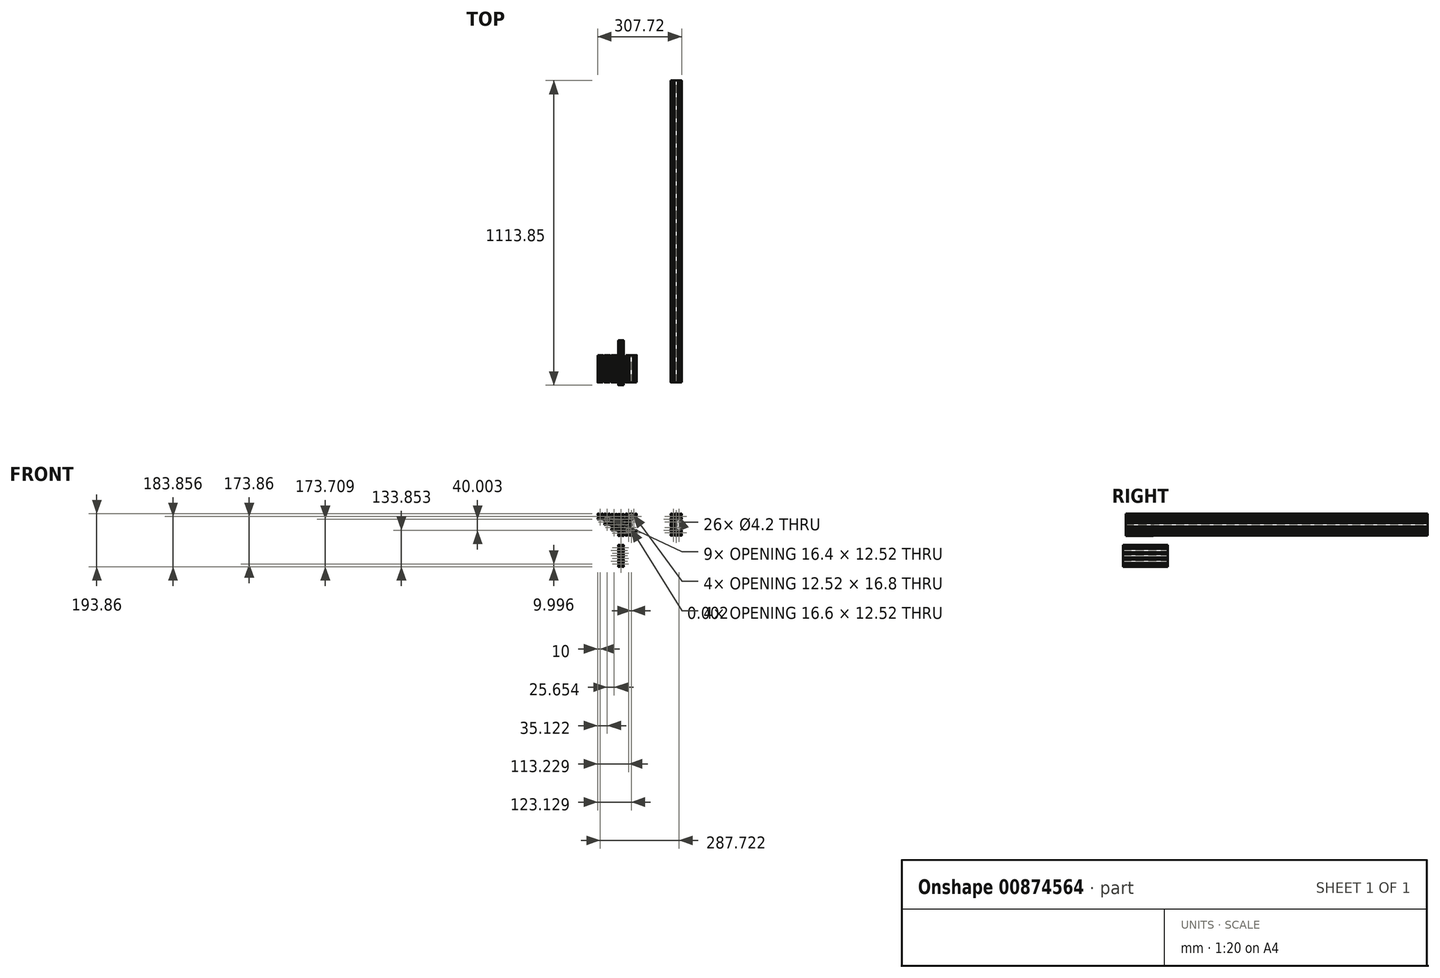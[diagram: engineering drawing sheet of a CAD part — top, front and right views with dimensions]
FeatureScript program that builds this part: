
annotation { "Feature Type Name" : "Feature", "Feature Type Description" : "" }
export const myFeature = defineFeature(function(context is Context, id is Id, definition is map)
    precondition{}
    {
        {
            var Q0;
            Q0=qCreatedBy(makeId("Front.planeOp"),FACE);
            var sketch = newSketch(context, id + "F0", { "sketchPlane" : qUnion([Q0])});
            skLineSegment(sketch, "E0", {"start": v(-0.16, 3.9) * mm, "end": v(-2.84, 3.9) * mm});
            skLineSegment(sketch, "E1", {"start": v(-2.84, 3.9) * mm, "end": v(-5.7, 6.76) * mm});
            skLineSegment(sketch, "E2", {"start": v(-5.7, 6.76) * mm, "end": v(-5.7, 8.4) * mm});
            skLineSegment(sketch, "E3", {"start": v(-5, 10) * mm, "end": v(-9.5, 10) * mm});
            skLineSegment(sketch, "E4", {"start": v(-10, 9.5) * mm, "end": v(-10, 5) * mm});
            skLineSegment(sketch, "E5", {"start": v(-8.4, 3.8) * mm, "end": v(-8.4, 5.7) * mm});
            skLineSegment(sketch, "E6", {"start": v(-8.4, 5.7) * mm, "end": v(-6.76, 5.7) * mm});
            skLineSegment(sketch, "E7", {"start": v(-6.76, 5.7) * mm, "end": v(-3.9, 2.84) * mm});
            skLineSegment(sketch, "E8", {"start": v(-3.9, 2.84) * mm, "end": v(-3.9, 0.16) * mm});
            skLineSegment(sketch, "E9", {"start": v(0, 0) * mm, "end": v(0, 17.32) * mm, "construction": true});
            skLineSegment(sketch, "E10", {"start": v(0, 0) * mm, "end": v(-27.38, 0) * mm, "construction": true});
            skPoint(sketch, "E11.visualSharp", {"position": v(-10, 10) * mm});
            skArc(sketch, "E11.filletArc", {"start": v(-9.5, 10) * mm, "mid": v(-9.85, 9.85) * mm, "end": v(-10, 9.5) * mm});
            skLineSegment(sketch, "E12.filletArc", {"start": v(-10, 4.72) * mm, "end": v(-10, 4.72) * mm});
            skLineSegment(sketch, "E13", {"start": v(-5.7, 8.4) * mm, "end": v(-3.8, 8.4) * mm});
            skLineSegment(sketch, "E14", {"start": v(-3.67, 8.74) * mm, "end": v(-4.87, 9.94) * mm});
            skLineSegment(sketch, "E15", {"start": v(-8.74, 3.67) * mm, "end": v(-9.94, 4.87) * mm});
            skPoint(sketch, "E16.visualSharp", {"position": v(-8.4, 3.33) * mm});
            skArc(sketch, "E16.filletArc", {"start": v(-8.74, 3.67) * mm, "mid": v(-8.52, 3.62) * mm, "end": v(-8.4, 3.8) * mm});
            skArc(sketch, "E17.filletArc", {"start": v(-3.8, 8.4) * mm, "mid": v(-3.62, 8.52) * mm, "end": v(-3.67, 8.74) * mm});
            skPoint(sketch, "E18.visualSharp", {"position": v(-4.92, 10) * mm});
            skArc(sketch, "E18.filletArc", {"start": v(-4.87, 9.94) * mm, "mid": v(-4.93, 9.99) * mm, "end": v(-5, 10) * mm});
            skPoint(sketch, "E19.visualSharp", {"position": v(-10, 4.93) * mm});
            skArc(sketch, "E19.filletArc", {"start": v(-10, 5) * mm, "mid": v(-9.99, 4.93) * mm, "end": v(-9.94, 4.87) * mm});
            skArc(sketch, "E20.MirrorCS", {"start": v(8.74, 3.67) * mm, "mid": v(8.52, 3.62) * mm, "end": v(8.4, 3.8) * mm});
            skArc(sketch, "E21.MirrorCS", {"start": v(10, 5) * mm, "mid": v(9.99, 4.93) * mm, "end": v(9.94, 4.87) * mm});
            skArc(sketch, "E22.MirrorCS", {"start": v(4.87, 9.94) * mm, "mid": v(4.93, 9.99) * mm, "end": v(5, 10) * mm});
            skArc(sketch, "E23.MirrorCS", {"start": v(3.8, 8.4) * mm, "mid": v(3.62, 8.52) * mm, "end": v(3.67, 8.74) * mm});
            skArc(sketch, "E24.MirrorCS", {"start": v(9.5, 10) * mm, "mid": v(9.85, 9.85) * mm, "end": v(10, 9.5) * mm});
            skPoint(sketch, "E25.MirrorP", {"position": v(8.4, 3.33) * mm});
            skLineSegment(sketch, "E26.MirrorCS", {"start": v(3.67, 8.74) * mm, "end": v(4.87, 9.94) * mm});
            skLineSegment(sketch, "E27.MirrorCS", {"start": v(6.76, 5.7) * mm, "end": v(3.9, 2.84) * mm});
            skLineSegment(sketch, "E28.MirrorCS", {"start": v(3.9, 2.84) * mm, "end": v(3.9, 0.16) * mm});
            skLineSegment(sketch, "E29.MirrorCS", {"start": v(10, 9.5) * mm, "end": v(10, 5) * mm});
            skLineSegment(sketch, "E30.MirrorCS", {"start": v(0.16, 3.9) * mm, "end": v(2.84, 3.9) * mm});
            skPoint(sketch, "E31.MirrorP", {"position": v(10, 4.93) * mm});
            skLineSegment(sketch, "E32.MirrorCS", {"start": v(8.4, 3.8) * mm, "end": v(8.4, 5.7) * mm});
            skLineSegment(sketch, "E33.MirrorCS", {"start": v(5.7, 8.4) * mm, "end": v(3.8, 8.4) * mm});
            skLineSegment(sketch, "E34.MirrorCS", {"start": v(2.84, 3.9) * mm, "end": v(5.7, 6.76) * mm});
            skPoint(sketch, "E35.MirrorP", {"position": v(3.33, 8.4) * mm});
            skLineSegment(sketch, "E36.MirrorCS", {"start": v(8.4, 5.7) * mm, "end": v(6.76, 5.7) * mm});
            skPoint(sketch, "E37.MirrorP", {"position": v(4.92, 10) * mm});
            skLineSegment(sketch, "E38.MirrorCS", {"start": v(8.74, 3.67) * mm, "end": v(9.94, 4.87) * mm});
            skLineSegment(sketch, "E39.MirrorCS", {"start": v(5.7, 6.76) * mm, "end": v(5.7, 8.4) * mm});
            skLineSegment(sketch, "E40.MirrorCS", {"start": v(5, 10) * mm, "end": v(9.5, 10) * mm});
            skPoint(sketch, "E41.MirrorP", {"position": v(10, 10) * mm});
            skArc(sketch, "E42.MirrorCS", {"start": v(-8.74, -3.67) * mm, "mid": v(-8.52, -3.62) * mm, "end": v(-8.4, -3.8) * mm});
            skArc(sketch, "E43.MirrorCS", {"start": v(-4.87, -9.94) * mm, "mid": v(-4.93, -9.99) * mm, "end": v(-5, -10) * mm});
            skArc(sketch, "E44.MirrorCS", {"start": v(-10, -5) * mm, "mid": v(-9.99, -4.93) * mm, "end": v(-9.94, -4.87) * mm});
            skArc(sketch, "E45.MirrorCS", {"start": v(10, -5) * mm, "mid": v(9.99, -4.93) * mm, "end": v(9.94, -4.87) * mm});
            skArc(sketch, "E46.MirrorCS", {"start": v(4.87, -9.94) * mm, "mid": v(4.93, -9.99) * mm, "end": v(5, -10) * mm});
            skArc(sketch, "E47.MirrorCS", {"start": v(-3.8, -8.4) * mm, "mid": v(-3.62, -8.52) * mm, "end": v(-3.67, -8.74) * mm});
            skArc(sketch, "E48.MirrorCS", {"start": v(8.74, -3.67) * mm, "mid": v(8.52, -3.62) * mm, "end": v(8.4, -3.8) * mm});
            skArc(sketch, "E49.MirrorCS", {"start": v(3.8, -8.4) * mm, "mid": v(3.62, -8.52) * mm, "end": v(3.67, -8.74) * mm});
            skLineSegment(sketch, "E50.MirrorCS", {"start": v(-8.74, -3.67) * mm, "end": v(-9.94, -4.87) * mm});
            skArc(sketch, "E51.MirrorCS", {"start": v(-9.5, -10) * mm, "mid": v(-9.85, -9.85) * mm, "end": v(-10, -9.5) * mm});
            skArc(sketch, "E52.MirrorCS", {"start": v(9.5, -10) * mm, "mid": v(9.85, -9.85) * mm, "end": v(10, -9.5) * mm});
            skLineSegment(sketch, "E53.MirrorCS", {"start": v(-3.67, -8.74) * mm, "end": v(-4.87, -9.94) * mm});
            skLineSegment(sketch, "E54.MirrorCS", {"start": v(-5.7, -8.4) * mm, "end": v(-3.8, -8.4) * mm});
            skLineSegment(sketch, "E55.MirrorCS", {"start": v(8.4, -5.7) * mm, "end": v(6.76, -5.7) * mm});
            skLineSegment(sketch, "E56.MirrorCS", {"start": v(8.74, -3.67) * mm, "end": v(9.94, -4.87) * mm});
            skLineSegment(sketch, "E57.MirrorCS", {"start": v(0, 0) * mm, "end": v(0, -17.32) * mm, "construction": true});
            skLineSegment(sketch, "E58.MirrorCS", {"start": v(5.7, -6.76) * mm, "end": v(5.7, -8.4) * mm});
            skLineSegment(sketch, "E59.MirrorCS", {"start": v(-3.9, -2.84) * mm, "end": v(-3.9, -0.16) * mm});
            skLineSegment(sketch, "E60.MirrorCS", {"start": v(5, -10) * mm, "end": v(9.5, -10) * mm});
            skLineSegment(sketch, "E61.MirrorCS", {"start": v(2.84, -3.9) * mm, "end": v(5.7, -6.76) * mm});
            skPoint(sketch, "E62.MirrorP", {"position": v(-4.92, -10) * mm});
            skPoint(sketch, "E63.MirrorP", {"position": v(-8.4, -3.33) * mm});
            skLineSegment(sketch, "E64.MirrorCS", {"start": v(0.16, -3.9) * mm, "end": v(2.84, -3.9) * mm});
            skLineSegment(sketch, "E65.MirrorCS", {"start": v(-5, -10) * mm, "end": v(-9.5, -10) * mm});
            skPoint(sketch, "E66.MirrorP", {"position": v(10, -10) * mm});
            skLineSegment(sketch, "E67.MirrorCS", {"start": v(-2.84, -3.9) * mm, "end": v(-5.7, -6.76) * mm});
            skLineSegment(sketch, "E68.MirrorCS", {"start": v(6.76, -5.7) * mm, "end": v(3.9, -2.84) * mm});
            skLineSegment(sketch, "E69.MirrorCS", {"start": v(-8.4, -5.7) * mm, "end": v(-6.76, -5.7) * mm});
            skLineSegment(sketch, "E70.MirrorCS", {"start": v(10, -9.5) * mm, "end": v(10, -5) * mm});
            skPoint(sketch, "E71.MirrorP", {"position": v(-3.33, -8.4) * mm});
            skLineSegment(sketch, "E72.MirrorCS", {"start": v(-10, -9.5) * mm, "end": v(-10, -5) * mm});
            skLineSegment(sketch, "E73.MirrorCS", {"start": v(-8.4, -3.8) * mm, "end": v(-8.4, -5.7) * mm});
            skPoint(sketch, "E74.MirrorP", {"position": v(3.33, -8.4) * mm});
            skLineSegment(sketch, "E75.MirrorCS", {"start": v(8.4, -3.8) * mm, "end": v(8.4, -5.7) * mm});
            skPoint(sketch, "E76.MirrorP", {"position": v(8.4, -3.33) * mm});
            skPoint(sketch, "E77.MirrorP", {"position": v(10, -4.93) * mm});
            skLineSegment(sketch, "E78.MirrorCS", {"start": v(-5.7, -6.76) * mm, "end": v(-5.7, -8.4) * mm});
            skLineSegment(sketch, "E79.MirrorCS", {"start": v(-6.76, -5.7) * mm, "end": v(-3.9, -2.84) * mm});
            skLineSegment(sketch, "E80.MirrorCS", {"start": v(-0.16, -3.9) * mm, "end": v(-2.84, -3.9) * mm});
            skLineSegment(sketch, "E81.MirrorCS", {"start": v(3.9, -2.84) * mm, "end": v(3.9, -0.16) * mm});
            skPoint(sketch, "E82.MirrorP", {"position": v(-10, -4.93) * mm});
            skPoint(sketch, "E83.MirrorP", {"position": v(4.92, -10) * mm});
            skLineSegment(sketch, "E84.MirrorCS", {"start": v(3.67, -8.74) * mm, "end": v(4.87, -9.94) * mm});
            skLineSegment(sketch, "E85.MirrorCS", {"start": v(5.7, -8.4) * mm, "end": v(3.8, -8.4) * mm});
            skPoint(sketch, "E86.MirrorP", {"position": v(-10, -10) * mm});
            skCircle(sketch, "E87", {"center": v(0, 0) * mm, "radius": 2.1 * mm});
            skLineSegment(sketch, "E88", {"start": v(-0.16, 3.9) * mm, "end": v(0, 3.74) * mm});
            skLineSegment(sketch, "E89", {"start": v(0, 3.74) * mm, "end": v(0.16, 3.9) * mm});
            skPoint(sketch, "E90.orphan", {"position": v(0, 3.9) * mm});
            skLineSegment(sketch, "E91.MirrorCS", {"start": v(-0.16, -3.9) * mm, "end": v(0, -3.74) * mm});
            skLineSegment(sketch, "E92.MirrorCS", {"start": v(0, -3.74) * mm, "end": v(0.16, -3.9) * mm});
            skLineSegment(sketch, "E93", {"start": v(-3.9, 0.16) * mm, "end": v(-3.74, 0) * mm});
            skLineSegment(sketch, "E94", {"start": v(-3.74, 0) * mm, "end": v(-3.9, -0.16) * mm});
            skPoint(sketch, "E95.orphan", {"position": v(-3.9, 0) * mm});
            skLineSegment(sketch, "E96.MirrorCS", {"start": v(3.74, 0) * mm, "end": v(3.9, -0.16) * mm});
            skLineSegment(sketch, "E97.MirrorCS", {"start": v(3.9, 0.16) * mm, "end": v(3.74, 0) * mm});
            skPoint(sketch, "E98.orphan", {"position": v(0, -3.9) * mm});
            skLineSegment(sketch, "E99", {"start": v(0.12, 0) * mm, "end": v(-27.26, 0) * mm, "construction": true});
            skLineSegment(sketch, "E100.filletArc", {"start": v(-9.88, 4.72) * mm, "end": v(-9.88, 4.72) * mm});
            skPoint(sketch, "E101.visualSharp", {"position": v(-3.2, 8.4) * mm});
            skPoint(sketch, "E102.orphan", {"position": v(0.12, 3.9) * mm});
            skPoint(sketch, "E103.orphan", {"position": v(-3.78, 0) * mm});
            skSolve(sketch);
        }
        {
            var Q0;
            Q0=qCreatedBy(makeId("Front.planeOp"),FACE);
            var sketch = newSketch(context, id + "F1", { "sketchPlane" : qUnion([Q0])});
            skLineSegment(sketch, "E104", {"start": v(24.96, 3.9) * mm, "end": v(22.28, 3.9) * mm});
            skLineSegment(sketch, "E105", {"start": v(22.28, 3.9) * mm, "end": v(19.42, 6.76) * mm});
            skLineSegment(sketch, "E106", {"start": v(19.42, 6.76) * mm, "end": v(19.42, 8.4) * mm});
            skLineSegment(sketch, "E107", {"start": v(20.11, 10) * mm, "end": v(15.62, 10) * mm});
            skLineSegment(sketch, "E108", {"start": v(15.12, 9.5) * mm, "end": v(15.12, 5) * mm});
            skLineSegment(sketch, "E109", {"start": v(16.72, 3.8) * mm, "end": v(16.72, 5.7) * mm});
            skLineSegment(sketch, "E110", {"start": v(16.72, 5.7) * mm, "end": v(18.36, 5.7) * mm});
            skLineSegment(sketch, "E111", {"start": v(18.36, 5.7) * mm, "end": v(21.22, 2.84) * mm});
            skLineSegment(sketch, "E112", {"start": v(21.22, 2.84) * mm, "end": v(21.22, 0.16) * mm});
            skLineSegment(sketch, "E113", {"start": v(25.12, 0) * mm, "end": v(25.12, 17.32) * mm, "construction": true});
            skLineSegment(sketch, "E114", {"start": v(25.12, 0) * mm, "end": v(-2.26, 0) * mm, "construction": true});
            skPoint(sketch, "E115.visualSharp", {"position": v(15.12, 10) * mm});
            skArc(sketch, "E115.filletArc", {"start": v(15.62, 10) * mm, "mid": v(15.27, 9.85) * mm, "end": v(15.12, 9.5) * mm});
            skLineSegment(sketch, "E116.filletArc", {"start": v(-9.88, 4.72) * mm, "end": v(-9.88, 4.72) * mm});
            skLineSegment(sketch, "E117", {"start": v(19.42, 8.4) * mm, "end": v(21.31, 8.4) * mm});
            skLineSegment(sketch, "E118", {"start": v(21.46, 8.74) * mm, "end": v(20.26, 9.94) * mm});
            skLineSegment(sketch, "E119", {"start": v(16.38, 3.67) * mm, "end": v(15.18, 4.87) * mm});
            skPoint(sketch, "E120.visualSharp", {"position": v(16.72, 3.33) * mm});
            skArc(sketch, "E120.filletArc", {"start": v(16.38, 3.67) * mm, "mid": v(16.6, 3.62) * mm, "end": v(16.72, 3.8) * mm});
            skPoint(sketch, "E121.visualSharp", {"position": v(21.8, 8.4) * mm});
            skArc(sketch, "E121.filletArc", {"start": v(21.31, 8.4) * mm, "mid": v(21.5, 8.52) * mm, "end": v(21.46, 8.74) * mm});
            skPoint(sketch, "E122.visualSharp", {"position": v(20.2, 10) * mm});
            skArc(sketch, "E122.filletArc", {"start": v(20.26, 9.94) * mm, "mid": v(20.2, 9.99) * mm, "end": v(20.11, 10) * mm});
            skPoint(sketch, "E123.visualSharp", {"position": v(15.12, 4.93) * mm});
            skArc(sketch, "E123.filletArc", {"start": v(15.12, 5) * mm, "mid": v(15.14, 4.93) * mm, "end": v(15.18, 4.87) * mm});
            skArc(sketch, "E124.MirrorCS", {"start": v(33.86, 3.67) * mm, "mid": v(33.65, 3.62) * mm, "end": v(33.52, 3.8) * mm});
            skArc(sketch, "E125.MirrorCS", {"start": v(35.12, 5) * mm, "mid": v(35.1, 4.93) * mm, "end": v(35.06, 4.87) * mm});
            skArc(sketch, "E126.MirrorCS", {"start": v(29.99, 9.94) * mm, "mid": v(30.05, 9.99) * mm, "end": v(30.13, 10) * mm});
            skArc(sketch, "E127.MirrorCS", {"start": v(28.93, 8.4) * mm, "mid": v(28.75, 8.52) * mm, "end": v(28.79, 8.74) * mm});
            skArc(sketch, "E128.MirrorCS", {"start": v(34.62, 10) * mm, "mid": v(34.98, 9.85) * mm, "end": v(35.12, 9.5) * mm});
            skPoint(sketch, "E129.MirrorP", {"position": v(33.52, 3.33) * mm});
            skLineSegment(sketch, "E130.MirrorCS", {"start": v(10.12, 4.72) * mm, "end": v(10.12, 4.72) * mm});
            skLineSegment(sketch, "E131.MirrorCS", {"start": v(28.79, 8.74) * mm, "end": v(29.99, 9.94) * mm});
            skLineSegment(sketch, "E132.MirrorCS", {"start": v(31.88, 5.7) * mm, "end": v(29.02, 2.84) * mm});
            skLineSegment(sketch, "E133.MirrorCS", {"start": v(29.02, 2.84) * mm, "end": v(29.02, 0.16) * mm});
            skLineSegment(sketch, "E134.MirrorCS", {"start": v(35.12, 9.5) * mm, "end": v(35.12, 5) * mm});
            skLineSegment(sketch, "E135.MirrorCS", {"start": v(25.28, 3.9) * mm, "end": v(27.96, 3.9) * mm});
            skPoint(sketch, "E136.MirrorP", {"position": v(35.12, 4.93) * mm});
            skLineSegment(sketch, "E137.MirrorCS", {"start": v(33.52, 3.8) * mm, "end": v(33.52, 5.7) * mm});
            skLineSegment(sketch, "E138.MirrorCS", {"start": v(30.82, 8.4) * mm, "end": v(28.93, 8.4) * mm});
            skLineSegment(sketch, "E139.MirrorCS", {"start": v(27.96, 3.9) * mm, "end": v(30.82, 6.76) * mm});
            skPoint(sketch, "E140.MirrorP", {"position": v(28.45, 8.4) * mm});
            skLineSegment(sketch, "E141.MirrorCS", {"start": v(33.52, 5.7) * mm, "end": v(31.88, 5.7) * mm});
            skPoint(sketch, "E142.MirrorP", {"position": v(30.05, 10) * mm});
            skLineSegment(sketch, "E143.MirrorCS", {"start": v(33.86, 3.67) * mm, "end": v(35.06, 4.87) * mm});
            skLineSegment(sketch, "E144.MirrorCS", {"start": v(30.82, 6.76) * mm, "end": v(30.82, 8.4) * mm});
            skLineSegment(sketch, "E145.MirrorCS", {"start": v(30.13, 10) * mm, "end": v(34.62, 10) * mm});
            skPoint(sketch, "E146.MirrorP", {"position": v(35.12, 10) * mm});
            skArc(sketch, "E147.MirrorCS", {"start": v(16.38, -3.67) * mm, "mid": v(16.6, -3.62) * mm, "end": v(16.72, -3.8) * mm});
            skArc(sketch, "E148.MirrorCS", {"start": v(15.12, -5) * mm, "mid": v(15.14, -4.93) * mm, "end": v(15.18, -4.87) * mm});
            skArc(sketch, "E149.MirrorCS", {"start": v(35.12, -5) * mm, "mid": v(35.1, -4.93) * mm, "end": v(35.06, -4.87) * mm});
            skArc(sketch, "E150.MirrorCS", {"start": v(33.86, -3.67) * mm, "mid": v(33.65, -3.62) * mm, "end": v(33.52, -3.8) * mm});
            skLineSegment(sketch, "E151.MirrorCS", {"start": v(16.38, -3.67) * mm, "end": v(15.18, -4.87) * mm});
            skLineSegment(sketch, "E152.MirrorCS", {"start": v(33.52, -5.7) * mm, "end": v(31.88, -5.7) * mm});
            skLineSegment(sketch, "E153.MirrorCS", {"start": v(33.86, -3.67) * mm, "end": v(35.06, -4.87) * mm});
            skLineSegment(sketch, "E154.MirrorCS", {"start": v(25.12, 0) * mm, "end": v(25.12, -17.32) * mm, "construction": true});
            skLineSegment(sketch, "E155.MirrorCS", {"start": v(30.82, -6.76) * mm, "end": v(30.82, -8.4) * mm});
            skLineSegment(sketch, "E156.MirrorCS", {"start": v(21.22, -2.84) * mm, "end": v(21.22, -0.16) * mm});
            skLineSegment(sketch, "E157.MirrorCS", {"start": v(27.96, -3.9) * mm, "end": v(30.82, -6.76) * mm});
            skPoint(sketch, "E158.MirrorP", {"position": v(16.72, -3.33) * mm});
            skLineSegment(sketch, "E159.MirrorCS", {"start": v(25.28, -3.9) * mm, "end": v(27.96, -3.9) * mm});
            skLineSegment(sketch, "E160.MirrorCS", {"start": v(22.28, -3.9) * mm, "end": v(19.42, -6.76) * mm});
            skLineSegment(sketch, "E161.MirrorCS", {"start": v(31.88, -5.7) * mm, "end": v(29.02, -2.84) * mm});
            skLineSegment(sketch, "E162.MirrorCS", {"start": v(16.72, -5.7) * mm, "end": v(18.36, -5.7) * mm});
            skLineSegment(sketch, "E163.MirrorCS", {"start": v(35.12, -9.5) * mm, "end": v(35.12, -5) * mm});
            skLineSegment(sketch, "E164.MirrorCS", {"start": v(15.12, -9.5) * mm, "end": v(15.12, -5) * mm});
            skLineSegment(sketch, "E165.MirrorCS", {"start": v(16.72, -3.8) * mm, "end": v(16.72, -5.7) * mm});
            skLineSegment(sketch, "E166.MirrorCS", {"start": v(33.52, -3.8) * mm, "end": v(33.52, -5.7) * mm});
            skPoint(sketch, "E167.MirrorP", {"position": v(33.52, -3.33) * mm});
            skPoint(sketch, "E168.MirrorP", {"position": v(35.12, -4.93) * mm});
            skLineSegment(sketch, "E169.MirrorCS", {"start": v(19.42, -6.76) * mm, "end": v(19.42, -8.4) * mm});
            skLineSegment(sketch, "E170.MirrorCS", {"start": v(18.36, -5.7) * mm, "end": v(21.22, -2.84) * mm});
            skLineSegment(sketch, "E171.MirrorCS", {"start": v(24.96, -3.9) * mm, "end": v(22.28, -3.9) * mm});
            skLineSegment(sketch, "E172.MirrorCS", {"start": v(29.02, -2.84) * mm, "end": v(29.02, -0.16) * mm});
            skLineSegment(sketch, "E173.MirrorCS", {"start": v(-9.88, -4.72) * mm, "end": v(-9.88, -4.72) * mm});
            skPoint(sketch, "E174.MirrorP", {"position": v(15.12, -4.93) * mm});
            skLineSegment(sketch, "E175.MirrorCS", {"start": v(10.12, -4.72) * mm, "end": v(10.12, -4.72) * mm});
            skPoint(sketch, "E176.MirrorP", {"position": v(15.12, -10) * mm});
            skCircle(sketch, "E177", {"center": v(25.12, 0) * mm, "radius": 2.1 * mm});
            skLineSegment(sketch, "E178", {"start": v(24.96, 3.9) * mm, "end": v(25.12, 3.74) * mm});
            skLineSegment(sketch, "E179", {"start": v(25.12, 3.74) * mm, "end": v(25.28, 3.9) * mm});
            skPoint(sketch, "E180.orphan", {"position": v(25.12, 3.9) * mm});
            skLineSegment(sketch, "E181.MirrorCS", {"start": v(24.96, -3.9) * mm, "end": v(25.12, -3.74) * mm});
            skLineSegment(sketch, "E182.MirrorCS", {"start": v(25.12, -3.74) * mm, "end": v(25.28, -3.9) * mm});
            skLineSegment(sketch, "E183", {"start": v(21.22, 0.16) * mm, "end": v(21.38, 0) * mm});
            skLineSegment(sketch, "E184", {"start": v(21.38, 0) * mm, "end": v(21.22, -0.16) * mm});
            skPoint(sketch, "E185.orphan", {"position": v(21.22, 0) * mm});
            skLineSegment(sketch, "E186.MirrorCS", {"start": v(28.86, 0) * mm, "end": v(29.02, -0.16) * mm});
            skLineSegment(sketch, "E187.MirrorCS", {"start": v(29.02, 0.16) * mm, "end": v(28.86, 0) * mm});
            skPoint(sketch, "E188.orphan", {"position": v(29.02, 0) * mm});
            skPoint(sketch, "E189.orphan", {"position": v(25.12, -3.9) * mm});
            skArc(sketch, "E190.MirrorCS", {"start": v(35.12, -25) * mm, "mid": v(35.1, -24.93) * mm, "end": v(35.06, -24.87) * mm});
            skLineSegment(sketch, "E191.MirrorCS", {"start": v(24.96, -23.9) * mm, "end": v(25.12, -23.74) * mm});
            skLineSegment(sketch, "E192.MirrorCS", {"start": v(24.96, -16.1) * mm, "end": v(25.12, -16.26) * mm});
            skLineSegment(sketch, "E193.MirrorCS", {"start": v(25.12, -23.74) * mm, "end": v(25.28, -23.9) * mm});
            skArc(sketch, "E194.MirrorCS", {"start": v(15.12, -25) * mm, "mid": v(15.14, -24.93) * mm, "end": v(15.18, -24.87) * mm});
            skArc(sketch, "E195.MirrorCS", {"start": v(33.86, -16.33) * mm, "mid": v(33.65, -16.38) * mm, "end": v(33.52, -16.2) * mm});
            skLineSegment(sketch, "E196.MirrorCS", {"start": v(21.22, -20.16) * mm, "end": v(21.38, -20) * mm});
            skLineSegment(sketch, "E197.MirrorCS", {"start": v(29.02, -20.16) * mm, "end": v(28.86, -20) * mm});
            skArc(sketch, "E198.MirrorCS", {"start": v(15.12, -15) * mm, "mid": v(15.14, -15.07) * mm, "end": v(15.18, -15.13) * mm});
            skArc(sketch, "E199.MirrorCS", {"start": v(29.99, -29.94) * mm, "mid": v(30.05, -29.99) * mm, "end": v(30.13, -30) * mm});
            skLineSegment(sketch, "E200.MirrorCS", {"start": v(25.12, -16.26) * mm, "end": v(25.28, -16.1) * mm});
            skLineSegment(sketch, "E201.MirrorCS", {"start": v(21.38, -20) * mm, "end": v(21.22, -19.84) * mm});
            skArc(sketch, "E202.MirrorCS", {"start": v(35.12, -15) * mm, "mid": v(35.1, -15.07) * mm, "end": v(35.06, -15.13) * mm});
            skLineSegment(sketch, "E203.MirrorCS", {"start": v(28.86, -20) * mm, "end": v(29.02, -19.84) * mm});
            skArc(sketch, "E204.MirrorCS", {"start": v(20.26, -29.94) * mm, "mid": v(20.2, -29.99) * mm, "end": v(20.11, -30) * mm});
            skArc(sketch, "E205.MirrorCS", {"start": v(16.38, -16.33) * mm, "mid": v(16.6, -16.38) * mm, "end": v(16.72, -16.2) * mm});
            skArc(sketch, "E206.MirrorCS", {"start": v(15.62, -30) * mm, "mid": v(15.27, -29.86) * mm, "end": v(15.12, -29.5) * mm});
            skLineSegment(sketch, "E207.MirrorCS", {"start": v(16.38, -16.33) * mm, "end": v(15.18, -15.13) * mm});
            skLineSegment(sketch, "E208.MirrorCS", {"start": v(33.86, -16.33) * mm, "end": v(35.06, -15.13) * mm});
            skArc(sketch, "E209.MirrorCS", {"start": v(16.38, -23.67) * mm, "mid": v(16.6, -23.62) * mm, "end": v(16.72, -23.8) * mm});
            skLineSegment(sketch, "E210.MirrorCS", {"start": v(16.38, -23.67) * mm, "end": v(15.18, -24.87) * mm});
            skLineSegment(sketch, "E211.MirrorCS", {"start": v(33.52, -25.7) * mm, "end": v(31.88, -25.7) * mm});
            skLineSegment(sketch, "E212.MirrorCS", {"start": v(16.72, -14.3) * mm, "end": v(18.36, -14.3) * mm});
            skArc(sketch, "E213.MirrorCS", {"start": v(28.93, -28.4) * mm, "mid": v(28.75, -28.53) * mm, "end": v(28.79, -28.74) * mm});
            skArc(sketch, "E214.MirrorCS", {"start": v(34.62, -30) * mm, "mid": v(34.98, -29.86) * mm, "end": v(35.12, -29.5) * mm});
            skLineSegment(sketch, "E215.MirrorCS", {"start": v(30.82, -26.76) * mm, "end": v(30.82, -28.4) * mm});
            skArc(sketch, "E216.MirrorCS", {"start": v(33.86, -23.67) * mm, "mid": v(33.65, -23.62) * mm, "end": v(33.52, -23.8) * mm});
            skArc(sketch, "E217.MirrorCS", {"start": v(21.31, -28.4) * mm, "mid": v(21.5, -28.53) * mm, "end": v(21.46, -28.74) * mm});
            skLineSegment(sketch, "E218.MirrorCS", {"start": v(16.72, -25.7) * mm, "end": v(18.36, -25.7) * mm});
            skLineSegment(sketch, "E219.MirrorCS", {"start": v(21.46, -28.74) * mm, "end": v(20.26, -29.94) * mm});
            skLineSegment(sketch, "E220.MirrorCS", {"start": v(19.42, -26.76) * mm, "end": v(19.42, -28.4) * mm});
            skLineSegment(sketch, "E221.MirrorCS", {"start": v(28.79, -28.74) * mm, "end": v(29.99, -29.94) * mm});
            skLineSegment(sketch, "E222.MirrorCS", {"start": v(33.86, -23.67) * mm, "end": v(35.06, -24.87) * mm});
            skLineSegment(sketch, "E223.MirrorCS", {"start": v(33.52, -14.3) * mm, "end": v(31.88, -14.3) * mm});
            skLineSegment(sketch, "E224.MirrorCS", {"start": v(16.72, -23.8) * mm, "end": v(16.72, -25.7) * mm});
            skPoint(sketch, "E225.MirrorP", {"position": v(25.12, -23.9) * mm});
            skPoint(sketch, "E226.MirrorP", {"position": v(25.12, -16.1) * mm});
            skPoint(sketch, "E227.MirrorP", {"position": v(29.02, -20) * mm});
            skPoint(sketch, "E228.MirrorP", {"position": v(21.22, -20) * mm});
            skPoint(sketch, "E229.MirrorP", {"position": v(15.12, -30) * mm});
            skPoint(sketch, "E230.MirrorP", {"position": v(33.52, -23.33) * mm});
            skPoint(sketch, "E231.MirrorP", {"position": v(28.45, -28.4) * mm});
            skLineSegment(sketch, "E232.MirrorCS", {"start": v(30.13, -30) * mm, "end": v(34.62, -30) * mm});
            skPoint(sketch, "E233.MirrorP", {"position": v(15.12, -24.93) * mm});
            skPoint(sketch, "E234.MirrorP", {"position": v(16.72, -16.68) * mm});
            skLineSegment(sketch, "E235.MirrorCS", {"start": v(19.42, -28.4) * mm, "end": v(21.31, -28.4) * mm});
            skLineSegment(sketch, "E236.MirrorCS", {"start": v(31.88, -14.3) * mm, "end": v(29.02, -17.16) * mm});
            skPoint(sketch, "E237.MirrorP", {"position": v(30.05, -30) * mm});
            skLineSegment(sketch, "E238.MirrorCS", {"start": v(20.11, -30) * mm, "end": v(15.62, -30) * mm});
            skLineSegment(sketch, "E239.MirrorCS", {"start": v(15.12, -29.5) * mm, "end": v(15.12, -25) * mm});
            skLineSegment(sketch, "E240.MirrorCS", {"start": v(35.12, -29.5) * mm, "end": v(35.12, -25) * mm});
            skLineSegment(sketch, "E241.MirrorCS", {"start": v(25.12, -20) * mm, "end": v(25.12, -2.68) * mm, "construction": true});
            skLineSegment(sketch, "E242.MirrorCS", {"start": v(27.96, -23.9) * mm, "end": v(30.82, -26.76) * mm});
            skLineSegment(sketch, "E243.MirrorCS", {"start": v(22.28, -16.1) * mm, "end": v(19.42, -13.24) * mm});
            skLineSegment(sketch, "E244.MirrorCS", {"start": v(24.96, -16.1) * mm, "end": v(22.28, -16.1) * mm});
            skLineSegment(sketch, "E245.MirrorCS", {"start": v(15.12, -10.5) * mm, "end": v(15.12, -15) * mm});
            skPoint(sketch, "E246.MirrorP", {"position": v(35.12, -30) * mm});
            skLineSegment(sketch, "E247.MirrorCS", {"start": v(25.12, -20) * mm, "end": v(25.12, -37.32) * mm, "construction": true});
            skLineSegment(sketch, "E248.MirrorCS", {"start": v(31.88, -25.7) * mm, "end": v(29.02, -22.84) * mm});
            skPoint(sketch, "E249.MirrorP", {"position": v(33.52, -16.68) * mm});
            skLineSegment(sketch, "E250.MirrorCS", {"start": v(25.28, -23.9) * mm, "end": v(27.96, -23.9) * mm});
            skLineSegment(sketch, "E251.MirrorCS", {"start": v(33.52, -16.2) * mm, "end": v(33.52, -14.3) * mm});
            skCircle(sketch, "E252.MirrorC", {"center": v(25.12, -20) * mm, "radius": 2.1 * mm});
            skPoint(sketch, "E253.MirrorP", {"position": v(21.8, -28.4) * mm});
            skPoint(sketch, "E254.MirrorP", {"position": v(16.72, -23.33) * mm});
            skLineSegment(sketch, "E255.MirrorCS", {"start": v(21.22, -17.16) * mm, "end": v(21.22, -19.84) * mm});
            skLineSegment(sketch, "E256.MirrorCS", {"start": v(25.12, -20) * mm, "end": v(-2.26, -20) * mm, "construction": true});
            skLineSegment(sketch, "E257.MirrorCS", {"start": v(19.42, -13.24) * mm, "end": v(19.42, -11.6) * mm});
            skPoint(sketch, "E258.MirrorP", {"position": v(20.2, -30) * mm});
            skLineSegment(sketch, "E259.MirrorCS", {"start": v(29.02, -17.16) * mm, "end": v(29.02, -19.84) * mm});
            skLineSegment(sketch, "E260.MirrorCS", {"start": v(16.72, -16.2) * mm, "end": v(16.72, -14.3) * mm});
            skPoint(sketch, "E261.MirrorP", {"position": v(35.12, -15.08) * mm});
            skLineSegment(sketch, "E262.MirrorCS", {"start": v(30.82, -13.24) * mm, "end": v(30.82, -11.6) * mm});
            skLineSegment(sketch, "E263.MirrorCS", {"start": v(25.28, -16.1) * mm, "end": v(27.96, -16.1) * mm});
            skLineSegment(sketch, "E264.MirrorCS", {"start": v(29.02, -22.84) * mm, "end": v(29.02, -20.16) * mm});
            skLineSegment(sketch, "E265.MirrorCS", {"start": v(18.36, -14.3) * mm, "end": v(21.22, -17.16) * mm});
            skPoint(sketch, "E266.MirrorP", {"position": v(35.12, -24.93) * mm});
            skPoint(sketch, "E267.MirrorP", {"position": v(15.12, -15.08) * mm});
            skLineSegment(sketch, "E268.MirrorCS", {"start": v(33.52, -23.8) * mm, "end": v(33.52, -25.7) * mm});
            skLineSegment(sketch, "E269.MirrorCS", {"start": v(18.36, -25.7) * mm, "end": v(21.22, -22.84) * mm});
            skLineSegment(sketch, "E270.MirrorCS", {"start": v(30.82, -28.4) * mm, "end": v(28.93, -28.4) * mm});
            skLineSegment(sketch, "E271.MirrorCS", {"start": v(27.96, -16.1) * mm, "end": v(30.82, -13.24) * mm});
            skLineSegment(sketch, "E272.MirrorCS", {"start": v(22.28, -23.9) * mm, "end": v(19.42, -26.76) * mm});
            skLineSegment(sketch, "E273.MirrorCS", {"start": v(24.96, -23.9) * mm, "end": v(22.28, -23.9) * mm});
            skLineSegment(sketch, "E274.MirrorCS", {"start": v(35.12, -10.5) * mm, "end": v(35.12, -15) * mm});
            skLineSegment(sketch, "E275.MirrorCS", {"start": v(21.22, -22.84) * mm, "end": v(21.22, -20.16) * mm});
            skLineSegment(sketch, "E276", {"start": v(19.42, -8.4) * mm, "end": v(19.42, -11.6) * mm});
            skLineSegment(sketch, "E277", {"start": v(30.82, -8.4) * mm, "end": v(30.82, -11.6) * mm});
            skLineSegment(sketch, "E278", {"start": v(15.12, -9.5) * mm, "end": v(15.12, -10.5) * mm});
            skLineSegment(sketch, "E279", {"start": v(35.12, -9.5) * mm, "end": v(35.12, -10.5) * mm});
            skSolve(sketch);
        }
        {
            var Q0;
            Q0=qCreatedBy(makeId("Front.planeOp"),FACE);
            var sketch = newSketch(context, id + "F2", { "sketchPlane" : qUnion([Q0])});
            skLineSegment(sketch, "E280.filletArc", {"start": v(-9.88, 4.72) * mm, "end": v(-9.88, 4.72) * mm});
            skLineSegment(sketch, "E281.MirrorCS", {"start": v(10.12, 4.72) * mm, "end": v(10.12, 4.72) * mm});
            skLineSegment(sketch, "E282.MirrorCS", {"start": v(-9.88, -4.72) * mm, "end": v(-9.88, -4.72) * mm});
            skLineSegment(sketch, "E283.MirrorCS", {"start": v(10.12, -4.72) * mm, "end": v(10.12, -4.72) * mm});
            skLineSegment(sketch, "E284", {"start": v(50.62, 3.7) * mm, "end": v(47.94, 3.7) * mm});
            skLineSegment(sketch, "E285", {"start": v(47.94, 3.7) * mm, "end": v(45.08, 6.55) * mm});
            skLineSegment(sketch, "E286", {"start": v(45.08, 6.55) * mm, "end": v(45.08, 8.2) * mm});
            skLineSegment(sketch, "E287", {"start": v(45.77, 9.8) * mm, "end": v(41.28, 9.8) * mm});
            skLineSegment(sketch, "E288", {"start": v(40.78, 9.3) * mm, "end": v(40.78, 4.8) * mm});
            skLineSegment(sketch, "E289", {"start": v(42.38, 3.6) * mm, "end": v(42.38, 5.5) * mm});
            skLineSegment(sketch, "E290", {"start": v(42.38, 5.5) * mm, "end": v(44.02, 5.5) * mm});
            skLineSegment(sketch, "E291", {"start": v(44.02, 5.5) * mm, "end": v(46.88, 2.63) * mm});
            skLineSegment(sketch, "E292", {"start": v(46.88, 2.63) * mm, "end": v(46.88, -0.05) * mm});
            skLineSegment(sketch, "E293", {"start": v(50.78, -0.2) * mm, "end": v(50.78, 17.11) * mm, "construction": true});
            skLineSegment(sketch, "E294", {"start": v(50.78, -0.2) * mm, "end": v(23.4, -0.2) * mm, "construction": true});
            skPoint(sketch, "E295.visualSharp", {"position": v(40.78, 9.8) * mm});
            skArc(sketch, "E295.filletArc", {"start": v(41.28, 9.8) * mm, "mid": v(40.92, 9.64) * mm, "end": v(40.78, 9.3) * mm});
            skLineSegment(sketch, "E296.filletArc", {"start": v(-34.22, 14.52) * mm, "end": v(-34.22, 14.52) * mm});
            skLineSegment(sketch, "E297", {"start": v(45.08, 8.2) * mm, "end": v(46.97, 8.2) * mm});
            skLineSegment(sketch, "E298", {"start": v(47.1, 8.53) * mm, "end": v(45.9, 9.73) * mm});
            skLineSegment(sketch, "E299", {"start": v(42.03, 3.46) * mm, "end": v(40.83, 4.66) * mm});
            skPoint(sketch, "E300.visualSharp", {"position": v(42.38, 3.12) * mm});
            skArc(sketch, "E300.filletArc", {"start": v(42.03, 3.46) * mm, "mid": v(42.25, 3.41) * mm, "end": v(42.38, 3.6) * mm});
            skPoint(sketch, "E301.visualSharp", {"position": v(47.45, 8.2) * mm});
            skArc(sketch, "E301.filletArc", {"start": v(46.97, 8.2) * mm, "mid": v(47.15, 8.31) * mm, "end": v(47.1, 8.53) * mm});
            skPoint(sketch, "E302.visualSharp", {"position": v(45.85, 9.8) * mm});
            skArc(sketch, "E302.filletArc", {"start": v(45.9, 9.73) * mm, "mid": v(45.84, 9.78) * mm, "end": v(45.77, 9.8) * mm});
            skPoint(sketch, "E303.visualSharp", {"position": v(40.78, 4.72) * mm});
            skArc(sketch, "E303.filletArc", {"start": v(40.78, 4.8) * mm, "mid": v(40.8, 4.72) * mm, "end": v(40.83, 4.66) * mm});
            skArc(sketch, "E304.MirrorCS", {"start": v(59.52, 3.46) * mm, "mid": v(59.3, 3.41) * mm, "end": v(59.18, 3.6) * mm});
            skArc(sketch, "E305.MirrorCS", {"start": v(60.78, 4.8) * mm, "mid": v(60.76, 4.72) * mm, "end": v(60.72, 4.66) * mm});
            skArc(sketch, "E306.MirrorCS", {"start": v(55.64, 9.73) * mm, "mid": v(55.7, 9.78) * mm, "end": v(55.78, 9.8) * mm});
            skArc(sketch, "E307.MirrorCS", {"start": v(54.58, 8.2) * mm, "mid": v(54.4, 8.31) * mm, "end": v(54.44, 8.53) * mm});
            skArc(sketch, "E308.MirrorCS", {"start": v(60.28, 9.8) * mm, "mid": v(60.63, 9.64) * mm, "end": v(60.78, 9.3) * mm});
            skPoint(sketch, "E309.MirrorP", {"position": v(59.18, 3.12) * mm});
            skLineSegment(sketch, "E310.MirrorCS", {"start": v(-14.22, 14.52) * mm, "end": v(-14.22, 14.52) * mm});
            skLineSegment(sketch, "E311.MirrorCS", {"start": v(54.44, 8.53) * mm, "end": v(55.64, 9.73) * mm});
            skLineSegment(sketch, "E312.MirrorCS", {"start": v(57.54, 5.5) * mm, "end": v(54.68, 2.63) * mm});
            skLineSegment(sketch, "E313.MirrorCS", {"start": v(54.68, 2.63) * mm, "end": v(54.68, -0.05) * mm});
            skLineSegment(sketch, "E314.MirrorCS", {"start": v(60.78, 9.3) * mm, "end": v(60.78, 4.8) * mm});
            skLineSegment(sketch, "E315.MirrorCS", {"start": v(50.94, 3.7) * mm, "end": v(53.62, 3.7) * mm});
            skPoint(sketch, "E316.MirrorP", {"position": v(60.78, 4.72) * mm});
            skLineSegment(sketch, "E317.MirrorCS", {"start": v(59.18, 3.6) * mm, "end": v(59.18, 5.5) * mm});
            skLineSegment(sketch, "E318.MirrorCS", {"start": v(56.48, 8.2) * mm, "end": v(54.58, 8.2) * mm});
            skLineSegment(sketch, "E319.MirrorCS", {"start": v(53.62, 3.7) * mm, "end": v(56.48, 6.55) * mm});
            skPoint(sketch, "E320.MirrorP", {"position": v(54.1, 8.2) * mm});
            skLineSegment(sketch, "E321.MirrorCS", {"start": v(59.18, 5.5) * mm, "end": v(57.54, 5.5) * mm});
            skPoint(sketch, "E322.MirrorP", {"position": v(55.7, 9.8) * mm});
            skLineSegment(sketch, "E323.MirrorCS", {"start": v(59.52, 3.46) * mm, "end": v(60.72, 4.66) * mm});
            skLineSegment(sketch, "E324.MirrorCS", {"start": v(56.48, 6.55) * mm, "end": v(56.48, 8.2) * mm});
            skLineSegment(sketch, "E325.MirrorCS", {"start": v(55.78, 9.8) * mm, "end": v(60.28, 9.8) * mm});
            skPoint(sketch, "E326.MirrorP", {"position": v(60.78, 9.8) * mm});
            skArc(sketch, "E327.MirrorCS", {"start": v(42.03, -3.88) * mm, "mid": v(42.25, -3.83) * mm, "end": v(42.38, -4.02) * mm});
            skArc(sketch, "E328.MirrorCS", {"start": v(40.78, -5.22) * mm, "mid": v(40.8, -5.14) * mm, "end": v(40.83, -5.08) * mm});
            skArc(sketch, "E329.MirrorCS", {"start": v(60.78, -5.22) * mm, "mid": v(60.76, -5.14) * mm, "end": v(60.72, -5.08) * mm});
            skArc(sketch, "E330.MirrorCS", {"start": v(59.52, -3.88) * mm, "mid": v(59.3, -3.83) * mm, "end": v(59.18, -4.02) * mm});
            skLineSegment(sketch, "E331.MirrorCS", {"start": v(42.03, -3.88) * mm, "end": v(40.83, -5.08) * mm});
            skLineSegment(sketch, "E332.MirrorCS", {"start": v(59.18, -5.9) * mm, "end": v(57.54, -5.9) * mm});
            skLineSegment(sketch, "E333.MirrorCS", {"start": v(59.52, -3.88) * mm, "end": v(60.72, -5.08) * mm});
            skLineSegment(sketch, "E334.MirrorCS", {"start": v(50.78, -0.2) * mm, "end": v(50.78, -17.53) * mm, "construction": true});
            skLineSegment(sketch, "E335.MirrorCS", {"start": v(56.48, -6.97) * mm, "end": v(56.48, -8.61) * mm});
            skLineSegment(sketch, "E336.MirrorCS", {"start": v(46.88, -3.05) * mm, "end": v(46.88, -0.37) * mm});
            skLineSegment(sketch, "E337.MirrorCS", {"start": v(53.62, -4.11) * mm, "end": v(56.48, -6.97) * mm});
            skPoint(sketch, "E338.MirrorP", {"position": v(42.38, -3.53) * mm});
            skLineSegment(sketch, "E339.MirrorCS", {"start": v(50.94, -4.11) * mm, "end": v(53.62, -4.11) * mm});
            skLineSegment(sketch, "E340.MirrorCS", {"start": v(47.94, -4.11) * mm, "end": v(45.08, -6.97) * mm});
            skLineSegment(sketch, "E341.MirrorCS", {"start": v(57.54, -5.9) * mm, "end": v(54.68, -3.05) * mm});
            skLineSegment(sketch, "E342.MirrorCS", {"start": v(42.38, -5.9) * mm, "end": v(44.02, -5.9) * mm});
            skLineSegment(sketch, "E343.MirrorCS", {"start": v(60.78, -9.71) * mm, "end": v(60.78, -5.22) * mm});
            skLineSegment(sketch, "E344.MirrorCS", {"start": v(40.78, -9.71) * mm, "end": v(40.78, -5.22) * mm});
            skLineSegment(sketch, "E345.MirrorCS", {"start": v(42.38, -4.02) * mm, "end": v(42.38, -5.9) * mm});
            skLineSegment(sketch, "E346.MirrorCS", {"start": v(59.18, -4.02) * mm, "end": v(59.18, -5.9) * mm});
            skPoint(sketch, "E347.MirrorP", {"position": v(59.18, -3.53) * mm});
            skPoint(sketch, "E348.MirrorP", {"position": v(60.78, -5.13) * mm});
            skLineSegment(sketch, "E349.MirrorCS", {"start": v(45.08, -6.97) * mm, "end": v(45.08, -8.61) * mm});
            skLineSegment(sketch, "E350.MirrorCS", {"start": v(44.02, -5.9) * mm, "end": v(46.88, -3.05) * mm});
            skLineSegment(sketch, "E351.MirrorCS", {"start": v(50.62, -4.11) * mm, "end": v(47.94, -4.11) * mm});
            skLineSegment(sketch, "E352.MirrorCS", {"start": v(54.68, -3.05) * mm, "end": v(54.68, -0.37) * mm});
            skLineSegment(sketch, "E353.MirrorCS", {"start": v(-34.22, 5.07) * mm, "end": v(-34.22, 5.07) * mm});
            skPoint(sketch, "E354.MirrorP", {"position": v(40.78, -5.13) * mm});
            skLineSegment(sketch, "E355.MirrorCS", {"start": v(-14.22, 5.07) * mm, "end": v(-14.22, 5.07) * mm});
            skPoint(sketch, "E356.MirrorP", {"position": v(40.78, -10.21) * mm});
            skCircle(sketch, "E357", {"center": v(50.78, -0.2) * mm, "radius": 2.1 * mm});
            skLineSegment(sketch, "E358", {"start": v(50.62, 3.7) * mm, "end": v(50.78, 3.53) * mm});
            skLineSegment(sketch, "E359", {"start": v(50.78, 3.53) * mm, "end": v(50.94, 3.7) * mm});
            skPoint(sketch, "E360.orphan", {"position": v(50.78, 3.7) * mm});
            skLineSegment(sketch, "E361.MirrorCS", {"start": v(50.62, -4.11) * mm, "end": v(50.78, -3.95) * mm});
            skLineSegment(sketch, "E362.MirrorCS", {"start": v(50.78, -3.95) * mm, "end": v(50.94, -4.11) * mm});
            skLineSegment(sketch, "E363", {"start": v(46.88, -0.05) * mm, "end": v(47.03, -0.2) * mm});
            skLineSegment(sketch, "E364", {"start": v(47.03, -0.2) * mm, "end": v(46.88, -0.37) * mm});
            skPoint(sketch, "E365.orphan", {"position": v(46.88, -0.2) * mm});
            skLineSegment(sketch, "E366.MirrorCS", {"start": v(54.52, -0.2) * mm, "end": v(54.68, -0.37) * mm});
            skLineSegment(sketch, "E367.MirrorCS", {"start": v(54.68, -0.05) * mm, "end": v(54.52, -0.2) * mm});
            skPoint(sketch, "E368.orphan", {"position": v(54.68, -0.2) * mm});
            skPoint(sketch, "E369.orphan", {"position": v(50.78, -4.11) * mm});
            skLineSegment(sketch, "E370.MirrorCS", {"start": v(50.62, -16.31) * mm, "end": v(50.78, -16.47) * mm});
            skArc(sketch, "E371.MirrorCS", {"start": v(59.52, -16.54) * mm, "mid": v(59.3, -16.59) * mm, "end": v(59.18, -16.4) * mm});
            skArc(sketch, "E372.MirrorCS", {"start": v(40.78, -15.2) * mm, "mid": v(40.8, -15.28) * mm, "end": v(40.83, -15.34) * mm});
            skLineSegment(sketch, "E373.MirrorCS", {"start": v(50.78, -16.47) * mm, "end": v(50.94, -16.31) * mm});
            skArc(sketch, "E374.MirrorCS", {"start": v(60.78, -15.2) * mm, "mid": v(60.76, -15.28) * mm, "end": v(60.72, -15.34) * mm});
            skArc(sketch, "E375.MirrorCS", {"start": v(42.03, -16.54) * mm, "mid": v(42.25, -16.59) * mm, "end": v(42.38, -16.4) * mm});
            skLineSegment(sketch, "E376.MirrorCS", {"start": v(42.03, -16.54) * mm, "end": v(40.83, -15.34) * mm});
            skLineSegment(sketch, "E377.MirrorCS", {"start": v(59.52, -16.54) * mm, "end": v(60.72, -15.34) * mm});
            skLineSegment(sketch, "E378.MirrorCS", {"start": v(42.38, -14.51) * mm, "end": v(44.02, -14.51) * mm});
            skLineSegment(sketch, "E379.MirrorCS", {"start": v(59.18, -14.51) * mm, "end": v(57.54, -14.51) * mm});
            skPoint(sketch, "E380.MirrorP", {"position": v(50.78, -16.31) * mm});
            skPoint(sketch, "E381.MirrorP", {"position": v(54.68, -20.21) * mm});
            skPoint(sketch, "E382.MirrorP", {"position": v(46.88, -20.21) * mm});
            skPoint(sketch, "E383.MirrorP", {"position": v(42.38, -16.89) * mm});
            skLineSegment(sketch, "E384.MirrorCS", {"start": v(57.54, -14.51) * mm, "end": v(54.68, -17.37) * mm});
            skLineSegment(sketch, "E385.MirrorCS", {"start": v(50.78, -20.21) * mm, "end": v(50.78, -2.89) * mm, "construction": true});
            skLineSegment(sketch, "E386.MirrorCS", {"start": v(47.94, -16.31) * mm, "end": v(45.08, -13.45) * mm});
            skLineSegment(sketch, "E387.MirrorCS", {"start": v(50.62, -16.31) * mm, "end": v(47.94, -16.31) * mm});
            skLineSegment(sketch, "E388.MirrorCS", {"start": v(40.78, -10.71) * mm, "end": v(40.78, -15.2) * mm});
            skPoint(sketch, "E389.MirrorP", {"position": v(59.18, -16.89) * mm});
            skLineSegment(sketch, "E390.MirrorCS", {"start": v(59.18, -16.4) * mm, "end": v(59.18, -14.51) * mm});
            skArc(sketch, "E391.MirrorC", {"start": v(48.68, -20.21) * mm, "mid": v(50.78, -18.11) * mm, "end": v(52.88, -20.21) * mm});
            skLineSegment(sketch, "E392.MirrorCS", {"start": v(46.88, -17.37) * mm, "end": v(46.88, -20.05) * mm});
            skLineSegment(sketch, "E393.MirrorCS", {"start": v(45.08, -13.45) * mm, "end": v(45.08, -11.81) * mm});
            skLineSegment(sketch, "E394.MirrorCS", {"start": v(54.68, -17.37) * mm, "end": v(54.68, -20.05) * mm});
            skLineSegment(sketch, "E395.MirrorCS", {"start": v(42.38, -16.4) * mm, "end": v(42.38, -14.51) * mm});
            skPoint(sketch, "E396.MirrorP", {"position": v(60.78, -15.29) * mm});
            skLineSegment(sketch, "E397.MirrorCS", {"start": v(56.48, -13.45) * mm, "end": v(56.48, -11.81) * mm});
            skLineSegment(sketch, "E398.MirrorCS", {"start": v(50.94, -16.31) * mm, "end": v(53.62, -16.31) * mm});
            skLineSegment(sketch, "E399.MirrorCS", {"start": v(44.02, -14.51) * mm, "end": v(46.88, -17.37) * mm});
            skPoint(sketch, "E400.MirrorP", {"position": v(40.78, -15.29) * mm});
            skLineSegment(sketch, "E401.MirrorCS", {"start": v(53.62, -16.31) * mm, "end": v(56.48, -13.45) * mm});
            skLineSegment(sketch, "E402.MirrorCS", {"start": v(60.78, -10.71) * mm, "end": v(60.78, -15.2) * mm});
            skLineSegment(sketch, "E403", {"start": v(45.08, -8.61) * mm, "end": v(45.08, -11.81) * mm});
            skLineSegment(sketch, "E404", {"start": v(56.48, -8.61) * mm, "end": v(56.48, -11.81) * mm});
            skLineSegment(sketch, "E405", {"start": v(40.78, -9.71) * mm, "end": v(40.78, -10.71) * mm});
            skLineSegment(sketch, "E406", {"start": v(60.78, -9.71) * mm, "end": v(60.78, -10.71) * mm});
            skLineSegment(sketch, "E407", {"start": v(46.88, -20.05) * mm, "end": v(46.88, -20.21) * mm});
            skLineSegment(sketch, "E408", {"start": v(54.68, -20.21) * mm, "end": v(54.68, -20.05) * mm});
            skLineSegment(sketch, "E409.MirrorCS", {"start": v(46.88, -40.37) * mm, "end": v(47.03, -40.21) * mm});
            skLineSegment(sketch, "E410.MirrorCS", {"start": v(47.03, -40.21) * mm, "end": v(46.88, -40.05) * mm});
            skLineSegment(sketch, "E411.MirrorCS", {"start": v(54.68, -20.21) * mm, "end": v(54.68, -20.37) * mm});
            skArc(sketch, "E412.MirrorCS", {"start": v(40.78, -45.22) * mm, "mid": v(40.8, -45.14) * mm, "end": v(40.83, -45.08) * mm});
            skArc(sketch, "E413.MirrorCS", {"start": v(45.9, -50.15) * mm, "mid": v(45.84, -50.2) * mm, "end": v(45.77, -50.21) * mm});
            skArc(sketch, "E414.MirrorCS", {"start": v(55.64, -50.15) * mm, "mid": v(55.7, -50.2) * mm, "end": v(55.78, -50.21) * mm});
            skArc(sketch, "E415.MirrorCS", {"start": v(42.03, -43.88) * mm, "mid": v(42.25, -43.84) * mm, "end": v(42.38, -44.02) * mm});
            skLineSegment(sketch, "E416.MirrorCS", {"start": v(50.62, -24.11) * mm, "end": v(50.78, -23.95) * mm});
            skLineSegment(sketch, "E417.MirrorCS", {"start": v(54.44, -48.95) * mm, "end": v(55.64, -50.15) * mm});
            skLineSegment(sketch, "E418.MirrorCS", {"start": v(42.03, -43.88) * mm, "end": v(40.83, -45.08) * mm});
            skArc(sketch, "E419.MirrorCS", {"start": v(60.78, -45.22) * mm, "mid": v(60.76, -45.14) * mm, "end": v(60.72, -45.08) * mm});
            skLineSegment(sketch, "E420.MirrorCS", {"start": v(50.78, -43.95) * mm, "end": v(50.94, -44.11) * mm});
            skArc(sketch, "E421.MirrorCS", {"start": v(40.78, -35.2) * mm, "mid": v(40.8, -35.28) * mm, "end": v(40.83, -35.35) * mm});
            skLineSegment(sketch, "E422.MirrorCS", {"start": v(46.88, -20.37) * mm, "end": v(46.88, -20.21) * mm});
            skArc(sketch, "E423.MirrorCS", {"start": v(40.78, -25.22) * mm, "mid": v(40.8, -25.14) * mm, "end": v(40.83, -25.08) * mm});
            skLineSegment(sketch, "E424.MirrorCS", {"start": v(59.52, -36.55) * mm, "end": v(60.72, -35.35) * mm});
            skArc(sketch, "E425.MirrorCS", {"start": v(60.78, -35.2) * mm, "mid": v(60.76, -35.28) * mm, "end": v(60.72, -35.35) * mm});
            skLineSegment(sketch, "E426.MirrorCS", {"start": v(54.52, -40.21) * mm, "end": v(54.68, -40.05) * mm});
            skArc(sketch, "E427.MirrorCS", {"start": v(60.78, -25.22) * mm, "mid": v(60.76, -25.14) * mm, "end": v(60.72, -25.08) * mm});
            skLineSegment(sketch, "E428.MirrorCS", {"start": v(59.52, -23.88) * mm, "end": v(60.72, -25.08) * mm});
            skArc(sketch, "E429.MirrorCS", {"start": v(46.97, -48.61) * mm, "mid": v(47.15, -48.74) * mm, "end": v(47.1, -48.95) * mm});
            skArc(sketch, "E430.MirrorCS", {"start": v(54.58, -48.61) * mm, "mid": v(54.4, -48.74) * mm, "end": v(54.44, -48.95) * mm});
            skLineSegment(sketch, "E431.MirrorCS", {"start": v(59.52, -43.88) * mm, "end": v(60.72, -45.08) * mm});
            skLineSegment(sketch, "E432.MirrorCS", {"start": v(45.08, -46.97) * mm, "end": v(45.08, -48.61) * mm});
            skArc(sketch, "E433.MirrorCS", {"start": v(42.03, -36.55) * mm, "mid": v(42.25, -36.59) * mm, "end": v(42.38, -36.4) * mm});
            skLineSegment(sketch, "E434.MirrorCS", {"start": v(50.62, -44.11) * mm, "end": v(50.78, -43.95) * mm});
            skLineSegment(sketch, "E435.MirrorCS", {"start": v(42.03, -23.88) * mm, "end": v(40.83, -25.08) * mm});
            skLineSegment(sketch, "E436.MirrorCS", {"start": v(42.38, -44.02) * mm, "end": v(42.38, -45.91) * mm});
            skLineSegment(sketch, "E437.MirrorCS", {"start": v(45.08, -48.61) * mm, "end": v(46.97, -48.61) * mm});
            skArc(sketch, "E438.MirrorCS", {"start": v(59.52, -43.88) * mm, "mid": v(59.3, -43.84) * mm, "end": v(59.18, -44.02) * mm});
            skLineSegment(sketch, "E439.MirrorCS", {"start": v(42.03, -36.55) * mm, "end": v(40.83, -35.35) * mm});
            skLineSegment(sketch, "E440.MirrorCS", {"start": v(42.38, -45.91) * mm, "end": v(44.02, -45.91) * mm});
            skLineSegment(sketch, "E441.MirrorCS", {"start": v(50.62, -44.11) * mm, "end": v(47.94, -44.11) * mm});
            skArc(sketch, "E442.MirrorCS", {"start": v(59.52, -36.55) * mm, "mid": v(59.3, -36.59) * mm, "end": v(59.18, -36.4) * mm});
            skLineSegment(sketch, "E443.MirrorCS", {"start": v(50.78, -36.47) * mm, "end": v(50.94, -36.31) * mm});
            skLineSegment(sketch, "E444.MirrorCS", {"start": v(59.18, -24.02) * mm, "end": v(59.18, -25.91) * mm});
            skLineSegment(sketch, "E445.MirrorCS", {"start": v(47.1, -48.95) * mm, "end": v(45.9, -50.15) * mm});
            skArc(sketch, "E446.MirrorCS", {"start": v(41.28, -50.21) * mm, "mid": v(40.92, -50.07) * mm, "end": v(40.78, -49.71) * mm});
            skLineSegment(sketch, "E447.MirrorCS", {"start": v(50.78, -23.95) * mm, "end": v(50.94, -24.11) * mm});
            skArc(sketch, "E448.MirrorCS", {"start": v(42.03, -23.88) * mm, "mid": v(42.25, -23.83) * mm, "end": v(42.38, -24.02) * mm});
            skArc(sketch, "E449.MirrorCS", {"start": v(59.52, -23.88) * mm, "mid": v(59.3, -23.83) * mm, "end": v(59.18, -24.02) * mm});
            skLineSegment(sketch, "E450.MirrorCS", {"start": v(54.68, -40.37) * mm, "end": v(54.52, -40.21) * mm});
            skLineSegment(sketch, "E451.MirrorCS", {"start": v(60.78, -30.71) * mm, "end": v(60.78, -29.71) * mm});
            skLineSegment(sketch, "E452.MirrorCS", {"start": v(56.48, -48.61) * mm, "end": v(54.58, -48.61) * mm});
            skLineSegment(sketch, "E453.MirrorCS", {"start": v(54.68, -43.05) * mm, "end": v(54.68, -40.37) * mm});
            skLineSegment(sketch, "E454.MirrorCS", {"start": v(50.62, -36.31) * mm, "end": v(47.94, -36.31) * mm});
            skLineSegment(sketch, "E455.MirrorCS", {"start": v(45.08, -26.97) * mm, "end": v(45.08, -28.61) * mm});
            skLineSegment(sketch, "E456.MirrorCS", {"start": v(59.18, -34.51) * mm, "end": v(57.54, -34.51) * mm});
            skLineSegment(sketch, "E457.MirrorCS", {"start": v(50.94, -44.11) * mm, "end": v(53.62, -44.11) * mm});
            skLineSegment(sketch, "E458.MirrorCS", {"start": v(59.18, -25.91) * mm, "end": v(57.54, -25.91) * mm});
            skLineSegment(sketch, "E459.MirrorCS", {"start": v(50.94, -24.11) * mm, "end": v(53.62, -24.11) * mm});
            skLineSegment(sketch, "E460.MirrorCS", {"start": v(54.68, -37.37) * mm, "end": v(54.68, -40.05) * mm});
            skLineSegment(sketch, "E461.MirrorCS", {"start": v(56.48, -26.97) * mm, "end": v(56.48, -28.61) * mm});
            skLineSegment(sketch, "E462.MirrorCS", {"start": v(42.38, -34.51) * mm, "end": v(44.02, -34.51) * mm});
            skLineSegment(sketch, "E463.MirrorCS", {"start": v(40.78, -30.71) * mm, "end": v(40.78, -29.71) * mm});
            skLineSegment(sketch, "E464.MirrorCS", {"start": v(56.48, -33.45) * mm, "end": v(56.48, -31.81) * mm});
            skLineSegment(sketch, "E465.MirrorCS", {"start": v(50.62, -24.11) * mm, "end": v(47.94, -24.11) * mm});
            skLineSegment(sketch, "E466.MirrorCS", {"start": v(45.08, -33.45) * mm, "end": v(45.08, -31.81) * mm});
            skLineSegment(sketch, "E467.MirrorCS", {"start": v(50.62, -36.31) * mm, "end": v(50.78, -36.47) * mm});
            skLineSegment(sketch, "E468.MirrorCS", {"start": v(59.18, -36.4) * mm, "end": v(59.18, -34.51) * mm});
            skLineSegment(sketch, "E469.MirrorCS", {"start": v(46.88, -37.37) * mm, "end": v(46.88, -40.05) * mm});
            skLineSegment(sketch, "E470.MirrorCS", {"start": v(46.88, -43.05) * mm, "end": v(46.88, -40.37) * mm});
            skArc(sketch, "E471.MirrorCS", {"start": v(60.28, -50.21) * mm, "mid": v(60.63, -50.07) * mm, "end": v(60.78, -49.71) * mm});
            skLineSegment(sketch, "E472.MirrorCS", {"start": v(54.68, -23.05) * mm, "end": v(54.68, -20.37) * mm});
            skLineSegment(sketch, "E473.MirrorCS", {"start": v(46.88, -23.05) * mm, "end": v(46.88, -20.37) * mm});
            skLineSegment(sketch, "E474.MirrorCS", {"start": v(56.48, -46.97) * mm, "end": v(56.48, -48.61) * mm});
            skLineSegment(sketch, "E475.MirrorCS", {"start": v(50.94, -36.31) * mm, "end": v(53.62, -36.31) * mm});
            skLineSegment(sketch, "E476.MirrorCS", {"start": v(42.38, -24.02) * mm, "end": v(42.38, -25.91) * mm});
            skLineSegment(sketch, "E477.MirrorCS", {"start": v(42.38, -36.4) * mm, "end": v(42.38, -34.51) * mm});
            skLineSegment(sketch, "E478.MirrorCS", {"start": v(42.38, -25.91) * mm, "end": v(44.02, -25.91) * mm});
            skLineSegment(sketch, "E479.MirrorCS", {"start": v(59.18, -45.91) * mm, "end": v(57.54, -45.91) * mm});
            skLineSegment(sketch, "E480.MirrorCS", {"start": v(59.18, -44.02) * mm, "end": v(59.18, -45.91) * mm});
            skPoint(sketch, "E481.MirrorP", {"position": v(46.88, -40.21) * mm});
            skLineSegment(sketch, "E482.MirrorCS", {"start": v(50.78, -20.21) * mm, "end": v(50.78, -37.53) * mm, "construction": true});
            skPoint(sketch, "E483.MirrorP", {"position": v(40.78, -30.21) * mm});
            skPoint(sketch, "E484.MirrorP", {"position": v(45.85, -50.21) * mm});
            skPoint(sketch, "E485.MirrorP", {"position": v(54.68, -40.21) * mm});
            skLineSegment(sketch, "E486.MirrorCS", {"start": v(44.02, -45.91) * mm, "end": v(46.88, -43.05) * mm});
            skLineSegment(sketch, "E487.MirrorCS", {"start": v(45.77, -50.21) * mm, "end": v(41.28, -50.21) * mm});
            skLineSegment(sketch, "E488.MirrorCS", {"start": v(40.78, -49.71) * mm, "end": v(40.78, -45.22) * mm});
            skPoint(sketch, "E489.MirrorP", {"position": v(50.78, -24.11) * mm});
            skLineSegment(sketch, "E490.MirrorCS", {"start": v(47.94, -44.11) * mm, "end": v(45.08, -46.97) * mm});
            skPoint(sketch, "E491.MirrorP", {"position": v(50.78, -44.11) * mm});
            skPoint(sketch, "E492.MirrorP", {"position": v(50.78, -36.31) * mm});
            skPoint(sketch, "E493.MirrorP", {"position": v(60.78, -50.21) * mm});
            skPoint(sketch, "E494.MirrorP", {"position": v(59.18, -43.54) * mm});
            skLineSegment(sketch, "E495.MirrorCS", {"start": v(60.78, -49.71) * mm, "end": v(60.78, -45.22) * mm});
            skLineSegment(sketch, "E496.MirrorCS", {"start": v(53.62, -36.31) * mm, "end": v(56.48, -33.45) * mm});
            skPoint(sketch, "E497.MirrorP", {"position": v(59.18, -23.54) * mm});
            skLineSegment(sketch, "E498.MirrorCS", {"start": v(60.78, -29.71) * mm, "end": v(60.78, -25.22) * mm});
            skLineSegment(sketch, "E499.MirrorCS", {"start": v(47.94, -36.31) * mm, "end": v(45.08, -33.45) * mm});
            skPoint(sketch, "E500.MirrorP", {"position": v(60.78, -35.29) * mm});
            skLineSegment(sketch, "E501.MirrorCS", {"start": v(50.78, -40.21) * mm, "end": v(23.4, -40.21) * mm, "construction": true});
            skLineSegment(sketch, "E502.MirrorCS", {"start": v(57.54, -34.51) * mm, "end": v(54.68, -37.37) * mm});
            skPoint(sketch, "E503.MirrorP", {"position": v(60.78, -45.14) * mm});
            skPoint(sketch, "E504.MirrorP", {"position": v(42.38, -36.89) * mm});
            skPoint(sketch, "E505.MirrorP", {"position": v(40.78, -45.14) * mm});
            skPoint(sketch, "E506.MirrorP", {"position": v(55.7, -50.21) * mm});
            skLineSegment(sketch, "E507.MirrorCS", {"start": v(40.78, -29.71) * mm, "end": v(40.78, -25.22) * mm});
            skCircle(sketch, "E508.MirrorC", {"center": v(50.78, -40.21) * mm, "radius": 2.1 * mm});
            skPoint(sketch, "E509.MirrorP", {"position": v(47.45, -48.61) * mm});
            skPoint(sketch, "E510.MirrorP", {"position": v(60.78, -25.14) * mm});
            skPoint(sketch, "E511.MirrorP", {"position": v(40.78, -35.29) * mm});
            skLineSegment(sketch, "E512.MirrorCS", {"start": v(60.78, -30.71) * mm, "end": v(60.78, -35.2) * mm});
            skPoint(sketch, "E513.MirrorP", {"position": v(54.1, -48.61) * mm});
            skLineSegment(sketch, "E514.MirrorCS", {"start": v(55.78, -50.21) * mm, "end": v(60.28, -50.21) * mm});
            skLineSegment(sketch, "E515.MirrorCS", {"start": v(50.78, -40.21) * mm, "end": v(50.78, -22.9) * mm, "construction": true});
            skPoint(sketch, "E516.MirrorP", {"position": v(59.18, -36.89) * mm});
            skLineSegment(sketch, "E517.MirrorCS", {"start": v(44.02, -25.91) * mm, "end": v(46.88, -23.05) * mm});
            skLineSegment(sketch, "E518.MirrorCS", {"start": v(57.54, -45.91) * mm, "end": v(54.68, -43.05) * mm});
            skLineSegment(sketch, "E519.MirrorCS", {"start": v(45.08, -31.81) * mm, "end": v(45.08, -28.61) * mm});
            skPoint(sketch, "E520.MirrorP", {"position": v(40.78, -50.21) * mm});
            skPoint(sketch, "E521.MirrorP", {"position": v(40.78, -25.14) * mm});
            skLineSegment(sketch, "E522.MirrorCS", {"start": v(40.78, -30.71) * mm, "end": v(40.78, -35.2) * mm});
            skLineSegment(sketch, "E523.MirrorCS", {"start": v(53.62, -24.11) * mm, "end": v(56.48, -26.97) * mm});
            skPoint(sketch, "E524.MirrorP", {"position": v(42.38, -23.54) * mm});
            skLineSegment(sketch, "E525.MirrorCS", {"start": v(53.62, -44.11) * mm, "end": v(56.48, -46.97) * mm});
            skLineSegment(sketch, "E526.MirrorCS", {"start": v(50.78, -40.21) * mm, "end": v(50.78, -57.53) * mm, "construction": true});
            skLineSegment(sketch, "E527.MirrorCS", {"start": v(44.02, -34.51) * mm, "end": v(46.88, -37.37) * mm});
            skPoint(sketch, "E528.MirrorP", {"position": v(42.38, -43.54) * mm});
            skArc(sketch, "E529.MirrorCS", {"start": v(48.68, -20.21) * mm, "mid": v(50.78, -22.31) * mm, "end": v(52.88, -20.21) * mm});
            skLineSegment(sketch, "E530.MirrorCS", {"start": v(56.48, -31.81) * mm, "end": v(56.48, -28.61) * mm});
            skLineSegment(sketch, "E531.MirrorCS", {"start": v(57.54, -25.91) * mm, "end": v(54.68, -23.05) * mm});
            skLineSegment(sketch, "E532.MirrorCS", {"start": v(47.94, -24.11) * mm, "end": v(45.08, -26.97) * mm});
            skLineSegment(sketch, "E533.trimOffspring", {"start": v(46.88, -20.21) * mm, "end": v(23.4, -20.21) * mm, "construction": true});
            skSolve(sketch);
        }
        {
            var Q0;
            Q0=qCreatedBy(makeId("Front.planeOp"),FACE);
            var sketch = newSketch(context, id + "F3", { "sketchPlane" : qUnion([Q0])});
            skLineSegment(sketch, "E534", {"start": v(75.62, 3.7) * mm, "end": v(72.94, 3.7) * mm});
            skLineSegment(sketch, "E535", {"start": v(72.94, 3.7) * mm, "end": v(70.08, 6.55) * mm});
            skLineSegment(sketch, "E536", {"start": v(70.08, 6.55) * mm, "end": v(70.08, 8.2) * mm});
            skLineSegment(sketch, "E537", {"start": v(70.77, 9.8) * mm, "end": v(66.28, 9.8) * mm});
            skLineSegment(sketch, "E538", {"start": v(65.78, 9.3) * mm, "end": v(65.78, 4.8) * mm});
            skLineSegment(sketch, "E539", {"start": v(67.38, 3.6) * mm, "end": v(67.38, 5.5) * mm});
            skLineSegment(sketch, "E540", {"start": v(67.38, 5.5) * mm, "end": v(69.02, 5.5) * mm});
            skLineSegment(sketch, "E541", {"start": v(69.02, 5.5) * mm, "end": v(71.88, 2.63) * mm});
            skLineSegment(sketch, "E542", {"start": v(71.88, 2.63) * mm, "end": v(71.88, -0.05) * mm});
            skLineSegment(sketch, "E543", {"start": v(75.78, -0.2) * mm, "end": v(75.78, 17.11) * mm, "construction": true});
            skLineSegment(sketch, "E544", {"start": v(75.78, -0.2) * mm, "end": v(48.4, -0.2) * mm, "construction": true});
            skPoint(sketch, "E545.visualSharp", {"position": v(65.78, 9.8) * mm});
            skArc(sketch, "E545.filletArc", {"start": v(66.28, 9.8) * mm, "mid": v(65.92, 9.64) * mm, "end": v(65.78, 9.3) * mm});
            skLineSegment(sketch, "E546.filletArc", {"start": v(-34.22, 14.52) * mm, "end": v(-34.22, 14.52) * mm});
            skLineSegment(sketch, "E547", {"start": v(70.08, 8.2) * mm, "end": v(71.97, 8.2) * mm});
            skLineSegment(sketch, "E548", {"start": v(72.1, 8.53) * mm, "end": v(70.9, 9.73) * mm});
            skLineSegment(sketch, "E549", {"start": v(67.03, 3.46) * mm, "end": v(65.83, 4.66) * mm});
            skPoint(sketch, "E550.visualSharp", {"position": v(67.38, 3.12) * mm});
            skArc(sketch, "E550.filletArc", {"start": v(67.03, 3.46) * mm, "mid": v(67.25, 3.41) * mm, "end": v(67.38, 3.6) * mm});
            skPoint(sketch, "E551.visualSharp", {"position": v(72.45, 8.2) * mm});
            skArc(sketch, "E551.filletArc", {"start": v(71.97, 8.2) * mm, "mid": v(72.15, 8.31) * mm, "end": v(72.1, 8.53) * mm});
            skPoint(sketch, "E552.visualSharp", {"position": v(70.85, 9.8) * mm});
            skArc(sketch, "E552.filletArc", {"start": v(70.9, 9.73) * mm, "mid": v(70.84, 9.78) * mm, "end": v(70.77, 9.8) * mm});
            skPoint(sketch, "E553.visualSharp", {"position": v(65.78, 4.72) * mm});
            skArc(sketch, "E553.filletArc", {"start": v(65.78, 4.8) * mm, "mid": v(65.8, 4.72) * mm, "end": v(65.83, 4.66) * mm});
            skArc(sketch, "E554.MirrorCS", {"start": v(84.52, 3.46) * mm, "mid": v(84.3, 3.41) * mm, "end": v(84.18, 3.6) * mm});
            skArc(sketch, "E555.MirrorCS", {"start": v(85.78, 4.8) * mm, "mid": v(85.76, 4.72) * mm, "end": v(85.72, 4.66) * mm});
            skArc(sketch, "E556.MirrorCS", {"start": v(80.64, 9.73) * mm, "mid": v(80.7, 9.78) * mm, "end": v(80.78, 9.8) * mm});
            skArc(sketch, "E557.MirrorCS", {"start": v(79.58, 8.2) * mm, "mid": v(79.4, 8.31) * mm, "end": v(79.44, 8.53) * mm});
            skArc(sketch, "E558.MirrorCS", {"start": v(85.28, 9.8) * mm, "mid": v(85.63, 9.64) * mm, "end": v(85.78, 9.3) * mm});
            skPoint(sketch, "E559.MirrorP", {"position": v(84.18, 3.12) * mm});
            skLineSegment(sketch, "E560.MirrorCS", {"start": v(-14.22, 14.52) * mm, "end": v(-14.22, 14.52) * mm});
            skLineSegment(sketch, "E561.MirrorCS", {"start": v(79.44, 8.53) * mm, "end": v(80.64, 9.73) * mm});
            skLineSegment(sketch, "E562.MirrorCS", {"start": v(82.54, 5.5) * mm, "end": v(79.68, 2.63) * mm});
            skLineSegment(sketch, "E563.MirrorCS", {"start": v(79.68, 2.63) * mm, "end": v(79.68, -0.05) * mm});
            skLineSegment(sketch, "E564.MirrorCS", {"start": v(85.78, 9.3) * mm, "end": v(85.78, 4.8) * mm});
            skLineSegment(sketch, "E565.MirrorCS", {"start": v(75.94, 3.7) * mm, "end": v(78.62, 3.7) * mm});
            skPoint(sketch, "E566.MirrorP", {"position": v(85.78, 4.72) * mm});
            skLineSegment(sketch, "E567.MirrorCS", {"start": v(84.18, 3.6) * mm, "end": v(84.18, 5.5) * mm});
            skLineSegment(sketch, "E568.MirrorCS", {"start": v(81.48, 8.2) * mm, "end": v(79.58, 8.2) * mm});
            skLineSegment(sketch, "E569.MirrorCS", {"start": v(78.62, 3.7) * mm, "end": v(81.48, 6.55) * mm});
            skPoint(sketch, "E570.MirrorP", {"position": v(79.1, 8.2) * mm});
            skLineSegment(sketch, "E571.MirrorCS", {"start": v(84.18, 5.5) * mm, "end": v(82.54, 5.5) * mm});
            skPoint(sketch, "E572.MirrorP", {"position": v(80.7, 9.8) * mm});
            skLineSegment(sketch, "E573.MirrorCS", {"start": v(84.52, 3.46) * mm, "end": v(85.72, 4.66) * mm});
            skLineSegment(sketch, "E574.MirrorCS", {"start": v(81.48, 6.55) * mm, "end": v(81.48, 8.2) * mm});
            skLineSegment(sketch, "E575.MirrorCS", {"start": v(80.78, 9.8) * mm, "end": v(85.28, 9.8) * mm});
            skPoint(sketch, "E576.MirrorP", {"position": v(85.78, 9.8) * mm});
            skArc(sketch, "E577.MirrorCS", {"start": v(67.03, -3.88) * mm, "mid": v(67.25, -3.83) * mm, "end": v(67.38, -4.02) * mm});
            skArc(sketch, "E578.MirrorCS", {"start": v(65.78, -5.22) * mm, "mid": v(65.8, -5.14) * mm, "end": v(65.83, -5.08) * mm});
            skArc(sketch, "E579.MirrorCS", {"start": v(85.78, -5.22) * mm, "mid": v(85.76, -5.14) * mm, "end": v(85.72, -5.08) * mm});
            skArc(sketch, "E580.MirrorCS", {"start": v(84.52, -3.88) * mm, "mid": v(84.3, -3.83) * mm, "end": v(84.18, -4.02) * mm});
            skLineSegment(sketch, "E581.MirrorCS", {"start": v(67.03, -3.88) * mm, "end": v(65.83, -5.08) * mm});
            skLineSegment(sketch, "E582.MirrorCS", {"start": v(84.18, -5.9) * mm, "end": v(82.54, -5.9) * mm});
            skLineSegment(sketch, "E583.MirrorCS", {"start": v(84.52, -3.88) * mm, "end": v(85.72, -5.08) * mm});
            skLineSegment(sketch, "E584.MirrorCS", {"start": v(75.78, -0.2) * mm, "end": v(75.78, -17.53) * mm, "construction": true});
            skLineSegment(sketch, "E585.MirrorCS", {"start": v(81.48, -6.97) * mm, "end": v(81.48, -8.61) * mm});
            skLineSegment(sketch, "E586.MirrorCS", {"start": v(71.88, -3.05) * mm, "end": v(71.88, -0.37) * mm});
            skLineSegment(sketch, "E587.MirrorCS", {"start": v(78.62, -4.11) * mm, "end": v(81.48, -6.97) * mm});
            skPoint(sketch, "E588.MirrorP", {"position": v(67.38, -3.53) * mm});
            skLineSegment(sketch, "E589.MirrorCS", {"start": v(75.94, -4.11) * mm, "end": v(78.62, -4.11) * mm});
            skLineSegment(sketch, "E590.MirrorCS", {"start": v(72.94, -4.11) * mm, "end": v(70.08, -6.97) * mm});
            skLineSegment(sketch, "E591.MirrorCS", {"start": v(82.54, -5.9) * mm, "end": v(79.68, -3.05) * mm});
            skLineSegment(sketch, "E592.MirrorCS", {"start": v(67.38, -5.9) * mm, "end": v(69.02, -5.9) * mm});
            skLineSegment(sketch, "E593.MirrorCS", {"start": v(85.78, -9.71) * mm, "end": v(85.78, -5.22) * mm});
            skLineSegment(sketch, "E594.MirrorCS", {"start": v(65.78, -9.71) * mm, "end": v(65.78, -5.22) * mm});
            skLineSegment(sketch, "E595.MirrorCS", {"start": v(67.38, -4.02) * mm, "end": v(67.38, -5.9) * mm});
            skLineSegment(sketch, "E596.MirrorCS", {"start": v(84.18, -4.02) * mm, "end": v(84.18, -5.9) * mm});
            skPoint(sketch, "E597.MirrorP", {"position": v(84.18, -3.53) * mm});
            skPoint(sketch, "E598.MirrorP", {"position": v(85.78, -5.13) * mm});
            skLineSegment(sketch, "E599.MirrorCS", {"start": v(70.08, -6.97) * mm, "end": v(70.08, -8.61) * mm});
            skLineSegment(sketch, "E600.MirrorCS", {"start": v(69.02, -5.9) * mm, "end": v(71.88, -3.05) * mm});
            skLineSegment(sketch, "E601.MirrorCS", {"start": v(75.62, -4.11) * mm, "end": v(72.94, -4.11) * mm});
            skLineSegment(sketch, "E602.MirrorCS", {"start": v(79.68, -3.05) * mm, "end": v(79.68, -0.37) * mm});
            skLineSegment(sketch, "E603.MirrorCS", {"start": v(-34.22, 5.07) * mm, "end": v(-34.22, 5.07) * mm});
            skPoint(sketch, "E604.MirrorP", {"position": v(65.78, -5.13) * mm});
            skLineSegment(sketch, "E605.MirrorCS", {"start": v(-14.22, 5.07) * mm, "end": v(-14.22, 5.07) * mm});
            skPoint(sketch, "E606.MirrorP", {"position": v(65.78, -10.21) * mm});
            skCircle(sketch, "E607", {"center": v(75.78, -0.2) * mm, "radius": 2.1 * mm});
            skLineSegment(sketch, "E608", {"start": v(75.62, 3.7) * mm, "end": v(75.78, 3.53) * mm});
            skLineSegment(sketch, "E609", {"start": v(75.78, 3.53) * mm, "end": v(75.94, 3.7) * mm});
            skPoint(sketch, "E610.orphan", {"position": v(75.78, 3.7) * mm});
            skLineSegment(sketch, "E611.MirrorCS", {"start": v(75.62, -4.11) * mm, "end": v(75.78, -3.95) * mm});
            skLineSegment(sketch, "E612.MirrorCS", {"start": v(75.78, -3.95) * mm, "end": v(75.94, -4.11) * mm});
            skLineSegment(sketch, "E613", {"start": v(71.88, -0.05) * mm, "end": v(72.03, -0.2) * mm});
            skLineSegment(sketch, "E614", {"start": v(72.03, -0.2) * mm, "end": v(71.88, -0.37) * mm});
            skPoint(sketch, "E615.orphan", {"position": v(71.88, -0.2) * mm});
            skLineSegment(sketch, "E616.MirrorCS", {"start": v(79.52, -0.2) * mm, "end": v(79.68, -0.37) * mm});
            skLineSegment(sketch, "E617.MirrorCS", {"start": v(79.68, -0.05) * mm, "end": v(79.52, -0.2) * mm});
            skPoint(sketch, "E618.orphan", {"position": v(79.68, -0.2) * mm});
            skPoint(sketch, "E619.orphan", {"position": v(75.78, -4.11) * mm});
            skArc(sketch, "E620.MirrorCS", {"start": v(85.78, -25.22) * mm, "mid": v(85.76, -25.14) * mm, "end": v(85.72, -25.08) * mm});
            skLineSegment(sketch, "E621.MirrorCS", {"start": v(75.62, -24.11) * mm, "end": v(75.78, -23.95) * mm});
            skLineSegment(sketch, "E622.MirrorCS", {"start": v(75.62, -16.31) * mm, "end": v(75.78, -16.47) * mm});
            skLineSegment(sketch, "E623.MirrorCS", {"start": v(75.78, -23.95) * mm, "end": v(75.94, -24.11) * mm});
            skArc(sketch, "E624.MirrorCS", {"start": v(65.78, -25.22) * mm, "mid": v(65.8, -25.14) * mm, "end": v(65.83, -25.08) * mm});
            skArc(sketch, "E625.MirrorCS", {"start": v(84.52, -16.54) * mm, "mid": v(84.3, -16.59) * mm, "end": v(84.18, -16.4) * mm});
            skLineSegment(sketch, "E626.MirrorCS", {"start": v(71.88, -20.37) * mm, "end": v(72.03, -20.21) * mm});
            skLineSegment(sketch, "E627.MirrorCS", {"start": v(79.68, -20.37) * mm, "end": v(79.52, -20.21) * mm});
            skArc(sketch, "E628.MirrorCS", {"start": v(65.78, -15.2) * mm, "mid": v(65.8, -15.28) * mm, "end": v(65.83, -15.34) * mm});
            skLineSegment(sketch, "E629.MirrorCS", {"start": v(75.78, -16.47) * mm, "end": v(75.94, -16.31) * mm});
            skLineSegment(sketch, "E630.MirrorCS", {"start": v(72.03, -20.21) * mm, "end": v(71.88, -20.05) * mm});
            skArc(sketch, "E631.MirrorCS", {"start": v(85.78, -15.2) * mm, "mid": v(85.76, -15.28) * mm, "end": v(85.72, -15.34) * mm});
            skLineSegment(sketch, "E632.MirrorCS", {"start": v(79.52, -20.21) * mm, "end": v(79.68, -20.05) * mm});
            skArc(sketch, "E633.MirrorCS", {"start": v(67.03, -16.54) * mm, "mid": v(67.25, -16.59) * mm, "end": v(67.38, -16.4) * mm});
            skLineSegment(sketch, "E634.MirrorCS", {"start": v(67.03, -16.54) * mm, "end": v(65.83, -15.34) * mm});
            skLineSegment(sketch, "E635.MirrorCS", {"start": v(84.52, -16.54) * mm, "end": v(85.72, -15.34) * mm});
            skArc(sketch, "E636.MirrorCS", {"start": v(67.03, -23.88) * mm, "mid": v(67.25, -23.83) * mm, "end": v(67.38, -24.02) * mm});
            skLineSegment(sketch, "E637.MirrorCS", {"start": v(67.03, -23.88) * mm, "end": v(65.83, -25.08) * mm});
            skLineSegment(sketch, "E638.MirrorCS", {"start": v(84.18, -25.91) * mm, "end": v(82.54, -25.91) * mm});
            skLineSegment(sketch, "E639.MirrorCS", {"start": v(67.38, -14.51) * mm, "end": v(69.02, -14.51) * mm});
            skLineSegment(sketch, "E640.MirrorCS", {"start": v(81.48, -26.97) * mm, "end": v(81.48, -28.61) * mm});
            skArc(sketch, "E641.MirrorCS", {"start": v(84.52, -23.88) * mm, "mid": v(84.3, -23.83) * mm, "end": v(84.18, -24.02) * mm});
            skLineSegment(sketch, "E642.MirrorCS", {"start": v(67.38, -25.91) * mm, "end": v(69.02, -25.91) * mm});
            skLineSegment(sketch, "E643.MirrorCS", {"start": v(70.08, -26.97) * mm, "end": v(70.08, -28.61) * mm});
            skLineSegment(sketch, "E644.MirrorCS", {"start": v(84.52, -23.88) * mm, "end": v(85.72, -25.08) * mm});
            skLineSegment(sketch, "E645.MirrorCS", {"start": v(84.18, -14.51) * mm, "end": v(82.54, -14.51) * mm});
            skLineSegment(sketch, "E646.MirrorCS", {"start": v(67.38, -24.02) * mm, "end": v(67.38, -25.91) * mm});
            skPoint(sketch, "E647.MirrorP", {"position": v(75.78, -24.11) * mm});
            skPoint(sketch, "E648.MirrorP", {"position": v(75.78, -16.31) * mm});
            skPoint(sketch, "E649.MirrorP", {"position": v(79.68, -20.21) * mm});
            skPoint(sketch, "E650.MirrorP", {"position": v(71.88, -20.21) * mm});
            skPoint(sketch, "E651.MirrorP", {"position": v(65.78, -30.21) * mm});
            skPoint(sketch, "E652.MirrorP", {"position": v(84.18, -23.54) * mm});
            skPoint(sketch, "E653.MirrorP", {"position": v(65.78, -25.14) * mm});
            skPoint(sketch, "E654.MirrorP", {"position": v(67.38, -16.89) * mm});
            skLineSegment(sketch, "E655.MirrorCS", {"start": v(82.54, -14.51) * mm, "end": v(79.68, -17.37) * mm});
            skLineSegment(sketch, "E656.MirrorCS", {"start": v(65.78, -29.71) * mm, "end": v(65.78, -25.22) * mm});
            skLineSegment(sketch, "E657.MirrorCS", {"start": v(85.78, -29.71) * mm, "end": v(85.78, -25.22) * mm});
            skLineSegment(sketch, "E658.MirrorCS", {"start": v(75.78, -20.21) * mm, "end": v(75.78, -2.89) * mm, "construction": true});
            skLineSegment(sketch, "E659.MirrorCS", {"start": v(78.62, -24.11) * mm, "end": v(81.48, -26.97) * mm});
            skLineSegment(sketch, "E660.MirrorCS", {"start": v(72.94, -16.31) * mm, "end": v(70.08, -13.45) * mm});
            skLineSegment(sketch, "E661.MirrorCS", {"start": v(75.62, -16.31) * mm, "end": v(72.94, -16.31) * mm});
            skLineSegment(sketch, "E662.MirrorCS", {"start": v(65.78, -10.71) * mm, "end": v(65.78, -15.2) * mm});
            skPoint(sketch, "E663.MirrorP", {"position": v(85.78, -30.21) * mm});
            skLineSegment(sketch, "E664.MirrorCS", {"start": v(75.78, -20.21) * mm, "end": v(75.78, -37.53) * mm, "construction": true});
            skLineSegment(sketch, "E665.MirrorCS", {"start": v(82.54, -25.91) * mm, "end": v(79.68, -23.05) * mm});
            skPoint(sketch, "E666.MirrorP", {"position": v(84.18, -16.89) * mm});
            skLineSegment(sketch, "E667.MirrorCS", {"start": v(75.94, -24.11) * mm, "end": v(78.62, -24.11) * mm});
            skLineSegment(sketch, "E668.MirrorCS", {"start": v(84.18, -16.4) * mm, "end": v(84.18, -14.51) * mm});
            skCircle(sketch, "E669.MirrorC", {"center": v(75.78, -20.21) * mm, "radius": 2.1 * mm});
            skPoint(sketch, "E670.MirrorP", {"position": v(67.38, -23.54) * mm});
            skLineSegment(sketch, "E671.MirrorCS", {"start": v(71.88, -17.37) * mm, "end": v(71.88, -20.05) * mm});
            skLineSegment(sketch, "E672.MirrorCS", {"start": v(75.78, -20.21) * mm, "end": v(48.4, -20.21) * mm, "construction": true});
            skLineSegment(sketch, "E673.MirrorCS", {"start": v(70.08, -13.45) * mm, "end": v(70.08, -11.81) * mm});
            skLineSegment(sketch, "E674.MirrorCS", {"start": v(79.68, -17.37) * mm, "end": v(79.68, -20.05) * mm});
            skLineSegment(sketch, "E675.MirrorCS", {"start": v(67.38, -16.4) * mm, "end": v(67.38, -14.51) * mm});
            skPoint(sketch, "E676.MirrorP", {"position": v(85.78, -15.29) * mm});
            skLineSegment(sketch, "E677.MirrorCS", {"start": v(81.48, -13.45) * mm, "end": v(81.48, -11.81) * mm});
            skLineSegment(sketch, "E678.MirrorCS", {"start": v(75.94, -16.31) * mm, "end": v(78.62, -16.31) * mm});
            skLineSegment(sketch, "E679.MirrorCS", {"start": v(79.68, -23.05) * mm, "end": v(79.68, -20.37) * mm});
            skLineSegment(sketch, "E680.MirrorCS", {"start": v(69.02, -14.51) * mm, "end": v(71.88, -17.37) * mm});
            skPoint(sketch, "E681.MirrorP", {"position": v(85.78, -25.14) * mm});
            skPoint(sketch, "E682.MirrorP", {"position": v(65.78, -15.29) * mm});
            skLineSegment(sketch, "E683.MirrorCS", {"start": v(84.18, -24.02) * mm, "end": v(84.18, -25.91) * mm});
            skLineSegment(sketch, "E684.MirrorCS", {"start": v(69.02, -25.91) * mm, "end": v(71.88, -23.05) * mm});
            skLineSegment(sketch, "E685.MirrorCS", {"start": v(78.62, -16.31) * mm, "end": v(81.48, -13.45) * mm});
            skLineSegment(sketch, "E686.MirrorCS", {"start": v(72.94, -24.11) * mm, "end": v(70.08, -26.97) * mm});
            skLineSegment(sketch, "E687.MirrorCS", {"start": v(75.62, -24.11) * mm, "end": v(72.94, -24.11) * mm});
            skLineSegment(sketch, "E688.MirrorCS", {"start": v(85.78, -10.71) * mm, "end": v(85.78, -15.2) * mm});
            skLineSegment(sketch, "E689.MirrorCS", {"start": v(71.88, -23.05) * mm, "end": v(71.88, -20.37) * mm});
            skLineSegment(sketch, "E690", {"start": v(70.08, -8.61) * mm, "end": v(70.08, -11.81) * mm});
            skLineSegment(sketch, "E691", {"start": v(81.48, -8.61) * mm, "end": v(81.48, -11.81) * mm});
            skLineSegment(sketch, "E692", {"start": v(65.78, -9.71) * mm, "end": v(65.78, -10.71) * mm});
            skLineSegment(sketch, "E693", {"start": v(85.78, -9.71) * mm, "end": v(85.78, -10.71) * mm});
            skLineSegment(sketch, "E694.MirrorCS", {"start": v(79.52, -60.21) * mm, "end": v(79.68, -60.05) * mm});
            skLineSegment(sketch, "E695.MirrorCS", {"start": v(79.68, -60.37) * mm, "end": v(79.52, -60.21) * mm});
            skArc(sketch, "E696.MirrorCS", {"start": v(70.9, -70.16) * mm, "mid": v(70.84, -70.2) * mm, "end": v(70.77, -70.21) * mm});
            skLineSegment(sketch, "E697.MirrorCS", {"start": v(75.62, -64.11) * mm, "end": v(75.78, -63.95) * mm});
            skLineSegment(sketch, "E698.MirrorCS", {"start": v(71.88, -60.37) * mm, "end": v(72.03, -60.21) * mm});
            skLineSegment(sketch, "E699.MirrorCS", {"start": v(72.1, -68.96) * mm, "end": v(70.9, -70.16) * mm});
            skArc(sketch, "E700.MirrorCS", {"start": v(84.52, -63.88) * mm, "mid": v(84.3, -63.84) * mm, "end": v(84.18, -64.02) * mm});
            skArc(sketch, "E701.MirrorCS", {"start": v(67.03, -56.55) * mm, "mid": v(67.25, -56.6) * mm, "end": v(67.38, -56.4) * mm});
            skArc(sketch, "E702.MirrorCS", {"start": v(85.78, -65.22) * mm, "mid": v(85.76, -65.15) * mm, "end": v(85.72, -65.08) * mm});
            skArc(sketch, "E703.MirrorCS", {"start": v(67.03, -63.88) * mm, "mid": v(67.25, -63.84) * mm, "end": v(67.38, -64.02) * mm});
            skLineSegment(sketch, "E704.MirrorCS", {"start": v(67.03, -56.55) * mm, "end": v(65.83, -55.35) * mm});
            skLineSegment(sketch, "E705.MirrorCS", {"start": v(79.68, -40.05) * mm, "end": v(79.52, -40.21) * mm});
            skArc(sketch, "E706.MirrorCS", {"start": v(85.78, -35.2) * mm, "mid": v(85.76, -35.28) * mm, "end": v(85.72, -35.35) * mm});
            skLineSegment(sketch, "E707.MirrorCS", {"start": v(72.03, -40.21) * mm, "end": v(71.88, -40.37) * mm});
            skLineSegment(sketch, "E708.MirrorCS", {"start": v(75.62, -56.31) * mm, "end": v(75.78, -56.47) * mm});
            skLineSegment(sketch, "E709.MirrorCS", {"start": v(71.88, -40.05) * mm, "end": v(72.03, -40.21) * mm});
            skArc(sketch, "E710.MirrorCS", {"start": v(65.78, -55.2) * mm, "mid": v(65.8, -55.28) * mm, "end": v(65.83, -55.35) * mm});
            skLineSegment(sketch, "E711.MirrorCS", {"start": v(72.03, -60.21) * mm, "end": v(71.88, -60.05) * mm});
            skArc(sketch, "E712.MirrorCS", {"start": v(71.97, -68.61) * mm, "mid": v(72.15, -68.74) * mm, "end": v(72.1, -68.96) * mm});
            skLineSegment(sketch, "E713.MirrorCS", {"start": v(79.52, -40.21) * mm, "end": v(79.68, -40.37) * mm});
            skLineSegment(sketch, "E714.MirrorCS", {"start": v(75.78, -43.95) * mm, "end": v(75.94, -44.11) * mm});
            skArc(sketch, "E715.MirrorCS", {"start": v(80.64, -70.16) * mm, "mid": v(80.7, -70.2) * mm, "end": v(80.78, -70.21) * mm});
            skLineSegment(sketch, "E716.MirrorCS", {"start": v(75.78, -56.47) * mm, "end": v(75.94, -56.31) * mm});
            skArc(sketch, "E717.MirrorCS", {"start": v(65.78, -65.22) * mm, "mid": v(65.8, -65.15) * mm, "end": v(65.83, -65.08) * mm});
            skLineSegment(sketch, "E718.MirrorCS", {"start": v(67.03, -63.88) * mm, "end": v(65.83, -65.08) * mm});
            skLineSegment(sketch, "E719.MirrorCS", {"start": v(84.52, -36.55) * mm, "end": v(85.72, -35.35) * mm});
            skArc(sketch, "E720.MirrorCS", {"start": v(85.78, -55.2) * mm, "mid": v(85.76, -55.28) * mm, "end": v(85.72, -55.35) * mm});
            skLineSegment(sketch, "E721.MirrorCS", {"start": v(75.62, -44.11) * mm, "end": v(75.78, -43.95) * mm});
            skArc(sketch, "E722.MirrorCS", {"start": v(65.78, -35.2) * mm, "mid": v(65.8, -35.28) * mm, "end": v(65.83, -35.35) * mm});
            skLineSegment(sketch, "E723.MirrorCS", {"start": v(84.52, -56.55) * mm, "end": v(85.72, -55.35) * mm});
            skArc(sketch, "E724.MirrorCS", {"start": v(84.52, -36.55) * mm, "mid": v(84.3, -36.59) * mm, "end": v(84.18, -36.4) * mm});
            skLineSegment(sketch, "E725.MirrorCS", {"start": v(84.52, -63.88) * mm, "end": v(85.72, -65.08) * mm});
            skLineSegment(sketch, "E726.MirrorCS", {"start": v(75.78, -63.95) * mm, "end": v(75.94, -64.11) * mm});
            skLineSegment(sketch, "E727.MirrorCS", {"start": v(67.03, -36.55) * mm, "end": v(65.83, -35.35) * mm});
            skLineSegment(sketch, "E728.MirrorCS", {"start": v(75.78, -36.47) * mm, "end": v(75.94, -36.31) * mm});
            skArc(sketch, "E729.MirrorCS", {"start": v(65.78, -45.22) * mm, "mid": v(65.8, -45.14) * mm, "end": v(65.83, -45.08) * mm});
            skLineSegment(sketch, "E730.MirrorCS", {"start": v(67.03, -43.88) * mm, "end": v(65.83, -45.08) * mm});
            skArc(sketch, "E731.MirrorCS", {"start": v(85.78, -45.22) * mm, "mid": v(85.76, -45.14) * mm, "end": v(85.72, -45.08) * mm});
            skArc(sketch, "E732.MirrorCS", {"start": v(79.58, -68.61) * mm, "mid": v(79.4, -68.74) * mm, "end": v(79.44, -68.96) * mm});
            skArc(sketch, "E733.MirrorCS", {"start": v(84.52, -56.55) * mm, "mid": v(84.3, -56.6) * mm, "end": v(84.18, -56.4) * mm});
            skArc(sketch, "E734.MirrorCS", {"start": v(67.03, -43.88) * mm, "mid": v(67.25, -43.84) * mm, "end": v(67.38, -44.02) * mm});
            skLineSegment(sketch, "E735.MirrorCS", {"start": v(65.78, -50.71) * mm, "end": v(65.78, -49.71) * mm});
            skLineSegment(sketch, "E736.MirrorCS", {"start": v(75.62, -36.31) * mm, "end": v(75.78, -36.47) * mm});
            skLineSegment(sketch, "E737.MirrorCS", {"start": v(67.38, -64.02) * mm, "end": v(67.38, -65.91) * mm});
            skArc(sketch, "E738.MirrorCS", {"start": v(84.52, -43.88) * mm, "mid": v(84.3, -43.84) * mm, "end": v(84.18, -44.02) * mm});
            skLineSegment(sketch, "E739.MirrorCS", {"start": v(67.38, -56.4) * mm, "end": v(67.38, -54.51) * mm});
            skLineSegment(sketch, "E740.MirrorCS", {"start": v(84.52, -43.88) * mm, "end": v(85.72, -45.08) * mm});
            skLineSegment(sketch, "E741.MirrorCS", {"start": v(79.44, -68.96) * mm, "end": v(80.64, -70.16) * mm});
            skLineSegment(sketch, "E742.MirrorCS", {"start": v(70.08, -68.61) * mm, "end": v(71.97, -68.61) * mm});
            skArc(sketch, "E743.MirrorCS", {"start": v(66.28, -70.21) * mm, "mid": v(65.92, -70.07) * mm, "end": v(65.78, -69.71) * mm});
            skArc(sketch, "E744.MirrorCS", {"start": v(85.28, -70.21) * mm, "mid": v(85.63, -70.07) * mm, "end": v(85.78, -69.71) * mm});
            skLineSegment(sketch, "E745.MirrorCS", {"start": v(67.38, -65.91) * mm, "end": v(69.02, -65.91) * mm});
            skLineSegment(sketch, "E746.MirrorCS", {"start": v(71.88, -63.05) * mm, "end": v(71.88, -60.37) * mm});
            skLineSegment(sketch, "E747.MirrorCS", {"start": v(84.18, -44.02) * mm, "end": v(84.18, -45.91) * mm});
            skArc(sketch, "E748.MirrorCS", {"start": v(67.03, -36.55) * mm, "mid": v(67.25, -36.59) * mm, "end": v(67.38, -36.4) * mm});
            skLineSegment(sketch, "E749.MirrorCS", {"start": v(70.08, -66.97) * mm, "end": v(70.08, -68.61) * mm});
            skLineSegment(sketch, "E750.MirrorCS", {"start": v(75.62, -64.11) * mm, "end": v(72.94, -64.11) * mm});
            skLineSegment(sketch, "E751.MirrorCS", {"start": v(75.62, -44.11) * mm, "end": v(72.94, -44.11) * mm});
            skLineSegment(sketch, "E752.MirrorCS", {"start": v(67.38, -45.91) * mm, "end": v(69.02, -45.91) * mm});
            skLineSegment(sketch, "E753.MirrorCS", {"start": v(75.94, -56.31) * mm, "end": v(78.62, -56.31) * mm});
            skLineSegment(sketch, "E754.MirrorCS", {"start": v(79.68, -43.05) * mm, "end": v(79.68, -40.37) * mm});
            skLineSegment(sketch, "E755.MirrorCS", {"start": v(81.48, -33.45) * mm, "end": v(81.48, -31.81) * mm});
            skLineSegment(sketch, "E756.MirrorCS", {"start": v(81.48, -68.61) * mm, "end": v(79.58, -68.61) * mm});
            skLineSegment(sketch, "E757.MirrorCS", {"start": v(79.68, -37.37) * mm, "end": v(79.68, -40.05) * mm});
            skLineSegment(sketch, "E758.MirrorCS", {"start": v(75.62, -56.31) * mm, "end": v(72.94, -56.31) * mm});
            skLineSegment(sketch, "E759.MirrorCS", {"start": v(81.48, -66.97) * mm, "end": v(81.48, -68.61) * mm});
            skLineSegment(sketch, "E760.MirrorCS", {"start": v(67.38, -54.51) * mm, "end": v(69.02, -54.51) * mm});
            skLineSegment(sketch, "E761.MirrorCS", {"start": v(71.88, -37.37) * mm, "end": v(71.88, -40.05) * mm});
            skLineSegment(sketch, "E762.MirrorCS", {"start": v(79.68, -57.37) * mm, "end": v(79.68, -60.05) * mm});
            skLineSegment(sketch, "E763.MirrorCS", {"start": v(84.18, -64.02) * mm, "end": v(84.18, -65.91) * mm});
            skLineSegment(sketch, "E764.MirrorCS", {"start": v(84.18, -34.51) * mm, "end": v(82.54, -34.51) * mm});
            skLineSegment(sketch, "E765.MirrorCS", {"start": v(75.94, -64.11) * mm, "end": v(78.62, -64.11) * mm});
            skLineSegment(sketch, "E766.MirrorCS", {"start": v(81.48, -53.45) * mm, "end": v(81.48, -51.81) * mm});
            skLineSegment(sketch, "E767.MirrorCS", {"start": v(84.18, -54.51) * mm, "end": v(82.54, -54.51) * mm});
            skLineSegment(sketch, "E768.MirrorCS", {"start": v(67.38, -44.02) * mm, "end": v(67.38, -45.91) * mm});
            skLineSegment(sketch, "E769.MirrorCS", {"start": v(71.88, -57.37) * mm, "end": v(71.88, -60.05) * mm});
            skLineSegment(sketch, "E770.MirrorCS", {"start": v(84.18, -36.4) * mm, "end": v(84.18, -34.51) * mm});
            skLineSegment(sketch, "E771.MirrorCS", {"start": v(70.08, -53.45) * mm, "end": v(70.08, -51.81) * mm});
            skLineSegment(sketch, "E772.MirrorCS", {"start": v(75.62, -36.31) * mm, "end": v(72.94, -36.31) * mm});
            skLineSegment(sketch, "E773.MirrorCS", {"start": v(84.18, -45.91) * mm, "end": v(82.54, -45.91) * mm});
            skLineSegment(sketch, "E774.MirrorCS", {"start": v(70.08, -33.45) * mm, "end": v(70.08, -31.81) * mm});
            skLineSegment(sketch, "E775.MirrorCS", {"start": v(85.78, -50.71) * mm, "end": v(85.78, -49.71) * mm});
            skLineSegment(sketch, "E776.MirrorCS", {"start": v(67.38, -34.51) * mm, "end": v(69.02, -34.51) * mm});
            skLineSegment(sketch, "E777.MirrorCS", {"start": v(67.38, -36.4) * mm, "end": v(67.38, -34.51) * mm});
            skLineSegment(sketch, "E778.MirrorCS", {"start": v(79.68, -63.05) * mm, "end": v(79.68, -60.37) * mm});
            skLineSegment(sketch, "E779.MirrorCS", {"start": v(75.94, -44.11) * mm, "end": v(78.62, -44.11) * mm});
            skLineSegment(sketch, "E780.MirrorCS", {"start": v(84.18, -65.91) * mm, "end": v(82.54, -65.91) * mm});
            skLineSegment(sketch, "E781.MirrorCS", {"start": v(70.08, -46.97) * mm, "end": v(70.08, -48.61) * mm});
            skLineSegment(sketch, "E782.MirrorCS", {"start": v(81.48, -46.97) * mm, "end": v(81.48, -48.61) * mm});
            skLineSegment(sketch, "E783.MirrorCS", {"start": v(70.08, -51.81) * mm, "end": v(70.08, -48.61) * mm});
            skLineSegment(sketch, "E784.MirrorCS", {"start": v(84.18, -56.4) * mm, "end": v(84.18, -54.51) * mm});
            skLineSegment(sketch, "E785.MirrorCS", {"start": v(71.88, -43.05) * mm, "end": v(71.88, -40.37) * mm});
            skLineSegment(sketch, "E786.MirrorCS", {"start": v(75.94, -36.31) * mm, "end": v(78.62, -36.31) * mm});
            skPoint(sketch, "E787.MirrorP", {"position": v(65.78, -50.21) * mm});
            skPoint(sketch, "E788.MirrorP", {"position": v(79.68, -60.21) * mm});
            skPoint(sketch, "E789.MirrorP", {"position": v(75.78, -44.11) * mm});
            skPoint(sketch, "E790.MirrorP", {"position": v(75.78, -36.31) * mm});
            skPoint(sketch, "E791.MirrorP", {"position": v(71.88, -60.21) * mm});
            skLineSegment(sketch, "E792.MirrorCS", {"start": v(65.78, -69.71) * mm, "end": v(65.78, -65.22) * mm});
            skLineSegment(sketch, "E793.MirrorCS", {"start": v(75.78, -60.21) * mm, "end": v(75.78, -42.9) * mm, "construction": true});
            skPoint(sketch, "E794.MirrorP", {"position": v(75.78, -64.11) * mm});
            skLineSegment(sketch, "E795.MirrorCS", {"start": v(69.02, -65.91) * mm, "end": v(71.88, -63.05) * mm});
            skPoint(sketch, "E796.MirrorP", {"position": v(71.88, -40.21) * mm});
            skPoint(sketch, "E797.MirrorP", {"position": v(70.85, -70.21) * mm});
            skPoint(sketch, "E798.MirrorP", {"position": v(79.68, -40.21) * mm});
            skPoint(sketch, "E799.MirrorP", {"position": v(75.78, -56.31) * mm});
            skLineSegment(sketch, "E800.MirrorCS", {"start": v(70.77, -70.21) * mm, "end": v(66.28, -70.21) * mm});
            skLineSegment(sketch, "E801.MirrorCS", {"start": v(72.94, -64.11) * mm, "end": v(70.08, -66.97) * mm});
            skLineSegment(sketch, "E802.MirrorCS", {"start": v(82.54, -65.91) * mm, "end": v(79.68, -63.05) * mm});
            skLineSegment(sketch, "E803.MirrorCS", {"start": v(82.54, -54.51) * mm, "end": v(79.68, -57.37) * mm});
            skPoint(sketch, "E804.MirrorP", {"position": v(80.7, -70.21) * mm});
            skPoint(sketch, "E805.MirrorP", {"position": v(84.18, -56.89) * mm});
            skPoint(sketch, "E806.MirrorP", {"position": v(85.78, -35.29) * mm});
            skLineSegment(sketch, "E807.MirrorCS", {"start": v(75.78, -40.21) * mm, "end": v(75.78, -22.9) * mm, "construction": true});
            skLineSegment(sketch, "E808.MirrorCS", {"start": v(85.78, -49.71) * mm, "end": v(85.78, -45.22) * mm});
            skLineSegment(sketch, "E809.MirrorCS", {"start": v(82.54, -45.91) * mm, "end": v(79.68, -43.05) * mm});
            skPoint(sketch, "E810.MirrorP", {"position": v(85.78, -65.14) * mm});
            skLineSegment(sketch, "E811.MirrorCS", {"start": v(85.78, -30.71) * mm, "end": v(85.78, -35.2) * mm});
            skLineSegment(sketch, "E812.MirrorCS", {"start": v(82.54, -34.51) * mm, "end": v(79.68, -37.37) * mm});
            skLineSegment(sketch, "E813.MirrorCS", {"start": v(65.78, -50.71) * mm, "end": v(65.78, -55.2) * mm});
            skLineSegment(sketch, "E814.MirrorCS", {"start": v(72.94, -56.31) * mm, "end": v(70.08, -53.45) * mm});
            skCircle(sketch, "E815.MirrorC", {"center": v(75.78, -60.21) * mm, "radius": 2.1 * mm});
            skLineSegment(sketch, "E816.MirrorCS", {"start": v(78.62, -56.31) * mm, "end": v(81.48, -53.45) * mm});
            skPoint(sketch, "E817.MirrorP", {"position": v(67.38, -36.89) * mm});
            skPoint(sketch, "E818.MirrorP", {"position": v(65.78, -45.14) * mm});
            skLineSegment(sketch, "E819.MirrorCS", {"start": v(75.78, -60.21) * mm, "end": v(75.78, -77.54) * mm, "construction": true});
            skLineSegment(sketch, "E820.MirrorCS", {"start": v(65.78, -49.71) * mm, "end": v(65.78, -45.22) * mm});
            skLineSegment(sketch, "E821.MirrorCS", {"start": v(75.78, -40.21) * mm, "end": v(75.78, -57.53) * mm, "construction": true});
            skLineSegment(sketch, "E822.MirrorCS", {"start": v(75.78, -60.21) * mm, "end": v(48.4, -60.21) * mm, "construction": true});
            skPoint(sketch, "E823.MirrorP", {"position": v(65.78, -55.29) * mm});
            skLineSegment(sketch, "E824.MirrorCS", {"start": v(85.78, -69.71) * mm, "end": v(85.78, -65.22) * mm});
            skLineSegment(sketch, "E825.MirrorCS", {"start": v(81.48, -51.81) * mm, "end": v(81.48, -48.61) * mm});
            skPoint(sketch, "E826.MirrorP", {"position": v(67.38, -56.89) * mm});
            skPoint(sketch, "E827.MirrorP", {"position": v(72.45, -68.61) * mm});
            skPoint(sketch, "E828.MirrorP", {"position": v(85.78, -55.29) * mm});
            skPoint(sketch, "E829.MirrorP", {"position": v(85.78, -70.21) * mm});
            skLineSegment(sketch, "E830.MirrorCS", {"start": v(78.62, -64.11) * mm, "end": v(81.48, -66.97) * mm});
            skPoint(sketch, "E831.MirrorP", {"position": v(85.78, -45.14) * mm});
            skLineSegment(sketch, "E832.MirrorCS", {"start": v(69.02, -54.51) * mm, "end": v(71.88, -57.37) * mm});
            skLineSegment(sketch, "E833.MirrorCS", {"start": v(80.78, -70.21) * mm, "end": v(85.28, -70.21) * mm});
            skLineSegment(sketch, "E834.MirrorCS", {"start": v(85.78, -50.71) * mm, "end": v(85.78, -55.2) * mm});
            skLineSegment(sketch, "E835.MirrorCS", {"start": v(78.62, -44.11) * mm, "end": v(81.48, -46.97) * mm});
            skLineSegment(sketch, "E836.MirrorCS", {"start": v(69.02, -34.51) * mm, "end": v(71.88, -37.37) * mm});
            skPoint(sketch, "E837.MirrorP", {"position": v(84.18, -36.89) * mm});
            skPoint(sketch, "E838.MirrorP", {"position": v(65.78, -65.14) * mm});
            skLineSegment(sketch, "E839.MirrorCS", {"start": v(72.94, -44.11) * mm, "end": v(70.08, -46.97) * mm});
            skPoint(sketch, "E840.MirrorP", {"position": v(65.78, -70.21) * mm});
            skPoint(sketch, "E841.MirrorP", {"position": v(84.18, -63.54) * mm});
            skPoint(sketch, "E842.MirrorP", {"position": v(67.38, -43.54) * mm});
            skPoint(sketch, "E843.MirrorP", {"position": v(84.18, -43.54) * mm});
            skPoint(sketch, "E844.MirrorP", {"position": v(79.1, -68.61) * mm});
            skCircle(sketch, "E845.MirrorC", {"center": v(75.78, -40.21) * mm, "radius": 2.1 * mm});
            skPoint(sketch, "E846.MirrorP", {"position": v(67.38, -63.54) * mm});
            skLineSegment(sketch, "E847.MirrorCS", {"start": v(78.62, -36.31) * mm, "end": v(81.48, -33.45) * mm});
            skLineSegment(sketch, "E848.MirrorCS", {"start": v(75.78, -40.21) * mm, "end": v(48.4, -40.21) * mm, "construction": true});
            skLineSegment(sketch, "E849.MirrorCS", {"start": v(65.78, -30.71) * mm, "end": v(65.78, -35.2) * mm});
            skLineSegment(sketch, "E850.MirrorCS", {"start": v(69.02, -45.91) * mm, "end": v(71.88, -43.05) * mm});
            skLineSegment(sketch, "E851.MirrorCS", {"start": v(72.94, -36.31) * mm, "end": v(70.08, -33.45) * mm});
            skPoint(sketch, "E852.MirrorP", {"position": v(65.78, -35.29) * mm});
            skLineSegment(sketch, "E853", {"start": v(70.08, -28.61) * mm, "end": v(70.08, -31.81) * mm});
            skLineSegment(sketch, "E854", {"start": v(81.48, -28.61) * mm, "end": v(81.48, -31.81) * mm});
            skLineSegment(sketch, "E855", {"start": v(65.78, -29.71) * mm, "end": v(65.78, -30.71) * mm});
            skLineSegment(sketch, "E856", {"start": v(85.78, -29.71) * mm, "end": v(85.78, -30.71) * mm});
            skSolve(sketch);
        }
        {
            var Q0;
            Q0=qCreatedBy(makeId("Front.planeOp"),FACE);
            var sketch = newSketch(context, id + "F4", { "sketchPlane" : qUnion([Q0])});
            skLineSegment(sketch, "E857", {"start": v(102.97, 4.05) * mm, "end": v(100.29, 4.05) * mm});
            skLineSegment(sketch, "E858", {"start": v(100.29, 4.05) * mm, "end": v(97.43, 6.9) * mm});
            skLineSegment(sketch, "E859", {"start": v(97.43, 6.9) * mm, "end": v(97.43, 8.55) * mm});
            skLineSegment(sketch, "E860", {"start": v(98.12, 10.15) * mm, "end": v(93.63, 10.15) * mm});
            skLineSegment(sketch, "E861", {"start": v(93.13, 9.65) * mm, "end": v(93.13, 5.15) * mm});
            skLineSegment(sketch, "E862", {"start": v(94.73, 3.95) * mm, "end": v(94.73, 5.85) * mm});
            skLineSegment(sketch, "E863", {"start": v(94.73, 5.85) * mm, "end": v(96.37, 5.85) * mm});
            skLineSegment(sketch, "E864", {"start": v(96.37, 5.85) * mm, "end": v(99.23, 2.99) * mm});
            skLineSegment(sketch, "E865", {"start": v(99.23, 2.99) * mm, "end": v(99.23, 0.3) * mm});
            skLineSegment(sketch, "E866", {"start": v(103.13, 0.15) * mm, "end": v(103.13, 17.47) * mm, "construction": true});
            skLineSegment(sketch, "E867", {"start": v(39.14, 77.15) * mm, "end": v(11.76, 77.15) * mm, "construction": true});
            skPoint(sketch, "E868.visualSharp", {"position": v(93.13, 10.15) * mm});
            skArc(sketch, "E868.filletArc", {"start": v(93.63, 10.15) * mm, "mid": v(93.27, 10) * mm, "end": v(93.13, 9.65) * mm});
            skLineSegment(sketch, "E869.filletArc", {"start": v(-70.86, 91.87) * mm, "end": v(-70.86, 91.87) * mm});
            skLineSegment(sketch, "E870", {"start": v(97.43, 8.55) * mm, "end": v(99.32, 8.55) * mm});
            skLineSegment(sketch, "E871", {"start": v(99.46, 8.89) * mm, "end": v(98.26, 10.09) * mm});
            skLineSegment(sketch, "E872", {"start": v(94.39, 3.81) * mm, "end": v(93.19, 5.01) * mm});
            skPoint(sketch, "E873.visualSharp", {"position": v(94.73, 3.47) * mm});
            skArc(sketch, "E873.filletArc", {"start": v(94.39, 3.81) * mm, "mid": v(94.6, 3.77) * mm, "end": v(94.73, 3.95) * mm});
            skPoint(sketch, "E874.visualSharp", {"position": v(99.8, 8.55) * mm});
            skArc(sketch, "E874.filletArc", {"start": v(99.32, 8.55) * mm, "mid": v(99.5, 8.67) * mm, "end": v(99.46, 8.89) * mm});
            skPoint(sketch, "E875.visualSharp", {"position": v(98.2, 10.15) * mm});
            skArc(sketch, "E875.filletArc", {"start": v(98.26, 10.09) * mm, "mid": v(98.2, 10.13) * mm, "end": v(98.12, 10.15) * mm});
            skPoint(sketch, "E876.visualSharp", {"position": v(93.13, 5.07) * mm});
            skArc(sketch, "E876.filletArc", {"start": v(93.13, 5.15) * mm, "mid": v(93.14, 5.08) * mm, "end": v(93.19, 5.01) * mm});
            skArc(sketch, "E877.MirrorCS", {"start": v(108, 10.09) * mm, "mid": v(108.06, 10.13) * mm, "end": v(108.14, 10.15) * mm});
            skArc(sketch, "E878.MirrorCS", {"start": v(106.94, 8.55) * mm, "mid": v(106.75, 8.67) * mm, "end": v(106.8, 8.89) * mm});
            skLineSegment(sketch, "E879.MirrorCS", {"start": v(-50.85, 91.87) * mm, "end": v(-50.85, 91.87) * mm});
            skLineSegment(sketch, "E880.MirrorCS", {"start": v(106.8, 8.89) * mm, "end": v(108, 10.09) * mm});
            skLineSegment(sketch, "E881.MirrorCS", {"start": v(109.89, 5.85) * mm, "end": v(107.03, 2.99) * mm});
            skLineSegment(sketch, "E882.MirrorCS", {"start": v(107.03, 2.99) * mm, "end": v(107.03, 0.3) * mm});
            skLineSegment(sketch, "E883.MirrorCS", {"start": v(103.29, 4.05) * mm, "end": v(105.97, 4.05) * mm});
            skLineSegment(sketch, "E884.MirrorCS", {"start": v(108.83, 8.55) * mm, "end": v(106.94, 8.55) * mm});
            skLineSegment(sketch, "E885.MirrorCS", {"start": v(105.97, 4.05) * mm, "end": v(108.83, 6.9) * mm});
            skPoint(sketch, "E886.MirrorP", {"position": v(106.45, 8.55) * mm});
            skPoint(sketch, "E887.MirrorP", {"position": v(108.05, 10.15) * mm});
            skLineSegment(sketch, "E888.MirrorCS", {"start": v(108.83, 6.9) * mm, "end": v(108.83, 8.55) * mm});
            skLineSegment(sketch, "E889.MirrorCS", {"start": v(108.14, 10.15) * mm, "end": v(112.63, 10.15) * mm});
            skPoint(sketch, "E890.MirrorP", {"position": v(113.13, 10.15) * mm});
            skArc(sketch, "E891.MirrorCS", {"start": v(94.39, -3.52) * mm, "mid": v(94.6, -3.48) * mm, "end": v(94.73, -3.66) * mm});
            skArc(sketch, "E892.MirrorCS", {"start": v(93.13, -4.86) * mm, "mid": v(93.14, -4.79) * mm, "end": v(93.19, -4.72) * mm});
            skLineSegment(sketch, "E893.MirrorCS", {"start": v(94.39, -3.52) * mm, "end": v(93.19, -4.72) * mm});
            skLineSegment(sketch, "E894.MirrorCS", {"start": v(103.13, 0.15) * mm, "end": v(103.13, -17.18) * mm, "construction": true});
            skLineSegment(sketch, "E895.MirrorCS", {"start": v(99.23, -2.7) * mm, "end": v(99.23, -0.01) * mm});
            skLineSegment(sketch, "E896.MirrorCS", {"start": v(105.97, -3.75) * mm, "end": v(108.83, -6.61) * mm});
            skPoint(sketch, "E897.MirrorP", {"position": v(94.73, -3.18) * mm});
            skLineSegment(sketch, "E898.MirrorCS", {"start": v(103.29, -3.75) * mm, "end": v(105.97, -3.75) * mm});
            skLineSegment(sketch, "E899.MirrorCS", {"start": v(100.29, -3.75) * mm, "end": v(97.43, -6.61) * mm});
            skLineSegment(sketch, "E900.MirrorCS", {"start": v(109.89, -5.55) * mm, "end": v(107.03, -2.7) * mm});
            skLineSegment(sketch, "E901.MirrorCS", {"start": v(94.73, -5.55) * mm, "end": v(96.37, -5.55) * mm});
            skLineSegment(sketch, "E902.MirrorCS", {"start": v(93.13, -9.35) * mm, "end": v(93.13, -4.86) * mm});
            skLineSegment(sketch, "E903.MirrorCS", {"start": v(94.73, -3.66) * mm, "end": v(94.73, -5.55) * mm});
            skLineSegment(sketch, "E904.MirrorCS", {"start": v(97.43, -6.61) * mm, "end": v(97.43, -8.25) * mm});
            skLineSegment(sketch, "E905.MirrorCS", {"start": v(96.37, -5.55) * mm, "end": v(99.23, -2.7) * mm});
            skLineSegment(sketch, "E906.MirrorCS", {"start": v(102.97, -3.75) * mm, "end": v(100.29, -3.75) * mm});
            skLineSegment(sketch, "E907.MirrorCS", {"start": v(107.03, -2.7) * mm, "end": v(107.03, -0.01) * mm});
            skLineSegment(sketch, "E908.MirrorCS", {"start": v(-70.86, 82.42) * mm, "end": v(-70.86, 82.42) * mm});
            skPoint(sketch, "E909.MirrorP", {"position": v(93.13, -4.78) * mm});
            skLineSegment(sketch, "E910.MirrorCS", {"start": v(-50.85, 82.42) * mm, "end": v(-50.85, 82.42) * mm});
            skPoint(sketch, "E911.MirrorP", {"position": v(93.13, -9.85) * mm});
            skCircle(sketch, "E912", {"center": v(103.13, 0.15) * mm, "radius": 2.1 * mm});
            skLineSegment(sketch, "E913", {"start": v(102.97, 4.05) * mm, "end": v(103.13, 3.89) * mm});
            skLineSegment(sketch, "E914", {"start": v(103.13, 3.89) * mm, "end": v(103.29, 4.05) * mm});
            skPoint(sketch, "E915.orphan", {"position": v(103.13, 4.05) * mm});
            skLineSegment(sketch, "E916.MirrorCS", {"start": v(102.97, -3.75) * mm, "end": v(103.13, -3.6) * mm});
            skLineSegment(sketch, "E917.MirrorCS", {"start": v(103.13, -3.6) * mm, "end": v(103.29, -3.75) * mm});
            skLineSegment(sketch, "E918", {"start": v(99.23, 0.3) * mm, "end": v(99.39, 0.15) * mm});
            skLineSegment(sketch, "E919", {"start": v(99.39, 0.15) * mm, "end": v(99.23, -0.01) * mm});
            skPoint(sketch, "E920.orphan", {"position": v(99.23, 0.15) * mm});
            skLineSegment(sketch, "E921.MirrorCS", {"start": v(106.87, 0.15) * mm, "end": v(107.03, -0.01) * mm});
            skLineSegment(sketch, "E922.MirrorCS", {"start": v(107.03, 0.3) * mm, "end": v(106.87, 0.15) * mm});
            skPoint(sketch, "E923.orphan", {"position": v(107.03, 0.15) * mm});
            skPoint(sketch, "E924.orphan", {"position": v(103.13, -3.75) * mm});
            skArc(sketch, "E925.MirrorCS", {"start": v(113.13, -24.86) * mm, "mid": v(113.11, -24.79) * mm, "end": v(113.07, -24.72) * mm});
            skLineSegment(sketch, "E926.MirrorCS", {"start": v(102.97, -23.76) * mm, "end": v(103.13, -23.6) * mm});
            skLineSegment(sketch, "E927.MirrorCS", {"start": v(102.97, -15.95) * mm, "end": v(103.13, -16.11) * mm});
            skLineSegment(sketch, "E928.MirrorCS", {"start": v(103.13, -23.6) * mm, "end": v(103.29, -23.76) * mm});
            skArc(sketch, "E929.MirrorCS", {"start": v(93.13, -24.86) * mm, "mid": v(93.14, -24.79) * mm, "end": v(93.19, -24.72) * mm});
            skArc(sketch, "E930.MirrorCS", {"start": v(111.87, -16.19) * mm, "mid": v(111.65, -16.23) * mm, "end": v(111.53, -16.05) * mm});
            skLineSegment(sketch, "E931.MirrorCS", {"start": v(99.23, -20.01) * mm, "end": v(99.39, -19.86) * mm});
            skLineSegment(sketch, "E932.MirrorCS", {"start": v(107.03, -20.01) * mm, "end": v(106.87, -19.86) * mm});
            skArc(sketch, "E933.MirrorCS", {"start": v(93.13, -14.85) * mm, "mid": v(93.14, -14.92) * mm, "end": v(93.19, -14.99) * mm});
            skLineSegment(sketch, "E934.MirrorCS", {"start": v(103.13, -16.11) * mm, "end": v(103.29, -15.95) * mm});
            skLineSegment(sketch, "E935.MirrorCS", {"start": v(99.39, -19.86) * mm, "end": v(99.23, -19.7) * mm});
            skArc(sketch, "E936.MirrorCS", {"start": v(113.13, -14.85) * mm, "mid": v(113.11, -14.92) * mm, "end": v(113.07, -14.99) * mm});
            skLineSegment(sketch, "E937.MirrorCS", {"start": v(106.87, -19.86) * mm, "end": v(107.03, -19.7) * mm});
            skArc(sketch, "E938.MirrorCS", {"start": v(94.39, -16.19) * mm, "mid": v(94.6, -16.23) * mm, "end": v(94.73, -16.05) * mm});
            skLineSegment(sketch, "E939.MirrorCS", {"start": v(94.39, -16.19) * mm, "end": v(93.19, -14.99) * mm});
            skLineSegment(sketch, "E940.MirrorCS", {"start": v(111.87, -16.19) * mm, "end": v(113.07, -14.99) * mm});
            skArc(sketch, "E941.MirrorCS", {"start": v(94.39, -23.52) * mm, "mid": v(94.6, -23.48) * mm, "end": v(94.73, -23.66) * mm});
            skLineSegment(sketch, "E942.MirrorCS", {"start": v(94.39, -23.52) * mm, "end": v(93.19, -24.72) * mm});
            skLineSegment(sketch, "E943.MirrorCS", {"start": v(111.53, -25.56) * mm, "end": v(109.89, -25.56) * mm});
            skLineSegment(sketch, "E944.MirrorCS", {"start": v(94.73, -14.16) * mm, "end": v(96.37, -14.16) * mm});
            skLineSegment(sketch, "E945.MirrorCS", {"start": v(108.83, -26.62) * mm, "end": v(108.83, -28.26) * mm});
            skArc(sketch, "E946.MirrorCS", {"start": v(111.87, -23.52) * mm, "mid": v(111.65, -23.48) * mm, "end": v(111.53, -23.66) * mm});
            skLineSegment(sketch, "E947.MirrorCS", {"start": v(94.73, -25.56) * mm, "end": v(96.37, -25.56) * mm});
            skLineSegment(sketch, "E948.MirrorCS", {"start": v(97.43, -26.62) * mm, "end": v(97.43, -28.26) * mm});
            skLineSegment(sketch, "E949.MirrorCS", {"start": v(111.87, -23.52) * mm, "end": v(113.07, -24.72) * mm});
            skLineSegment(sketch, "E950.MirrorCS", {"start": v(111.53, -14.16) * mm, "end": v(109.89, -14.16) * mm});
            skLineSegment(sketch, "E951.MirrorCS", {"start": v(94.73, -23.66) * mm, "end": v(94.73, -25.56) * mm});
            skPoint(sketch, "E952.MirrorP", {"position": v(103.13, -23.76) * mm});
            skPoint(sketch, "E953.MirrorP", {"position": v(103.13, -15.95) * mm});
            skPoint(sketch, "E954.MirrorP", {"position": v(107.03, -19.86) * mm});
            skPoint(sketch, "E955.MirrorP", {"position": v(99.23, -19.86) * mm});
            skPoint(sketch, "E956.MirrorP", {"position": v(93.13, -29.86) * mm});
            skPoint(sketch, "E957.MirrorP", {"position": v(111.53, -23.18) * mm});
            skPoint(sketch, "E958.MirrorP", {"position": v(93.13, -24.78) * mm});
            skPoint(sketch, "E959.MirrorP", {"position": v(94.73, -16.53) * mm});
            skLineSegment(sketch, "E960.MirrorCS", {"start": v(109.89, -14.16) * mm, "end": v(107.03, -17.02) * mm});
            skLineSegment(sketch, "E961.MirrorCS", {"start": v(93.13, -29.36) * mm, "end": v(93.13, -24.86) * mm});
            skLineSegment(sketch, "E962.MirrorCS", {"start": v(113.13, -29.36) * mm, "end": v(113.13, -24.86) * mm});
            skLineSegment(sketch, "E963.MirrorCS", {"start": v(103.13, -19.86) * mm, "end": v(103.13, -2.53) * mm, "construction": true});
            skLineSegment(sketch, "E964.MirrorCS", {"start": v(105.97, -23.76) * mm, "end": v(108.83, -26.62) * mm});
            skLineSegment(sketch, "E965.MirrorCS", {"start": v(100.29, -15.95) * mm, "end": v(97.43, -13.1) * mm});
            skLineSegment(sketch, "E966.MirrorCS", {"start": v(102.97, -15.95) * mm, "end": v(100.29, -15.95) * mm});
            skLineSegment(sketch, "E967.MirrorCS", {"start": v(93.13, -10.35) * mm, "end": v(93.13, -14.85) * mm});
            skPoint(sketch, "E968.MirrorP", {"position": v(113.13, -29.86) * mm});
            skLineSegment(sketch, "E969.MirrorCS", {"start": v(103.13, -19.86) * mm, "end": v(103.13, -37.18) * mm, "construction": true});
            skLineSegment(sketch, "E970.MirrorCS", {"start": v(109.89, -25.56) * mm, "end": v(107.03, -22.7) * mm});
            skPoint(sketch, "E971.MirrorP", {"position": v(111.53, -16.53) * mm});
            skLineSegment(sketch, "E972.MirrorCS", {"start": v(103.29, -23.76) * mm, "end": v(105.97, -23.76) * mm});
            skLineSegment(sketch, "E973.MirrorCS", {"start": v(111.53, -16.05) * mm, "end": v(111.53, -14.16) * mm});
            skCircle(sketch, "E974.MirrorC", {"center": v(103.13, -19.86) * mm, "radius": 2.1 * mm});
            skPoint(sketch, "E975.MirrorP", {"position": v(94.73, -23.18) * mm});
            skLineSegment(sketch, "E976.MirrorCS", {"start": v(99.23, -17.02) * mm, "end": v(99.23, -19.7) * mm});
            skLineSegment(sketch, "E977.MirrorCS", {"start": v(103.13, -19.86) * mm, "end": v(75.74, -19.86) * mm, "construction": true});
            skLineSegment(sketch, "E978.MirrorCS", {"start": v(97.43, -13.1) * mm, "end": v(97.43, -11.45) * mm});
            skLineSegment(sketch, "E979.MirrorCS", {"start": v(107.03, -17.02) * mm, "end": v(107.03, -19.7) * mm});
            skLineSegment(sketch, "E980.MirrorCS", {"start": v(94.73, -16.05) * mm, "end": v(94.73, -14.16) * mm});
            skPoint(sketch, "E981.MirrorP", {"position": v(113.13, -14.93) * mm});
            skLineSegment(sketch, "E982.MirrorCS", {"start": v(103.29, -15.95) * mm, "end": v(105.97, -15.95) * mm});
            skLineSegment(sketch, "E983.MirrorCS", {"start": v(107.03, -22.7) * mm, "end": v(107.03, -20.01) * mm});
            skLineSegment(sketch, "E984.MirrorCS", {"start": v(96.37, -14.16) * mm, "end": v(99.23, -17.02) * mm});
            skPoint(sketch, "E985.MirrorP", {"position": v(113.13, -24.78) * mm});
            skPoint(sketch, "E986.MirrorP", {"position": v(93.13, -14.93) * mm});
            skLineSegment(sketch, "E987.MirrorCS", {"start": v(111.53, -23.66) * mm, "end": v(111.53, -25.56) * mm});
            skLineSegment(sketch, "E988.MirrorCS", {"start": v(96.37, -25.56) * mm, "end": v(99.23, -22.7) * mm});
            skLineSegment(sketch, "E989.MirrorCS", {"start": v(105.97, -15.95) * mm, "end": v(108.83, -13.1) * mm});
            skLineSegment(sketch, "E990.MirrorCS", {"start": v(100.29, -23.76) * mm, "end": v(97.43, -26.62) * mm});
            skLineSegment(sketch, "E991.MirrorCS", {"start": v(102.97, -23.76) * mm, "end": v(100.29, -23.76) * mm});
            skLineSegment(sketch, "E992.MirrorCS", {"start": v(113.13, -10.35) * mm, "end": v(113.13, -14.85) * mm});
            skLineSegment(sketch, "E993.MirrorCS", {"start": v(99.23, -22.7) * mm, "end": v(99.23, -20.01) * mm});
            skLineSegment(sketch, "E994", {"start": v(97.43, -8.25) * mm, "end": v(97.43, -11.45) * mm});
            skLineSegment(sketch, "E995", {"start": v(93.13, -9.35) * mm, "end": v(93.13, -10.35) * mm});
            skLineSegment(sketch, "E996", {"start": v(113.13, -9.85) * mm, "end": v(113.13, -10.35) * mm});
            skLineSegment(sketch, "E997.MirrorCS", {"start": v(106.87, -59.86) * mm, "end": v(107.03, -59.7) * mm});
            skLineSegment(sketch, "E998.MirrorCS", {"start": v(107.03, -60.02) * mm, "end": v(106.87, -59.86) * mm});
            skArc(sketch, "E999.MirrorCS", {"start": v(98.26, -69.8) * mm, "mid": v(98.2, -69.84) * mm, "end": v(98.12, -69.86) * mm});
            skLineSegment(sketch, "E1000.MirrorCS", {"start": v(102.97, -63.76) * mm, "end": v(103.13, -63.6) * mm});
            skLineSegment(sketch, "E1001.MirrorCS", {"start": v(99.23, -60.02) * mm, "end": v(99.39, -59.86) * mm});
            skLineSegment(sketch, "E1002.MirrorCS", {"start": v(99.46, -68.6) * mm, "end": v(98.26, -69.8) * mm});
            skArc(sketch, "E1003.MirrorCS", {"start": v(94.39, -56.2) * mm, "mid": v(94.6, -56.23) * mm, "end": v(94.73, -56.05) * mm});
            skArc(sketch, "E1004.MirrorCS", {"start": v(94.39, -63.52) * mm, "mid": v(94.6, -63.48) * mm, "end": v(94.73, -63.67) * mm});
            skLineSegment(sketch, "E1005.MirrorCS", {"start": v(94.39, -56.2) * mm, "end": v(93.19, -55) * mm});
            skLineSegment(sketch, "E1006.MirrorCS", {"start": v(107.03, -39.7) * mm, "end": v(106.87, -39.86) * mm});
            skArc(sketch, "E1007.MirrorCS", {"start": v(113.13, -34.85) * mm, "mid": v(113.11, -34.93) * mm, "end": v(113.07, -34.99) * mm});
            skLineSegment(sketch, "E1008.MirrorCS", {"start": v(99.39, -39.86) * mm, "end": v(99.23, -40.02) * mm});
            skLineSegment(sketch, "E1009.MirrorCS", {"start": v(102.97, -55.96) * mm, "end": v(103.13, -56.12) * mm});
            skLineSegment(sketch, "E1010.MirrorCS", {"start": v(99.23, -39.7) * mm, "end": v(99.39, -39.86) * mm});
            skArc(sketch, "E1011.MirrorCS", {"start": v(93.13, -54.85) * mm, "mid": v(93.14, -54.93) * mm, "end": v(93.19, -55) * mm});
            skLineSegment(sketch, "E1012.MirrorCS", {"start": v(99.39, -59.86) * mm, "end": v(99.23, -59.7) * mm});
            skArc(sketch, "E1013.MirrorCS", {"start": v(99.32, -68.26) * mm, "mid": v(99.5, -68.38) * mm, "end": v(99.46, -68.6) * mm});
            skLineSegment(sketch, "E1014.MirrorCS", {"start": v(106.87, -39.86) * mm, "end": v(107.03, -40.02) * mm});
            skLineSegment(sketch, "E1015.MirrorCS", {"start": v(103.13, -43.6) * mm, "end": v(103.29, -43.76) * mm});
            skArc(sketch, "E1016.MirrorCS", {"start": v(108, -69.8) * mm, "mid": v(108.06, -69.84) * mm, "end": v(108.14, -69.86) * mm});
            skLineSegment(sketch, "E1017.MirrorCS", {"start": v(103.13, -56.12) * mm, "end": v(103.29, -55.96) * mm});
            skArc(sketch, "E1018.MirrorCS", {"start": v(93.13, -64.87) * mm, "mid": v(93.14, -64.79) * mm, "end": v(93.19, -64.72) * mm});
            skLineSegment(sketch, "E1019.MirrorCS", {"start": v(94.39, -63.52) * mm, "end": v(93.19, -64.72) * mm});
            skLineSegment(sketch, "E1020.MirrorCS", {"start": v(111.87, -36.19) * mm, "end": v(113.07, -34.99) * mm});
            skLineSegment(sketch, "E1021.MirrorCS", {"start": v(102.97, -43.76) * mm, "end": v(103.13, -43.6) * mm});
            skArc(sketch, "E1022.MirrorCS", {"start": v(93.13, -34.85) * mm, "mid": v(93.14, -34.93) * mm, "end": v(93.19, -34.99) * mm});
            skArc(sketch, "E1023.MirrorCS", {"start": v(111.87, -36.19) * mm, "mid": v(111.65, -36.23) * mm, "end": v(111.53, -36.05) * mm});
            skLineSegment(sketch, "E1024.MirrorCS", {"start": v(103.13, -63.6) * mm, "end": v(103.29, -63.76) * mm});
            skLineSegment(sketch, "E1025.MirrorCS", {"start": v(94.39, -36.19) * mm, "end": v(93.19, -34.99) * mm});
            skLineSegment(sketch, "E1026.MirrorCS", {"start": v(103.13, -36.12) * mm, "end": v(103.29, -35.96) * mm});
            skArc(sketch, "E1027.MirrorCS", {"start": v(93.13, -44.86) * mm, "mid": v(93.14, -44.79) * mm, "end": v(93.19, -44.72) * mm});
            skLineSegment(sketch, "E1028.MirrorCS", {"start": v(94.39, -43.52) * mm, "end": v(93.19, -44.72) * mm});
            skArc(sketch, "E1029.MirrorCS", {"start": v(113.13, -44.86) * mm, "mid": v(113.11, -44.79) * mm, "end": v(113.07, -44.72) * mm});
            skArc(sketch, "E1030.MirrorCS", {"start": v(106.94, -68.26) * mm, "mid": v(106.75, -68.38) * mm, "end": v(106.8, -68.6) * mm});
            skArc(sketch, "E1031.MirrorCS", {"start": v(94.39, -43.52) * mm, "mid": v(94.6, -43.48) * mm, "end": v(94.73, -43.66) * mm});
            skLineSegment(sketch, "E1032.MirrorCS", {"start": v(93.13, -50.36) * mm, "end": v(93.13, -49.36) * mm});
            skLineSegment(sketch, "E1033.MirrorCS", {"start": v(102.97, -35.96) * mm, "end": v(103.13, -36.12) * mm});
            skLineSegment(sketch, "E1034.MirrorCS", {"start": v(94.73, -63.67) * mm, "end": v(94.73, -65.56) * mm});
            skArc(sketch, "E1035.MirrorCS", {"start": v(111.87, -43.52) * mm, "mid": v(111.65, -43.48) * mm, "end": v(111.53, -43.66) * mm});
            skLineSegment(sketch, "E1036.MirrorCS", {"start": v(94.73, -56.05) * mm, "end": v(94.73, -54.16) * mm});
            skLineSegment(sketch, "E1037.MirrorCS", {"start": v(111.87, -43.52) * mm, "end": v(113.07, -44.72) * mm});
            skLineSegment(sketch, "E1038.MirrorCS", {"start": v(106.8, -68.6) * mm, "end": v(108, -69.8) * mm});
            skLineSegment(sketch, "E1039.MirrorCS", {"start": v(97.43, -68.26) * mm, "end": v(99.32, -68.26) * mm});
            skArc(sketch, "E1040.MirrorCS", {"start": v(93.63, -69.86) * mm, "mid": v(93.27, -69.71) * mm, "end": v(93.13, -69.36) * mm});
            skLineSegment(sketch, "E1041.MirrorCS", {"start": v(94.73, -65.56) * mm, "end": v(96.37, -65.56) * mm});
            skLineSegment(sketch, "E1042.MirrorCS", {"start": v(99.23, -62.7) * mm, "end": v(99.23, -60.02) * mm});
            skLineSegment(sketch, "E1043.MirrorCS", {"start": v(111.53, -43.66) * mm, "end": v(111.53, -45.56) * mm});
            skArc(sketch, "E1044.MirrorCS", {"start": v(94.39, -36.19) * mm, "mid": v(94.6, -36.23) * mm, "end": v(94.73, -36.05) * mm});
            skLineSegment(sketch, "E1045.MirrorCS", {"start": v(97.43, -66.62) * mm, "end": v(97.43, -68.26) * mm});
            skLineSegment(sketch, "E1046.MirrorCS", {"start": v(102.97, -63.76) * mm, "end": v(100.29, -63.76) * mm});
            skLineSegment(sketch, "E1047.MirrorCS", {"start": v(102.97, -43.76) * mm, "end": v(100.29, -43.76) * mm});
            skLineSegment(sketch, "E1048.MirrorCS", {"start": v(94.73, -45.56) * mm, "end": v(96.37, -45.56) * mm});
            skLineSegment(sketch, "E1049.MirrorCS", {"start": v(103.29, -55.96) * mm, "end": v(105.97, -55.96) * mm});
            skLineSegment(sketch, "E1050.MirrorCS", {"start": v(107.03, -42.7) * mm, "end": v(107.03, -40.02) * mm});
            skLineSegment(sketch, "E1051.MirrorCS", {"start": v(108.83, -33.1) * mm, "end": v(108.83, -31.46) * mm});
            skLineSegment(sketch, "E1052.MirrorCS", {"start": v(108.83, -68.26) * mm, "end": v(106.94, -68.26) * mm});
            skLineSegment(sketch, "E1053.MirrorCS", {"start": v(107.03, -37.02) * mm, "end": v(107.03, -39.7) * mm});
            skLineSegment(sketch, "E1054.MirrorCS", {"start": v(102.97, -55.96) * mm, "end": v(100.29, -55.96) * mm});
            skLineSegment(sketch, "E1055.MirrorCS", {"start": v(108.83, -66.62) * mm, "end": v(108.83, -68.26) * mm});
            skLineSegment(sketch, "E1056.MirrorCS", {"start": v(94.73, -54.16) * mm, "end": v(96.37, -54.16) * mm});
            skLineSegment(sketch, "E1057.MirrorCS", {"start": v(99.23, -37.02) * mm, "end": v(99.23, -39.7) * mm});
            skLineSegment(sketch, "E1058.MirrorCS", {"start": v(107.03, -57.02) * mm, "end": v(107.03, -59.7) * mm});
            skLineSegment(sketch, "E1059.MirrorCS", {"start": v(111.53, -34.16) * mm, "end": v(109.89, -34.16) * mm});
            skLineSegment(sketch, "E1060.MirrorCS", {"start": v(103.29, -63.76) * mm, "end": v(105.97, -63.76) * mm});
            skLineSegment(sketch, "E1061.MirrorCS", {"start": v(94.73, -43.66) * mm, "end": v(94.73, -45.56) * mm});
            skLineSegment(sketch, "E1062.MirrorCS", {"start": v(99.23, -57.02) * mm, "end": v(99.23, -59.7) * mm});
            skLineSegment(sketch, "E1063.MirrorCS", {"start": v(111.53, -36.05) * mm, "end": v(111.53, -34.16) * mm});
            skLineSegment(sketch, "E1064.MirrorCS", {"start": v(97.43, -53.1) * mm, "end": v(97.43, -51.46) * mm});
            skLineSegment(sketch, "E1065.MirrorCS", {"start": v(102.97, -35.96) * mm, "end": v(100.29, -35.96) * mm});
            skLineSegment(sketch, "E1066.MirrorCS", {"start": v(111.53, -45.56) * mm, "end": v(109.89, -45.56) * mm});
            skLineSegment(sketch, "E1067.MirrorCS", {"start": v(97.43, -33.1) * mm, "end": v(97.43, -31.46) * mm});
            skLineSegment(sketch, "E1068.MirrorCS", {"start": v(94.73, -34.16) * mm, "end": v(96.37, -34.16) * mm});
            skLineSegment(sketch, "E1069.MirrorCS", {"start": v(94.73, -36.05) * mm, "end": v(94.73, -34.16) * mm});
            skLineSegment(sketch, "E1070.MirrorCS", {"start": v(107.03, -62.7) * mm, "end": v(107.03, -60.02) * mm});
            skLineSegment(sketch, "E1071.MirrorCS", {"start": v(103.29, -43.76) * mm, "end": v(105.97, -43.76) * mm});
            skLineSegment(sketch, "E1072.MirrorCS", {"start": v(97.43, -46.62) * mm, "end": v(97.43, -48.26) * mm});
            skLineSegment(sketch, "E1073.MirrorCS", {"start": v(97.43, -51.46) * mm, "end": v(97.43, -48.26) * mm});
            skLineSegment(sketch, "E1074.MirrorCS", {"start": v(99.23, -42.7) * mm, "end": v(99.23, -40.02) * mm});
            skLineSegment(sketch, "E1075.MirrorCS", {"start": v(103.29, -35.96) * mm, "end": v(105.97, -35.96) * mm});
            skPoint(sketch, "E1076.MirrorP", {"position": v(93.13, -49.86) * mm});
            skPoint(sketch, "E1077.MirrorP", {"position": v(107.03, -59.86) * mm});
            skPoint(sketch, "E1078.MirrorP", {"position": v(103.13, -43.76) * mm});
            skPoint(sketch, "E1079.MirrorP", {"position": v(103.13, -35.96) * mm});
            skPoint(sketch, "E1080.MirrorP", {"position": v(99.23, -59.86) * mm});
            skLineSegment(sketch, "E1081.MirrorCS", {"start": v(93.13, -69.36) * mm, "end": v(93.13, -64.87) * mm});
            skLineSegment(sketch, "E1082.MirrorCS", {"start": v(103.13, -59.86) * mm, "end": v(103.13, -42.54) * mm, "construction": true});
            skPoint(sketch, "E1083.MirrorP", {"position": v(103.13, -63.76) * mm});
            skLineSegment(sketch, "E1084.MirrorCS", {"start": v(96.37, -65.56) * mm, "end": v(99.23, -62.7) * mm});
            skPoint(sketch, "E1085.MirrorP", {"position": v(99.23, -39.86) * mm});
            skPoint(sketch, "E1086.MirrorP", {"position": v(98.2, -69.86) * mm});
            skPoint(sketch, "E1087.MirrorP", {"position": v(107.03, -39.86) * mm});
            skPoint(sketch, "E1088.MirrorP", {"position": v(103.13, -55.96) * mm});
            skLineSegment(sketch, "E1089.MirrorCS", {"start": v(98.12, -69.86) * mm, "end": v(93.63, -69.86) * mm});
            skLineSegment(sketch, "E1090.MirrorCS", {"start": v(100.29, -63.76) * mm, "end": v(97.43, -66.62) * mm});
            skLineSegment(sketch, "E1091.MirrorCS", {"start": v(109.9, -65.56) * mm, "end": v(107.03, -62.7) * mm});
            skLineSegment(sketch, "E1092.MirrorCS", {"start": v(109.89, -54.16) * mm, "end": v(107.03, -57.02) * mm});
            skPoint(sketch, "E1093.MirrorP", {"position": v(108.05, -69.86) * mm});
            skPoint(sketch, "E1094.MirrorP", {"position": v(113.13, -34.93) * mm});
            skLineSegment(sketch, "E1095.MirrorCS", {"start": v(103.13, -39.86) * mm, "end": v(103.13, -22.53) * mm, "construction": true});
            skLineSegment(sketch, "E1096.MirrorCS", {"start": v(113.13, -49.36) * mm, "end": v(113.13, -44.86) * mm});
            skLineSegment(sketch, "E1097.MirrorCS", {"start": v(109.89, -45.56) * mm, "end": v(107.03, -42.7) * mm});
            skLineSegment(sketch, "E1098.MirrorCS", {"start": v(113.13, -30.36) * mm, "end": v(113.13, -34.85) * mm});
            skLineSegment(sketch, "E1099.MirrorCS", {"start": v(109.89, -34.16) * mm, "end": v(107.03, -37.02) * mm});
            skLineSegment(sketch, "E1100.MirrorCS", {"start": v(93.13, -50.36) * mm, "end": v(93.13, -54.85) * mm});
            skLineSegment(sketch, "E1101.MirrorCS", {"start": v(100.29, -55.96) * mm, "end": v(97.43, -53.1) * mm});
            skCircle(sketch, "E1102.MirrorC", {"center": v(103.13, -59.86) * mm, "radius": 2.1 * mm});
            skLineSegment(sketch, "E1103.MirrorCS", {"start": v(105.97, -55.96) * mm, "end": v(108.83, -53.1) * mm});
            skPoint(sketch, "E1104.MirrorP", {"position": v(94.73, -36.53) * mm});
            skPoint(sketch, "E1105.MirrorP", {"position": v(93.13, -44.78) * mm});
            skLineSegment(sketch, "E1106.MirrorCS", {"start": v(103.13, -59.86) * mm, "end": v(103.13, -77.18) * mm, "construction": true});
            skLineSegment(sketch, "E1107.MirrorCS", {"start": v(93.13, -49.36) * mm, "end": v(93.13, -44.86) * mm});
            skLineSegment(sketch, "E1108.MirrorCS", {"start": v(103.13, -39.86) * mm, "end": v(103.13, -57.18) * mm, "construction": true});
            skLineSegment(sketch, "E1109.MirrorCS", {"start": v(103.13, -59.86) * mm, "end": v(75.74, -59.86) * mm, "construction": true});
            skPoint(sketch, "E1110.MirrorP", {"position": v(93.13, -54.93) * mm});
            skPoint(sketch, "E1111.MirrorP", {"position": v(94.73, -56.53) * mm});
            skPoint(sketch, "E1112.MirrorP", {"position": v(99.8, -68.26) * mm});
            skPoint(sketch, "E1113.MirrorP", {"position": v(113.13, -69.86) * mm});
            skLineSegment(sketch, "E1114.MirrorCS", {"start": v(105.97, -63.76) * mm, "end": v(108.83, -66.62) * mm});
            skPoint(sketch, "E1115.MirrorP", {"position": v(113.13, -44.78) * mm});
            skLineSegment(sketch, "E1116.MirrorCS", {"start": v(96.37, -54.16) * mm, "end": v(99.23, -57.02) * mm});
            skLineSegment(sketch, "E1117.MirrorCS", {"start": v(108.14, -69.86) * mm, "end": v(112.63, -69.86) * mm});
            skLineSegment(sketch, "E1118.MirrorCS", {"start": v(105.97, -43.76) * mm, "end": v(108.83, -46.62) * mm});
            skLineSegment(sketch, "E1119.MirrorCS", {"start": v(96.37, -34.16) * mm, "end": v(99.23, -37.02) * mm});
            skPoint(sketch, "E1120.MirrorP", {"position": v(111.53, -36.53) * mm});
            skPoint(sketch, "E1121.MirrorP", {"position": v(93.13, -64.78) * mm});
            skLineSegment(sketch, "E1122.MirrorCS", {"start": v(100.29, -43.76) * mm, "end": v(97.43, -46.62) * mm});
            skPoint(sketch, "E1123.MirrorP", {"position": v(93.13, -69.86) * mm});
            skPoint(sketch, "E1124.MirrorP", {"position": v(94.73, -43.18) * mm});
            skPoint(sketch, "E1125.MirrorP", {"position": v(111.53, -43.18) * mm});
            skPoint(sketch, "E1126.MirrorP", {"position": v(106.45, -68.26) * mm});
            skCircle(sketch, "E1127.MirrorC", {"center": v(103.13, -39.86) * mm, "radius": 2.1 * mm});
            skPoint(sketch, "E1128.MirrorP", {"position": v(94.73, -63.18) * mm});
            skLineSegment(sketch, "E1129.MirrorCS", {"start": v(105.97, -35.96) * mm, "end": v(108.83, -33.1) * mm});
            skLineSegment(sketch, "E1130.MirrorCS", {"start": v(103.13, -39.86) * mm, "end": v(75.74, -39.86) * mm, "construction": true});
            skLineSegment(sketch, "E1131.MirrorCS", {"start": v(93.13, -30.36) * mm, "end": v(93.13, -34.85) * mm});
            skLineSegment(sketch, "E1132.MirrorCS", {"start": v(96.37, -45.56) * mm, "end": v(99.23, -42.7) * mm});
            skLineSegment(sketch, "E1133.MirrorCS", {"start": v(100.29, -35.96) * mm, "end": v(97.43, -33.1) * mm});
            skPoint(sketch, "E1134.MirrorP", {"position": v(93.13, -34.93) * mm});
            skLineSegment(sketch, "E1135", {"start": v(97.43, -28.26) * mm, "end": v(97.43, -31.46) * mm});
            skLineSegment(sketch, "E1136", {"start": v(108.83, -28.26) * mm, "end": v(108.83, -31.46) * mm});
            skLineSegment(sketch, "E1137", {"start": v(93.13, -29.36) * mm, "end": v(93.13, -30.36) * mm});
            skLineSegment(sketch, "E1138", {"start": v(113.13, -29.36) * mm, "end": v(113.13, -30.36) * mm});
            skLineSegment(sketch, "E1139", {"start": v(122.97, 4.05) * mm, "end": v(120.3, 4.05) * mm});
            skLineSegment(sketch, "E1140", {"start": v(120.3, 4.05) * mm, "end": v(117.43, 6.9) * mm});
            skLineSegment(sketch, "E1141", {"start": v(117.43, 6.9) * mm, "end": v(117.43, 8.55) * mm});
            skLineSegment(sketch, "E1142", {"start": v(118.12, 10.15) * mm, "end": v(113.63, 10.15) * mm});
            skLineSegment(sketch, "E1143", {"start": v(116.37, 5.85) * mm, "end": v(119.23, 2.99) * mm});
            skLineSegment(sketch, "E1144", {"start": v(119.23, 2.99) * mm, "end": v(119.23, 0.3) * mm});
            skLineSegment(sketch, "E1145", {"start": v(123.13, 0.15) * mm, "end": v(123.13, 17.47) * mm, "construction": true});
            skLineSegment(sketch, "E1146", {"start": v(123.13, 0.15) * mm, "end": v(95.75, 0.15) * mm, "construction": true});
            skLineSegment(sketch, "E1147.filletArc", {"start": v(119.7, -5.3) * mm, "end": v(119.7, -5.3) * mm});
            skLineSegment(sketch, "E1148", {"start": v(117.43, 8.55) * mm, "end": v(119.32, 8.55) * mm});
            skLineSegment(sketch, "E1149", {"start": v(119.46, 8.89) * mm, "end": v(118.26, 10.09) * mm});
            skArc(sketch, "E1150.filletArc", {"start": v(119.32, 8.55) * mm, "mid": v(119.5, 8.67) * mm, "end": v(119.46, 8.89) * mm});
            skPoint(sketch, "E1151.visualSharp", {"position": v(118.2, 10.15) * mm});
            skArc(sketch, "E1151.filletArc", {"start": v(118.26, 10.09) * mm, "mid": v(118.2, 10.13) * mm, "end": v(118.12, 10.15) * mm});
            skArc(sketch, "E1152.MirrorCS", {"start": v(131.87, 3.81) * mm, "mid": v(131.65, 3.77) * mm, "end": v(131.53, 3.95) * mm});
            skArc(sketch, "E1153.MirrorCS", {"start": v(133.13, 5.15) * mm, "mid": v(133.12, 5.08) * mm, "end": v(133.07, 5.01) * mm});
            skArc(sketch, "E1154.MirrorCS", {"start": v(128, 10.09) * mm, "mid": v(128.06, 10.13) * mm, "end": v(128.14, 10.15) * mm});
            skArc(sketch, "E1155.MirrorCS", {"start": v(126.94, 8.55) * mm, "mid": v(126.75, 8.67) * mm, "end": v(126.8, 8.89) * mm});
            skArc(sketch, "E1156.MirrorCS", {"start": v(132.63, 10.15) * mm, "mid": v(132.98, 10) * mm, "end": v(133.13, 9.65) * mm});
            skPoint(sketch, "E1157.MirrorP", {"position": v(131.53, 3.47) * mm});
            skLineSegment(sketch, "E1158.MirrorCS", {"start": v(126.8, 8.89) * mm, "end": v(128, 10.09) * mm});
            skLineSegment(sketch, "E1159.MirrorCS", {"start": v(129.9, 5.85) * mm, "end": v(127.03, 2.99) * mm});
            skLineSegment(sketch, "E1160.MirrorCS", {"start": v(127.03, 2.99) * mm, "end": v(127.03, 0.3) * mm});
            skLineSegment(sketch, "E1161.MirrorCS", {"start": v(133.13, 9.65) * mm, "end": v(133.13, 5.15) * mm});
            skLineSegment(sketch, "E1162.MirrorCS", {"start": v(123.29, 4.05) * mm, "end": v(125.97, 4.05) * mm});
            skPoint(sketch, "E1163.MirrorP", {"position": v(133.13, 5.07) * mm});
            skLineSegment(sketch, "E1164.MirrorCS", {"start": v(131.53, 3.95) * mm, "end": v(131.53, 5.85) * mm});
            skLineSegment(sketch, "E1165.MirrorCS", {"start": v(128.83, 8.55) * mm, "end": v(126.94, 8.55) * mm});
            skLineSegment(sketch, "E1166.MirrorCS", {"start": v(125.97, 4.05) * mm, "end": v(128.83, 6.9) * mm});
            skPoint(sketch, "E1167.MirrorP", {"position": v(126.46, 8.55) * mm});
            skLineSegment(sketch, "E1168.MirrorCS", {"start": v(131.53, 5.85) * mm, "end": v(129.9, 5.85) * mm});
            skPoint(sketch, "E1169.MirrorP", {"position": v(128.06, 10.15) * mm});
            skLineSegment(sketch, "E1170.MirrorCS", {"start": v(131.87, 3.81) * mm, "end": v(133.07, 5.01) * mm});
            skLineSegment(sketch, "E1171.MirrorCS", {"start": v(128.83, 6.9) * mm, "end": v(128.83, 8.55) * mm});
            skLineSegment(sketch, "E1172.MirrorCS", {"start": v(128.14, 10.15) * mm, "end": v(132.63, 10.15) * mm});
            skPoint(sketch, "E1173.MirrorP", {"position": v(133.13, 10.15) * mm});
            skArc(sketch, "E1174.MirrorCS", {"start": v(118.26, -9.8) * mm, "mid": v(118.2, -9.84) * mm, "end": v(118.12, -9.85) * mm});
            skArc(sketch, "E1175.MirrorCS", {"start": v(133.13, -4.86) * mm, "mid": v(133.12, -4.79) * mm, "end": v(133.07, -4.72) * mm});
            skArc(sketch, "E1176.MirrorCS", {"start": v(128, -9.8) * mm, "mid": v(128.06, -9.84) * mm, "end": v(128.14, -9.85) * mm});
            skArc(sketch, "E1177.MirrorCS", {"start": v(119.32, -8.25) * mm, "mid": v(119.5, -8.38) * mm, "end": v(119.46, -8.6) * mm});
            skArc(sketch, "E1178.MirrorCS", {"start": v(131.87, -3.52) * mm, "mid": v(131.65, -3.48) * mm, "end": v(131.53, -3.66) * mm});
            skArc(sketch, "E1179.MirrorCS", {"start": v(126.94, -8.25) * mm, "mid": v(126.75, -8.38) * mm, "end": v(126.8, -8.6) * mm});
            skArc(sketch, "E1180.MirrorCS", {"start": v(132.63, -9.85) * mm, "mid": v(132.98, -9.7) * mm, "end": v(133.13, -9.35) * mm});
            skLineSegment(sketch, "E1181.MirrorCS", {"start": v(119.46, -8.6) * mm, "end": v(118.26, -9.8) * mm});
            skLineSegment(sketch, "E1182.MirrorCS", {"start": v(117.43, -8.25) * mm, "end": v(119.32, -8.25) * mm});
            skLineSegment(sketch, "E1183.MirrorCS", {"start": v(131.53, -5.55) * mm, "end": v(129.9, -5.55) * mm});
            skLineSegment(sketch, "E1184.MirrorCS", {"start": v(131.87, -3.52) * mm, "end": v(133.07, -4.72) * mm});
            skLineSegment(sketch, "E1185.MirrorCS", {"start": v(123.13, 0.15) * mm, "end": v(123.13, -17.18) * mm, "construction": true});
            skLineSegment(sketch, "E1186.MirrorCS", {"start": v(128.83, -6.61) * mm, "end": v(128.83, -8.25) * mm});
            skLineSegment(sketch, "E1187.MirrorCS", {"start": v(119.23, -2.7) * mm, "end": v(119.23, -0.01) * mm});
            skLineSegment(sketch, "E1188.MirrorCS", {"start": v(128.14, -9.85) * mm, "end": v(132.63, -9.85) * mm});
            skLineSegment(sketch, "E1189.MirrorCS", {"start": v(125.97, -3.75) * mm, "end": v(128.83, -6.61) * mm});
            skPoint(sketch, "E1190.MirrorP", {"position": v(118.2, -9.85) * mm});
            skLineSegment(sketch, "E1191.MirrorCS", {"start": v(123.29, -3.75) * mm, "end": v(125.97, -3.75) * mm});
            skLineSegment(sketch, "E1192.MirrorCS", {"start": v(118.12, -9.85) * mm, "end": v(113.63, -9.85) * mm});
            skPoint(sketch, "E1193.MirrorP", {"position": v(133.13, -9.85) * mm});
            skLineSegment(sketch, "E1194.MirrorCS", {"start": v(120.3, -3.75) * mm, "end": v(117.43, -6.61) * mm});
            skLineSegment(sketch, "E1195.MirrorCS", {"start": v(129.9, -5.55) * mm, "end": v(127.03, -2.7) * mm});
            skLineSegment(sketch, "E1196.MirrorCS", {"start": v(133.13, -9.35) * mm, "end": v(133.13, -4.86) * mm});
            skPoint(sketch, "E1197.MirrorP", {"position": v(119.8, -8.25) * mm});
            skPoint(sketch, "E1198.MirrorP", {"position": v(126.46, -8.25) * mm});
            skLineSegment(sketch, "E1199.MirrorCS", {"start": v(131.53, -3.66) * mm, "end": v(131.53, -5.55) * mm});
            skPoint(sketch, "E1200.MirrorP", {"position": v(131.53, -3.18) * mm});
            skPoint(sketch, "E1201.MirrorP", {"position": v(133.13, -4.78) * mm});
            skLineSegment(sketch, "E1202.MirrorCS", {"start": v(117.43, -6.61) * mm, "end": v(117.43, -8.25) * mm});
            skLineSegment(sketch, "E1203.MirrorCS", {"start": v(116.37, -5.55) * mm, "end": v(119.23, -2.7) * mm});
            skLineSegment(sketch, "E1204.MirrorCS", {"start": v(122.97, -3.75) * mm, "end": v(120.3, -3.75) * mm});
            skLineSegment(sketch, "E1205.MirrorCS", {"start": v(127.03, -2.7) * mm, "end": v(127.03, -0.01) * mm});
            skPoint(sketch, "E1206.MirrorP", {"position": v(128.06, -9.85) * mm});
            skLineSegment(sketch, "E1207.MirrorCS", {"start": v(126.8, -8.6) * mm, "end": v(128, -9.8) * mm});
            skLineSegment(sketch, "E1208.MirrorCS", {"start": v(128.83, -8.25) * mm, "end": v(126.94, -8.25) * mm});
            skPoint(sketch, "E1209.MirrorP", {"position": v(113.13, -9.85) * mm});
            skCircle(sketch, "E1210", {"center": v(123.13, 0.15) * mm, "radius": 2.1 * mm});
            skLineSegment(sketch, "E1211", {"start": v(122.97, 4.05) * mm, "end": v(123.13, 3.89) * mm});
            skLineSegment(sketch, "E1212", {"start": v(123.13, 3.89) * mm, "end": v(123.29, 4.05) * mm});
            skPoint(sketch, "E1213.orphan", {"position": v(123.13, 4.05) * mm});
            skLineSegment(sketch, "E1214.MirrorCS", {"start": v(122.97, -3.75) * mm, "end": v(123.13, -3.6) * mm});
            skLineSegment(sketch, "E1215.MirrorCS", {"start": v(123.13, -3.6) * mm, "end": v(123.29, -3.75) * mm});
            skLineSegment(sketch, "E1216", {"start": v(119.23, 0.3) * mm, "end": v(119.39, 0.15) * mm});
            skLineSegment(sketch, "E1217", {"start": v(119.39, 0.15) * mm, "end": v(119.23, -0.01) * mm});
            skPoint(sketch, "E1218.orphan", {"position": v(119.23, 0.15) * mm});
            skLineSegment(sketch, "E1219.MirrorCS", {"start": v(126.87, 0.15) * mm, "end": v(127.03, -0.01) * mm});
            skLineSegment(sketch, "E1220.MirrorCS", {"start": v(127.03, 0.3) * mm, "end": v(126.87, 0.15) * mm});
            skPoint(sketch, "E1221.orphan", {"position": v(123.13, -3.75) * mm});
            skLineSegment(sketch, "E1222", {"start": v(123.25, 0.15) * mm, "end": v(95.87, 0.15) * mm, "construction": true});
            skLineSegment(sketch, "E1223.filletArc", {"start": v(119.81, -5.3) * mm, "end": v(119.81, -5.3) * mm});
            skPoint(sketch, "E1224.visualSharp", {"position": v(119.93, 8.55) * mm});
            skPoint(sketch, "E1225.orphan", {"position": v(123.25, 4.05) * mm});
            skPoint(sketch, "E1226.orphan", {"position": v(119.35, 0.15) * mm});
            skLineSegment(sketch, "E1227", {"start": v(122.97, -55.96) * mm, "end": v(120.3, -55.96) * mm});
            skLineSegment(sketch, "E1228", {"start": v(120.3, -55.96) * mm, "end": v(117.43, -53.1) * mm});
            skLineSegment(sketch, "E1229", {"start": v(117.43, -53.1) * mm, "end": v(117.43, -51.46) * mm});
            skLineSegment(sketch, "E1230", {"start": v(118.12, -49.86) * mm, "end": v(113.63, -49.86) * mm});
            skLineSegment(sketch, "E1231", {"start": v(116.37, -54.16) * mm, "end": v(119.23, -57.02) * mm});
            skLineSegment(sketch, "E1232", {"start": v(119.23, -57.02) * mm, "end": v(119.23, -59.7) * mm});
            skLineSegment(sketch, "E1233", {"start": v(123.13, -59.86) * mm, "end": v(123.13, -42.54) * mm, "construction": true});
            skLineSegment(sketch, "E1234", {"start": v(123.13, -59.86) * mm, "end": v(95.75, -59.86) * mm, "construction": true});
            skPoint(sketch, "E1235.visualSharp", {"position": v(113.13, -49.86) * mm});
            skLineSegment(sketch, "E1236.filletArc", {"start": v(113.38, -40.57) * mm, "end": v(113.38, -40.57) * mm});
            skLineSegment(sketch, "E1237", {"start": v(117.43, -51.46) * mm, "end": v(119.32, -51.46) * mm});
            skLineSegment(sketch, "E1238", {"start": v(119.46, -51.12) * mm, "end": v(118.26, -49.92) * mm});
            skArc(sketch, "E1239.filletArc", {"start": v(119.32, -51.46) * mm, "mid": v(119.5, -51.33) * mm, "end": v(119.46, -51.12) * mm});
            skPoint(sketch, "E1240.visualSharp", {"position": v(118.2, -49.86) * mm});
            skArc(sketch, "E1240.filletArc", {"start": v(118.26, -49.92) * mm, "mid": v(118.2, -49.87) * mm, "end": v(118.12, -49.86) * mm});
            skArc(sketch, "E1241.MirrorCS", {"start": v(131.87, -56.2) * mm, "mid": v(131.65, -56.23) * mm, "end": v(131.53, -56.05) * mm});
            skArc(sketch, "E1242.MirrorCS", {"start": v(133.13, -54.85) * mm, "mid": v(133.12, -54.93) * mm, "end": v(133.07, -55) * mm});
            skArc(sketch, "E1243.MirrorCS", {"start": v(128, -49.92) * mm, "mid": v(128.06, -49.87) * mm, "end": v(128.14, -49.86) * mm});
            skArc(sketch, "E1244.MirrorCS", {"start": v(126.94, -51.46) * mm, "mid": v(126.75, -51.33) * mm, "end": v(126.8, -51.12) * mm});
            skArc(sketch, "E1245.MirrorCS", {"start": v(132.63, -49.86) * mm, "mid": v(132.98, -50) * mm, "end": v(133.13, -50.36) * mm});
            skPoint(sketch, "E1246.MirrorP", {"position": v(131.53, -56.53) * mm});
            skLineSegment(sketch, "E1247.MirrorCS", {"start": v(126.8, -51.12) * mm, "end": v(128, -49.92) * mm});
            skLineSegment(sketch, "E1248.MirrorCS", {"start": v(129.9, -54.16) * mm, "end": v(127.03, -57.02) * mm});
            skLineSegment(sketch, "E1249.MirrorCS", {"start": v(127.03, -57.02) * mm, "end": v(127.03, -59.7) * mm});
            skLineSegment(sketch, "E1250.MirrorCS", {"start": v(133.13, -50.36) * mm, "end": v(133.13, -54.85) * mm});
            skLineSegment(sketch, "E1251.MirrorCS", {"start": v(123.29, -55.96) * mm, "end": v(125.97, -55.96) * mm});
            skPoint(sketch, "E1252.MirrorP", {"position": v(133.13, -54.93) * mm});
            skLineSegment(sketch, "E1253.MirrorCS", {"start": v(131.53, -56.05) * mm, "end": v(131.53, -54.16) * mm});
            skLineSegment(sketch, "E1254.MirrorCS", {"start": v(128.83, -51.46) * mm, "end": v(126.94, -51.46) * mm});
            skLineSegment(sketch, "E1255.MirrorCS", {"start": v(125.97, -55.96) * mm, "end": v(128.83, -53.1) * mm});
            skPoint(sketch, "E1256.MirrorP", {"position": v(126.46, -51.46) * mm});
            skLineSegment(sketch, "E1257.MirrorCS", {"start": v(131.53, -54.16) * mm, "end": v(129.9, -54.16) * mm});
            skPoint(sketch, "E1258.MirrorP", {"position": v(128.06, -49.86) * mm});
            skLineSegment(sketch, "E1259.MirrorCS", {"start": v(131.87, -56.2) * mm, "end": v(133.07, -55) * mm});
            skLineSegment(sketch, "E1260.MirrorCS", {"start": v(128.83, -53.1) * mm, "end": v(128.83, -51.46) * mm});
            skLineSegment(sketch, "E1261.MirrorCS", {"start": v(128.14, -49.86) * mm, "end": v(132.63, -49.86) * mm});
            skPoint(sketch, "E1262.MirrorP", {"position": v(133.13, -49.86) * mm});
            skArc(sketch, "E1263.MirrorCS", {"start": v(118.26, -69.8) * mm, "mid": v(118.2, -69.84) * mm, "end": v(118.12, -69.86) * mm});
            skArc(sketch, "E1264.MirrorCS", {"start": v(133.13, -64.87) * mm, "mid": v(133.12, -64.79) * mm, "end": v(133.07, -64.72) * mm});
            skArc(sketch, "E1265.MirrorCS", {"start": v(128, -69.8) * mm, "mid": v(128.06, -69.84) * mm, "end": v(128.14, -69.86) * mm});
            skArc(sketch, "E1266.MirrorCS", {"start": v(119.32, -68.26) * mm, "mid": v(119.5, -68.38) * mm, "end": v(119.46, -68.6) * mm});
            skArc(sketch, "E1267.MirrorCS", {"start": v(131.87, -63.52) * mm, "mid": v(131.65, -63.48) * mm, "end": v(131.53, -63.67) * mm});
            skArc(sketch, "E1268.MirrorCS", {"start": v(126.94, -68.26) * mm, "mid": v(126.75, -68.38) * mm, "end": v(126.8, -68.6) * mm});
            skArc(sketch, "E1269.MirrorCS", {"start": v(132.63, -69.86) * mm, "mid": v(132.98, -69.71) * mm, "end": v(133.13, -69.36) * mm});
            skLineSegment(sketch, "E1270.MirrorCS", {"start": v(119.46, -68.6) * mm, "end": v(118.26, -69.8) * mm});
            skLineSegment(sketch, "E1271.MirrorCS", {"start": v(117.43, -68.26) * mm, "end": v(119.32, -68.26) * mm});
            skLineSegment(sketch, "E1272.MirrorCS", {"start": v(131.53, -65.56) * mm, "end": v(129.9, -65.56) * mm});
            skLineSegment(sketch, "E1273.MirrorCS", {"start": v(131.87, -63.52) * mm, "end": v(133.07, -64.72) * mm});
            skLineSegment(sketch, "E1274.MirrorCS", {"start": v(123.13, -59.86) * mm, "end": v(123.13, -77.18) * mm, "construction": true});
            skLineSegment(sketch, "E1275.MirrorCS", {"start": v(128.83, -66.62) * mm, "end": v(128.83, -68.26) * mm});
            skLineSegment(sketch, "E1276.MirrorCS", {"start": v(119.23, -62.7) * mm, "end": v(119.23, -60.02) * mm});
            skLineSegment(sketch, "E1277.MirrorCS", {"start": v(128.14, -69.86) * mm, "end": v(132.63, -69.86) * mm});
            skLineSegment(sketch, "E1278.MirrorCS", {"start": v(125.97, -63.76) * mm, "end": v(128.83, -66.62) * mm});
            skPoint(sketch, "E1279.MirrorP", {"position": v(118.2, -69.86) * mm});
            skLineSegment(sketch, "E1280.MirrorCS", {"start": v(123.29, -63.76) * mm, "end": v(125.97, -63.76) * mm});
            skLineSegment(sketch, "E1281.MirrorCS", {"start": v(118.12, -69.86) * mm, "end": v(113.63, -69.86) * mm});
            skPoint(sketch, "E1282.MirrorP", {"position": v(133.13, -69.86) * mm});
            skLineSegment(sketch, "E1283.MirrorCS", {"start": v(120.3, -63.76) * mm, "end": v(117.43, -66.62) * mm});
            skLineSegment(sketch, "E1284.MirrorCS", {"start": v(129.9, -65.56) * mm, "end": v(127.03, -62.7) * mm});
            skLineSegment(sketch, "E1285.MirrorCS", {"start": v(133.13, -69.36) * mm, "end": v(133.13, -64.87) * mm});
            skPoint(sketch, "E1286.MirrorP", {"position": v(119.8, -68.26) * mm});
            skPoint(sketch, "E1287.MirrorP", {"position": v(126.46, -68.26) * mm});
            skLineSegment(sketch, "E1288.MirrorCS", {"start": v(131.53, -63.67) * mm, "end": v(131.53, -65.56) * mm});
            skPoint(sketch, "E1289.MirrorP", {"position": v(131.53, -63.18) * mm});
            skPoint(sketch, "E1290.MirrorP", {"position": v(133.13, -64.78) * mm});
            skLineSegment(sketch, "E1291.MirrorCS", {"start": v(117.43, -66.62) * mm, "end": v(117.43, -68.26) * mm});
            skLineSegment(sketch, "E1292.MirrorCS", {"start": v(116.37, -65.56) * mm, "end": v(119.23, -62.7) * mm});
            skLineSegment(sketch, "E1293.MirrorCS", {"start": v(122.97, -63.76) * mm, "end": v(120.3, -63.76) * mm});
            skLineSegment(sketch, "E1294.MirrorCS", {"start": v(127.03, -62.7) * mm, "end": v(127.03, -60.02) * mm});
            skPoint(sketch, "E1295.MirrorP", {"position": v(128.06, -69.86) * mm});
            skLineSegment(sketch, "E1296.MirrorCS", {"start": v(126.8, -68.6) * mm, "end": v(128, -69.8) * mm});
            skLineSegment(sketch, "E1297.MirrorCS", {"start": v(128.83, -68.26) * mm, "end": v(126.94, -68.26) * mm});
            skCircle(sketch, "E1298", {"center": v(123.13, -59.86) * mm, "radius": 2.1 * mm});
            skLineSegment(sketch, "E1299", {"start": v(122.97, -55.96) * mm, "end": v(123.13, -56.12) * mm});
            skLineSegment(sketch, "E1300", {"start": v(123.13, -56.12) * mm, "end": v(123.29, -55.96) * mm});
            skPoint(sketch, "E1301.orphan", {"position": v(123.13, -55.96) * mm});
            skLineSegment(sketch, "E1302.MirrorCS", {"start": v(122.97, -63.76) * mm, "end": v(123.13, -63.6) * mm});
            skLineSegment(sketch, "E1303.MirrorCS", {"start": v(123.13, -63.6) * mm, "end": v(123.29, -63.76) * mm});
            skLineSegment(sketch, "E1304", {"start": v(119.23, -59.7) * mm, "end": v(119.39, -59.86) * mm});
            skLineSegment(sketch, "E1305", {"start": v(119.39, -59.86) * mm, "end": v(119.23, -60.02) * mm});
            skPoint(sketch, "E1306.orphan", {"position": v(119.23, -59.86) * mm});
            skLineSegment(sketch, "E1307.MirrorCS", {"start": v(126.87, -59.86) * mm, "end": v(127.03, -60.02) * mm});
            skLineSegment(sketch, "E1308.MirrorCS", {"start": v(127.03, -59.7) * mm, "end": v(126.87, -59.86) * mm});
            skPoint(sketch, "E1309.orphan", {"position": v(123.13, -63.76) * mm});
            skLineSegment(sketch, "E1310", {"start": v(123.25, -59.86) * mm, "end": v(95.87, -59.86) * mm, "construction": true});
            skLineSegment(sketch, "E1311.filletArc", {"start": v(113.5, -40.57) * mm, "end": v(113.5, -40.57) * mm});
            skPoint(sketch, "E1312.visualSharp", {"position": v(119.93, -51.46) * mm});
            skPoint(sketch, "E1313.orphan", {"position": v(123.25, -55.96) * mm});
            skPoint(sketch, "E1314.orphan", {"position": v(119.35, -59.86) * mm});
            skLineSegment(sketch, "E1315", {"start": v(113.63, -49.86) * mm, "end": v(113.13, -49.86) * mm});
            skLineSegment(sketch, "E1316", {"start": v(113.63, -9.85) * mm, "end": v(113.13, -9.85) * mm});
            skLineSegment(sketch, "E1317", {"start": v(115.93, -51.46) * mm, "end": v(112.6, -51.46) * mm});
            skLineSegment(sketch, "E1318", {"start": v(107.03, -57.02) * mm, "end": v(112.6, -51.46) * mm});
            skLineSegment(sketch, "E1319", {"start": v(115.93, -51.46) * mm, "end": v(115.93, -53.72) * mm});
            skLineSegment(sketch, "E1320", {"start": v(119.23, -57.02) * mm, "end": v(115.93, -53.72) * mm});
            skLineSegment(sketch, "E1321", {"start": v(113.13, -49.36) * mm, "end": v(113.13, -49.86) * mm});
            skPoint(sketch, "E1322.end.orphan", {"position": v(114.73, -54.16) * mm});
            skLineSegment(sketch, "E1323", {"start": v(105.97, -55.96) * mm, "end": v(111.53, -50.4) * mm});
            skLineSegment(sketch, "E1324", {"start": v(111.53, -47.06) * mm, "end": v(109.27, -47.06) * mm});
            skLineSegment(sketch, "E1325", {"start": v(105.97, -43.76) * mm, "end": v(109.27, -47.06) * mm});
            skLineSegment(sketch, "E1326", {"start": v(111.53, -47.06) * mm, "end": v(111.53, -50.4) * mm});
            skLineSegment(sketch, "E1327", {"start": v(113.63, -69.86) * mm, "end": v(112.63, -69.86) * mm});
            skLineSegment(sketch, "E1328", {"start": v(110.33, -68.26) * mm, "end": v(115.88, -68.26) * mm});
            skLineSegment(sketch, "E1329", {"start": v(115.88, -68.26) * mm, "end": v(115.88, -66.04) * mm});
            skLineSegment(sketch, "E1330", {"start": v(110.33, -68.26) * mm, "end": v(110.33, -66) * mm});
            skLineSegment(sketch, "E1331", {"start": v(107.03, -62.7) * mm, "end": v(110.33, -66) * mm});
            skLineSegment(sketch, "E1332", {"start": v(119.23, -62.7) * mm, "end": v(115.88, -66.04) * mm});
            skLineSegment(sketch, "E1333", {"start": v(110.33, 8.55) * mm, "end": v(115.93, 8.55) * mm});
            skLineSegment(sketch, "E1334", {"start": v(115.93, -8.25) * mm, "end": v(113.13, -8.25) * mm});
            skLineSegment(sketch, "E1335", {"start": v(107.03, -2.7) * mm, "end": v(112.6, -8.25) * mm});
            skLineSegment(sketch, "E1336", {"start": v(119.23, -2.7) * mm, "end": v(115.93, -6) * mm});
            skLineSegment(sketch, "E1337", {"start": v(115.93, -8.25) * mm, "end": v(115.93, -6) * mm});
            skLineSegment(sketch, "E1338", {"start": v(105.97, -3.75) * mm, "end": v(111.53, -9.32) * mm});
            skLineSegment(sketch, "E1339", {"start": v(111.53, -12.66) * mm, "end": v(109.27, -12.66) * mm});
            skLineSegment(sketch, "E1340", {"start": v(105.97, -15.95) * mm, "end": v(109.27, -12.65) * mm});
            skPoint(sketch, "E1340.endSnap0", {"position": v(109.27, -12.66) * mm});
            skPoint(sketch, "E1341.orphan", {"position": v(107.01, -12.66) * mm});
            skLineSegment(sketch, "E1342.trimOffspring", {"start": v(111.53, -9.32) * mm, "end": v(111.53, -12.66) * mm});
            skLineSegment(sketch, "E1343", {"start": v(112.6, -8.25) * mm, "end": v(113.13, -8.25) * mm});
            skLineSegment(sketch, "E1344", {"start": v(108.14, 10.15) * mm, "end": v(118.12, 10.15) * mm});
            skLineSegment(sketch, "E1345", {"start": v(119.23, 2.99) * mm, "end": v(115.93, 6.29) * mm});
            skLineSegment(sketch, "E1346", {"start": v(107.03, 2.99) * mm, "end": v(110.33, 6.29) * mm});
            skLineSegment(sketch, "E1347", {"start": v(110.33, 8.55) * mm, "end": v(110.33, 6.29) * mm});
            skLineSegment(sketch, "E1348", {"start": v(115.93, 8.55) * mm, "end": v(115.93, 6.29) * mm});
            skPoint(sketch, "E1349.MirrorCS.start.orphan", {"position": v(113.13, 9.65) * mm});
            skSolve(sketch);
        }
        {
            var Q0;
            Q0=makeQuery(id+"F0.imprint","IMPRINT",FACE,{"disambiguationData":[TD([[makeQuery(id+"F0.imprint","IMPRINT",EDGE,{"derivedFrom":sQuery(id+"F0.wireOp",EDGE,"E0")}),1.0]])]});
            extrude(context, id + "F5", {"entities" : qUnion([Q0]), "depth" : 100 * mm, "offsetDistance" : 25 * mm});
        }
        {
            var Q0;
            Q0=makeQuery(id+"F1.imprint","IMPRINT",FACE,{"disambiguationData":[TD([[makeQuery(id+"F1.imprint","IMPRINT",EDGE,{"derivedFrom":sQuery(id+"F1.wireOp",EDGE,"E104")}),1.0]])]});
            extrude(context, id + "F6", {"entities" : qUnion([Q0]), "depth" : 100 * mm, "offsetDistance" : 25 * mm});
        }
        {
            var Q0;
            Q0=makeQuery(id+"F2.imprint","IMPRINT",FACE,{"disambiguationData":[TD([[makeQuery(id+"F2.imprint","IMPRINT",EDGE,{"derivedFrom":sQuery(id+"F2.wireOp",EDGE,"E284")}),1.0]])]});
            extrude(context, id + "F7", {"entities" : qUnion([Q0]), "depth" : 100 * mm, "offsetDistance" : 25 * mm});
        }
        {
            var Q0;
            Q0=makeQuery(id+"F3.imprint","IMPRINT",FACE,{"disambiguationData":[TD([[makeQuery(id+"F3.imprint","IMPRINT",EDGE,{"derivedFrom":sQuery(id+"F3.wireOp",EDGE,"E534")}),1.0]])]});
            extrude(context, id + "F8", {"entities" : qUnion([Q0]), "depth" : 100 * mm, "offsetDistance" : 25 * mm});
        }
        {
            var Q0;
            Q0=makeQuery(id+"F6.opExtrude","SWEPT_FACE",FACE,{"disambiguationData":[OSD([sQuery(id+"F1.wireOp",EDGE,"E169.MirrorCS"),sQuery(id+"F1.wireOp",EDGE,"E257.MirrorCS"),sQuery(id+"F1.wireOp",EDGE,"E276")])]});
            var Q1;
            Q1=makeQuery(id+"F7.opExtrude","SWEPT_FACE",FACE,{"disambiguationData":[OSD([sQuery(id+"F2.wireOp",EDGE,"E349.MirrorCS"),sQuery(id+"F2.wireOp",EDGE,"E393.MirrorCS"),sQuery(id+"F2.wireOp",EDGE,"E403")])]});
            var Q2;
            Q2=makeQuery(id+"F7.opExtrude","SWEPT_FACE",FACE,{"disambiguationData":[OSD([sQuery(id+"F2.wireOp",EDGE,"E455.MirrorCS"),sQuery(id+"F2.wireOp",EDGE,"E466.MirrorCS"),sQuery(id+"F2.wireOp",EDGE,"E519.MirrorCS")])]});
            var Q3;
            Q3=makeQuery(id+"F8.opExtrude","SWEPT_FACE",FACE,{"disambiguationData":[OSD([sQuery(id+"F3.wireOp",EDGE,"E599.MirrorCS"),sQuery(id+"F3.wireOp",EDGE,"E673.MirrorCS"),sQuery(id+"F3.wireOp",EDGE,"E690")])]});
            var Q4;
            Q4=makeQuery(id+"F8.opExtrude","SWEPT_FACE",FACE,{"disambiguationData":[OSD([sQuery(id+"F3.wireOp",EDGE,"E643.MirrorCS"),sQuery(id+"F3.wireOp",EDGE,"E774.MirrorCS"),sQuery(id+"F3.wireOp",EDGE,"E853")])]});
            var Q5;
            Q5=makeQuery(id+"F8.opExtrude","SWEPT_FACE",FACE,{"disambiguationData":[OSD([sQuery(id+"F3.wireOp",EDGE,"E771.MirrorCS"),sQuery(id+"F3.wireOp",EDGE,"E781.MirrorCS"),sQuery(id+"F3.wireOp",EDGE,"E783.MirrorCS")])]});
            extrude(context, id + "F9", {"entities" : qUnion([Q0, Q1, Q2, Q3, Q4, Q5]), "operationType" : NewBodyOperationType.REMOVE, "oppositeDirection" : true, "depth" : 2.5 * mm, "offsetDistance" : 25 * mm});
        }
        {
            var Q0;
            Q0=makeQuery(id+"F8.opExtrude","SWEPT_FACE",FACE,{"disambiguationData":[OSD([sQuery(id+"F3.wireOp",EDGE,"E585.MirrorCS"),sQuery(id+"F3.wireOp",EDGE,"E677.MirrorCS"),sQuery(id+"F3.wireOp",EDGE,"E691")])]});
            var Q1;
            Q1=makeQuery(id+"F8.opExtrude","SWEPT_FACE",FACE,{"disambiguationData":[OSD([sQuery(id+"F3.wireOp",EDGE,"E640.MirrorCS"),sQuery(id+"F3.wireOp",EDGE,"E755.MirrorCS"),sQuery(id+"F3.wireOp",EDGE,"E854")])]});
            var Q2;
            Q2=makeQuery(id+"F8.opExtrude","SWEPT_FACE",FACE,{"disambiguationData":[OSD([sQuery(id+"F3.wireOp",EDGE,"E766.MirrorCS"),sQuery(id+"F3.wireOp",EDGE,"E782.MirrorCS"),sQuery(id+"F3.wireOp",EDGE,"E825.MirrorCS")])]});
            var Q3;
            Q3=makeQuery(id+"F7.opExtrude","SWEPT_FACE",FACE,{"disambiguationData":[OSD([sQuery(id+"F2.wireOp",EDGE,"E461.MirrorCS"),sQuery(id+"F2.wireOp",EDGE,"E464.MirrorCS"),sQuery(id+"F2.wireOp",EDGE,"E530.MirrorCS")])]});
            var Q4;
            Q4=makeQuery(id+"F7.opExtrude","SWEPT_FACE",FACE,{"disambiguationData":[OSD([sQuery(id+"F2.wireOp",EDGE,"E335.MirrorCS"),sQuery(id+"F2.wireOp",EDGE,"E397.MirrorCS"),sQuery(id+"F2.wireOp",EDGE,"E404")])]});
            var Q5;
            Q5=makeQuery(id+"F6.opExtrude","SWEPT_FACE",FACE,{"disambiguationData":[OSD([sQuery(id+"F1.wireOp",EDGE,"E155.MirrorCS"),sQuery(id+"F1.wireOp",EDGE,"E262.MirrorCS"),sQuery(id+"F1.wireOp",EDGE,"E277")])]});
            extrude(context, id + "F10", {"entities" : qUnion([Q0, Q1, Q2, Q3, Q4, Q5]), "operationType" : NewBodyOperationType.REMOVE, "oppositeDirection" : true, "depth" : 2.5 * mm, "offsetDistance" : 25 * mm});
        }
        {
            var Q0;
            Q0=makeQuery(id+"F4.imprint","IMPRINT",FACE,{"disambiguationData":[TD([[makeQuery(id+"F4.imprint","IMPRINT",EDGE,{"derivedFrom":sQuery(id+"F4.wireOp",EDGE,"E857")}),1.0]])]});
            extrude(context, id + "F11", {"entities" : qUnion([Q0]), "depth" : 100 * mm, "offsetDistance" : 25 * mm});
        }
        {
            var Q0;
            Q0=makeQuery(id+"F11.opExtrude","SWEPT_FACE",FACE,{"disambiguationData":[OSD([sQuery(id+"F4.wireOp",EDGE,"E1064.MirrorCS"),sQuery(id+"F4.wireOp",EDGE,"E1072.MirrorCS"),sQuery(id+"F4.wireOp",EDGE,"E1073.MirrorCS")])]});
            var Q1;
            Q1=makeQuery(id+"F11.opExtrude","SWEPT_FACE",FACE,{"disambiguationData":[OSD([sQuery(id+"F4.wireOp",EDGE,"E948.MirrorCS"),sQuery(id+"F4.wireOp",EDGE,"E1067.MirrorCS"),sQuery(id+"F4.wireOp",EDGE,"E1135")])]});
            var Q2;
            Q2=makeQuery(id+"F11.opExtrude","SWEPT_FACE",FACE,{"disambiguationData":[OSD([sQuery(id+"F4.wireOp",EDGE,"E904.MirrorCS"),sQuery(id+"F4.wireOp",EDGE,"E978.MirrorCS"),sQuery(id+"F4.wireOp",EDGE,"E994")])]});
            extrude(context, id + "F12", {"entities" : qUnion([Q0, Q1, Q2]), "operationType" : NewBodyOperationType.REMOVE, "oppositeDirection" : true, "depth" : 2.5 * mm, "offsetDistance" : 25 * mm});
        }
        {
            var Q0;
            Q0=makeQuery(id+"F11.opExtrude","SWEPT_BODY",BODY,{"disambiguationData":[OSD([sQuery(id+"F4.wireOp",EDGE,"E857"),sQuery(id+"F4.wireOp",EDGE,"E858"),sQuery(id+"F4.wireOp",EDGE,"E859"),sQuery(id+"F4.wireOp",EDGE,"E860"),sQuery(id+"F4.wireOp",EDGE,"E861"),sQuery(id+"F4.wireOp",EDGE,"E862"),sQuery(id+"F4.wireOp",EDGE,"E863"),sQuery(id+"F4.wireOp",EDGE,"E864"),sQuery(id+"F4.wireOp",EDGE,"E865"),sQuery(id+"F4.wireOp",EDGE,"E868.filletArc"),sQuery(id+"F4.wireOp",EDGE,"E870"),sQuery(id+"F4.wireOp",EDGE,"E871"),sQuery(id+"F4.wireOp",EDGE,"E872"),sQuery(id+"F4.wireOp",EDGE,"E873.filletArc"),sQuery(id+"F4.wireOp",EDGE,"E874.filletArc"),sQuery(id+"F4.wireOp",EDGE,"E875.filletArc"),sQuery(id+"F4.wireOp",EDGE,"E876.filletArc"),sQuery(id+"F4.wireOp",EDGE,"E877.MirrorCS"),sQuery(id+"F4.wireOp",EDGE,"E878.MirrorCS"),sQuery(id+"F4.wireOp",EDGE,"E880.MirrorCS"),sQuery(id+"F4.wireOp",EDGE,"E882.MirrorCS"),sQuery(id+"F4.wireOp",EDGE,"E883.MirrorCS"),sQuery(id+"F4.wireOp",EDGE,"E884.MirrorCS"),sQuery(id+"F4.wireOp",EDGE,"E885.MirrorCS"),sQuery(id+"F4.wireOp",EDGE,"E888.MirrorCS"),sQuery(id+"F4.wireOp",EDGE,"E891.MirrorCS"),sQuery(id+"F4.wireOp",EDGE,"E892.MirrorCS"),sQuery(id+"F4.wireOp",EDGE,"E893.MirrorCS"),sQuery(id+"F4.wireOp",EDGE,"E895.MirrorCS"),sQuery(id+"F4.wireOp",EDGE,"E898.MirrorCS"),sQuery(id+"F4.wireOp",EDGE,"E899.MirrorCS"),sQuery(id+"F4.wireOp",EDGE,"E901.MirrorCS"),sQuery(id+"F4.wireOp",EDGE,"E902.MirrorCS"),sQuery(id+"F4.wireOp",EDGE,"E903.MirrorCS"),sQuery(id+"F4.wireOp",EDGE,"E904.MirrorCS"),sQuery(id+"F4.wireOp",EDGE,"E905.MirrorCS"),sQuery(id+"F4.wireOp",EDGE,"E906.MirrorCS"),sQuery(id+"F4.wireOp",EDGE,"E907.MirrorCS"),sQuery(id+"F4.wireOp",EDGE,"E912"),sQuery(id+"F4.wireOp",EDGE,"E913"),sQuery(id+"F4.wireOp",EDGE,"E914"),sQuery(id+"F4.wireOp",EDGE,"E916.MirrorCS"),sQuery(id+"F4.wireOp",EDGE,"E917.MirrorCS"),sQuery(id+"F4.wireOp",EDGE,"E918"),sQuery(id+"F4.wireOp",EDGE,"E919"),sQuery(id+"F4.wireOp",EDGE,"E921.MirrorCS"),sQuery(id+"F4.wireOp",EDGE,"E922.MirrorCS"),sQuery(id+"F4.wireOp",EDGE,"E925.MirrorCS"),sQuery(id+"F4.wireOp",EDGE,"E926.MirrorCS"),sQuery(id+"F4.wireOp",EDGE,"E927.MirrorCS"),sQuery(id+"F4.wireOp",EDGE,"E928.MirrorCS"),sQuery(id+"F4.wireOp",EDGE,"E929.MirrorCS"),sQuery(id+"F4.wireOp",EDGE,"E930.MirrorCS"),sQuery(id+"F4.wireOp",EDGE,"E931.MirrorCS"),sQuery(id+"F4.wireOp",EDGE,"E932.MirrorCS"),sQuery(id+"F4.wireOp",EDGE,"E933.MirrorCS"),sQuery(id+"F4.wireOp",EDGE,"E934.MirrorCS"),sQuery(id+"F4.wireOp",EDGE,"E935.MirrorCS"),sQuery(id+"F4.wireOp",EDGE,"E936.MirrorCS"),sQuery(id+"F4.wireOp",EDGE,"E937.MirrorCS"),sQuery(id+"F4.wireOp",EDGE,"E938.MirrorCS"),sQuery(id+"F4.wireOp",EDGE,"E939.MirrorCS"),sQuery(id+"F4.wireOp",EDGE,"E940.MirrorCS"),sQuery(id+"F4.wireOp",EDGE,"E941.MirrorCS"),sQuery(id+"F4.wireOp",EDGE,"E942.MirrorCS"),sQuery(id+"F4.wireOp",EDGE,"E943.MirrorCS"),sQuery(id+"F4.wireOp",EDGE,"E944.MirrorCS"),sQuery(id+"F4.wireOp",EDGE,"E945.MirrorCS"),sQuery(id+"F4.wireOp",EDGE,"E946.MirrorCS"),sQuery(id+"F4.wireOp",EDGE,"E947.MirrorCS"),sQuery(id+"F4.wireOp",EDGE,"E948.MirrorCS"),sQuery(id+"F4.wireOp",EDGE,"E949.MirrorCS"),sQuery(id+"F4.wireOp",EDGE,"E950.MirrorCS"),sQuery(id+"F4.wireOp",EDGE,"E951.MirrorCS"),sQuery(id+"F4.wireOp",EDGE,"E960.MirrorCS"),sQuery(id+"F4.wireOp",EDGE,"E961.MirrorCS"),sQuery(id+"F4.wireOp",EDGE,"E962.MirrorCS"),sQuery(id+"F4.wireOp",EDGE,"E964.MirrorCS"),sQuery(id+"F4.wireOp",EDGE,"E965.MirrorCS"),sQuery(id+"F4.wireOp",EDGE,"E966.MirrorCS"),sQuery(id+"F4.wireOp",EDGE,"E967.MirrorCS"),sQuery(id+"F4.wireOp",EDGE,"E970.MirrorCS"),sQuery(id+"F4.wireOp",EDGE,"E972.MirrorCS"),sQuery(id+"F4.wireOp",EDGE,"E973.MirrorCS"),sQuery(id+"F4.wireOp",EDGE,"E974.MirrorC"),sQuery(id+"F4.wireOp",EDGE,"E976.MirrorCS"),sQuery(id+"F4.wireOp",EDGE,"E978.MirrorCS"),sQuery(id+"F4.wireOp",EDGE,"E979.MirrorCS"),sQuery(id+"F4.wireOp",EDGE,"E980.MirrorCS"),sQuery(id+"F4.wireOp",EDGE,"E982.MirrorCS"),sQuery(id+"F4.wireOp",EDGE,"E983.MirrorCS"),sQuery(id+"F4.wireOp",EDGE,"E984.MirrorCS"),sQuery(id+"F4.wireOp",EDGE,"E987.MirrorCS"),sQuery(id+"F4.wireOp",EDGE,"E988.MirrorCS"),sQuery(id+"F4.wireOp",EDGE,"E990.MirrorCS"),sQuery(id+"F4.wireOp",EDGE,"E991.MirrorCS"),sQuery(id+"F4.wireOp",EDGE,"E992.MirrorCS"),sQuery(id+"F4.wireOp",EDGE,"E993.MirrorCS"),sQuery(id+"F4.wireOp",EDGE,"E994"),sQuery(id+"F4.wireOp",EDGE,"E995"),sQuery(id+"F4.wireOp",EDGE,"E996"),sQuery(id+"F4.wireOp",EDGE,"E997.MirrorCS"),sQuery(id+"F4.wireOp",EDGE,"E998.MirrorCS"),sQuery(id+"F4.wireOp",EDGE,"E999.MirrorCS"),sQuery(id+"F4.wireOp",EDGE,"E1000.MirrorCS"),sQuery(id+"F4.wireOp",EDGE,"E1001.MirrorCS"),sQuery(id+"F4.wireOp",EDGE,"E1002.MirrorCS"),sQuery(id+"F4.wireOp",EDGE,"E1003.MirrorCS"),sQuery(id+"F4.wireOp",EDGE,"E1004.MirrorCS"),sQuery(id+"F4.wireOp",EDGE,"E1005.MirrorCS"),sQuery(id+"F4.wireOp",EDGE,"E1006.MirrorCS"),sQuery(id+"F4.wireOp",EDGE,"E1007.MirrorCS"),sQuery(id+"F4.wireOp",EDGE,"E1008.MirrorCS"),sQuery(id+"F4.wireOp",EDGE,"E1009.MirrorCS"),sQuery(id+"F4.wireOp",EDGE,"E1010.MirrorCS"),sQuery(id+"F4.wireOp",EDGE,"E1011.MirrorCS"),sQuery(id+"F4.wireOp",EDGE,"E1012.MirrorCS"),sQuery(id+"F4.wireOp",EDGE,"E1013.MirrorCS"),sQuery(id+"F4.wireOp",EDGE,"E1014.MirrorCS"),sQuery(id+"F4.wireOp",EDGE,"E1015.MirrorCS"),sQuery(id+"F4.wireOp",EDGE,"E1016.MirrorCS"),sQuery(id+"F4.wireOp",EDGE,"E1017.MirrorCS"),sQuery(id+"F4.wireOp",EDGE,"E1018.MirrorCS"),sQuery(id+"F4.wireOp",EDGE,"E1019.MirrorCS"),sQuery(id+"F4.wireOp",EDGE,"E1020.MirrorCS"),sQuery(id+"F4.wireOp",EDGE,"E1021.MirrorCS"),sQuery(id+"F4.wireOp",EDGE,"E1022.MirrorCS"),sQuery(id+"F4.wireOp",EDGE,"E1023.MirrorCS"),sQuery(id+"F4.wireOp",EDGE,"E1024.MirrorCS"),sQuery(id+"F4.wireOp",EDGE,"E1025.MirrorCS"),sQuery(id+"F4.wireOp",EDGE,"E1026.MirrorCS"),sQuery(id+"F4.wireOp",EDGE,"E1027.MirrorCS"),sQuery(id+"F4.wireOp",EDGE,"E1028.MirrorCS"),sQuery(id+"F4.wireOp",EDGE,"E1029.MirrorCS"),sQuery(id+"F4.wireOp",EDGE,"E1030.MirrorCS"),sQuery(id+"F4.wireOp",EDGE,"E1031.MirrorCS"),sQuery(id+"F4.wireOp",EDGE,"E1032.MirrorCS"),sQuery(id+"F4.wireOp",EDGE,"E1033.MirrorCS"),sQuery(id+"F4.wireOp",EDGE,"E1034.MirrorCS"),sQuery(id+"F4.wireOp",EDGE,"E1035.MirrorCS"),sQuery(id+"F4.wireOp",EDGE,"E1036.MirrorCS"),sQuery(id+"F4.wireOp",EDGE,"E1037.MirrorCS"),sQuery(id+"F4.wireOp",EDGE,"E1038.MirrorCS"),sQuery(id+"F4.wireOp",EDGE,"E1039.MirrorCS"),sQuery(id+"F4.wireOp",EDGE,"E1040.MirrorCS"),sQuery(id+"F4.wireOp",EDGE,"E1041.MirrorCS"),sQuery(id+"F4.wireOp",EDGE,"E1042.MirrorCS"),sQuery(id+"F4.wireOp",EDGE,"E1043.MirrorCS"),sQuery(id+"F4.wireOp",EDGE,"E1044.MirrorCS"),sQuery(id+"F4.wireOp",EDGE,"E1045.MirrorCS"),sQuery(id+"F4.wireOp",EDGE,"E1046.MirrorCS"),sQuery(id+"F4.wireOp",EDGE,"E1047.MirrorCS"),sQuery(id+"F4.wireOp",EDGE,"E1048.MirrorCS"),sQuery(id+"F4.wireOp",EDGE,"E1049.MirrorCS"),sQuery(id+"F4.wireOp",EDGE,"E1050.MirrorCS"),sQuery(id+"F4.wireOp",EDGE,"E1051.MirrorCS"),sQuery(id+"F4.wireOp",EDGE,"E1052.MirrorCS"),sQuery(id+"F4.wireOp",EDGE,"E1053.MirrorCS"),sQuery(id+"F4.wireOp",EDGE,"E1054.MirrorCS"),sQuery(id+"F4.wireOp",EDGE,"E1055.MirrorCS"),sQuery(id+"F4.wireOp",EDGE,"E1056.MirrorCS"),sQuery(id+"F4.wireOp",EDGE,"E1057.MirrorCS"),sQuery(id+"F4.wireOp",EDGE,"E1058.MirrorCS"),sQuery(id+"F4.wireOp",EDGE,"E1059.MirrorCS"),sQuery(id+"F4.wireOp",EDGE,"E1060.MirrorCS"),sQuery(id+"F4.wireOp",EDGE,"E1061.MirrorCS"),sQuery(id+"F4.wireOp",EDGE,"E1062.MirrorCS"),sQuery(id+"F4.wireOp",EDGE,"E1063.MirrorCS"),sQuery(id+"F4.wireOp",EDGE,"E1064.MirrorCS"),sQuery(id+"F4.wireOp",EDGE,"E1065.MirrorCS"),sQuery(id+"F4.wireOp",EDGE,"E1066.MirrorCS"),sQuery(id+"F4.wireOp",EDGE,"E1067.MirrorCS"),sQuery(id+"F4.wireOp",EDGE,"E1068.MirrorCS"),sQuery(id+"F4.wireOp",EDGE,"E1069.MirrorCS"),sQuery(id+"F4.wireOp",EDGE,"E1070.MirrorCS"),sQuery(id+"F4.wireOp",EDGE,"E1071.MirrorCS"),sQuery(id+"F4.wireOp",EDGE,"E1072.MirrorCS"),sQuery(id+"F4.wireOp",EDGE,"E1073.MirrorCS"),sQuery(id+"F4.wireOp",EDGE,"E1074.MirrorCS"),sQuery(id+"F4.wireOp",EDGE,"E1075.MirrorCS"),sQuery(id+"F4.wireOp",EDGE,"E1081.MirrorCS"),sQuery(id+"F4.wireOp",EDGE,"E1084.MirrorCS"),sQuery(id+"F4.wireOp",EDGE,"E1089.MirrorCS"),sQuery(id+"F4.wireOp",EDGE,"E1090.MirrorCS"),sQuery(id+"F4.wireOp",EDGE,"E1096.MirrorCS"),sQuery(id+"F4.wireOp",EDGE,"E1097.MirrorCS"),sQuery(id+"F4.wireOp",EDGE,"E1098.MirrorCS"),sQuery(id+"F4.wireOp",EDGE,"E1099.MirrorCS"),sQuery(id+"F4.wireOp",EDGE,"E1100.MirrorCS"),sQuery(id+"F4.wireOp",EDGE,"E1101.MirrorCS"),sQuery(id+"F4.wireOp",EDGE,"E1102.MirrorC"),sQuery(id+"F4.wireOp",EDGE,"E1107.MirrorCS"),sQuery(id+"F4.wireOp",EDGE,"E1114.MirrorCS"),sQuery(id+"F4.wireOp",EDGE,"E1116.MirrorCS"),sQuery(id+"F4.wireOp",EDGE,"E1117.MirrorCS"),sQuery(id+"F4.wireOp",EDGE,"E1119.MirrorCS"),sQuery(id+"F4.wireOp",EDGE,"E1122.MirrorCS"),sQuery(id+"F4.wireOp",EDGE,"E1127.MirrorC"),sQuery(id+"F4.wireOp",EDGE,"E1129.MirrorCS"),sQuery(id+"F4.wireOp",EDGE,"E1131.MirrorCS"),sQuery(id+"F4.wireOp",EDGE,"E1132.MirrorCS"),sQuery(id+"F4.wireOp",EDGE,"E1133.MirrorCS"),sQuery(id+"F4.wireOp",EDGE,"E1135"),sQuery(id+"F4.wireOp",EDGE,"E1136"),sQuery(id+"F4.wireOp",EDGE,"E1137"),sQuery(id+"F4.wireOp",EDGE,"E1138"),sQuery(id+"F4.wireOp",EDGE,"E1139"),sQuery(id+"F4.wireOp",EDGE,"E1140"),sQuery(id+"F4.wireOp",EDGE,"E1141"),sQuery(id+"F4.wireOp",EDGE,"E1144"),sQuery(id+"F4.wireOp",EDGE,"E1148"),sQuery(id+"F4.wireOp",EDGE,"E1149"),sQuery(id+"F4.wireOp",EDGE,"E1150.filletArc"),sQuery(id+"F4.wireOp",EDGE,"E1151.filletArc"),sQuery(id+"F4.wireOp",EDGE,"E1152.MirrorCS"),sQuery(id+"F4.wireOp",EDGE,"E1153.MirrorCS"),sQuery(id+"F4.wireOp",EDGE,"E1154.MirrorCS"),sQuery(id+"F4.wireOp",EDGE,"E1155.MirrorCS"),sQuery(id+"F4.wireOp",EDGE,"E1156.MirrorCS"),sQuery(id+"F4.wireOp",EDGE,"E1158.MirrorCS"),sQuery(id+"F4.wireOp",EDGE,"E1159.MirrorCS"),sQuery(id+"F4.wireOp",EDGE,"E1160.MirrorCS"),sQuery(id+"F4.wireOp",EDGE,"E1161.MirrorCS"),sQuery(id+"F4.wireOp",EDGE,"E1162.MirrorCS"),sQuery(id+"F4.wireOp",EDGE,"E1164.MirrorCS"),sQuery(id+"F4.wireOp",EDGE,"E1165.MirrorCS"),sQuery(id+"F4.wireOp",EDGE,"E1166.MirrorCS"),sQuery(id+"F4.wireOp",EDGE,"E1168.MirrorCS"),sQuery(id+"F4.wireOp",EDGE,"E1170.MirrorCS"),sQuery(id+"F4.wireOp",EDGE,"E1171.MirrorCS"),sQuery(id+"F4.wireOp",EDGE,"E1172.MirrorCS"),sQuery(id+"F4.wireOp",EDGE,"E1174.MirrorCS"),sQuery(id+"F4.wireOp",EDGE,"E1175.MirrorCS"),sQuery(id+"F4.wireOp",EDGE,"E1176.MirrorCS"),sQuery(id+"F4.wireOp",EDGE,"E1177.MirrorCS"),sQuery(id+"F4.wireOp",EDGE,"E1178.MirrorCS"),sQuery(id+"F4.wireOp",EDGE,"E1179.MirrorCS"),sQuery(id+"F4.wireOp",EDGE,"E1180.MirrorCS"),sQuery(id+"F4.wireOp",EDGE,"E1181.MirrorCS"),sQuery(id+"F4.wireOp",EDGE,"E1182.MirrorCS"),sQuery(id+"F4.wireOp",EDGE,"E1183.MirrorCS"),sQuery(id+"F4.wireOp",EDGE,"E1184.MirrorCS"),sQuery(id+"F4.wireOp",EDGE,"E1186.MirrorCS"),sQuery(id+"F4.wireOp",EDGE,"E1187.MirrorCS"),sQuery(id+"F4.wireOp",EDGE,"E1188.MirrorCS"),sQuery(id+"F4.wireOp",EDGE,"E1189.MirrorCS"),sQuery(id+"F4.wireOp",EDGE,"E1191.MirrorCS"),sQuery(id+"F4.wireOp",EDGE,"E1192.MirrorCS"),sQuery(id+"F4.wireOp",EDGE,"E1194.MirrorCS"),sQuery(id+"F4.wireOp",EDGE,"E1195.MirrorCS"),sQuery(id+"F4.wireOp",EDGE,"E1196.MirrorCS"),sQuery(id+"F4.wireOp",EDGE,"E1199.MirrorCS"),sQuery(id+"F4.wireOp",EDGE,"E1202.MirrorCS"),sQuery(id+"F4.wireOp",EDGE,"E1204.MirrorCS"),sQuery(id+"F4.wireOp",EDGE,"E1205.MirrorCS"),sQuery(id+"F4.wireOp",EDGE,"E1207.MirrorCS"),sQuery(id+"F4.wireOp",EDGE,"E1208.MirrorCS"),sQuery(id+"F4.wireOp",EDGE,"E1210"),sQuery(id+"F4.wireOp",EDGE,"E1211"),sQuery(id+"F4.wireOp",EDGE,"E1212"),sQuery(id+"F4.wireOp",EDGE,"E1214.MirrorCS"),sQuery(id+"F4.wireOp",EDGE,"E1215.MirrorCS"),sQuery(id+"F4.wireOp",EDGE,"E1216"),sQuery(id+"F4.wireOp",EDGE,"E1217"),sQuery(id+"F4.wireOp",EDGE,"E1219.MirrorCS"),sQuery(id+"F4.wireOp",EDGE,"E1220.MirrorCS"),sQuery(id+"F4.wireOp",EDGE,"E1227"),sQuery(id+"F4.wireOp",EDGE,"E1228"),sQuery(id+"F4.wireOp",EDGE,"E1229"),sQuery(id+"F4.wireOp",EDGE,"E1230"),sQuery(id+"F4.wireOp",EDGE,"E1232"),sQuery(id+"F4.wireOp",EDGE,"E1237"),sQuery(id+"F4.wireOp",EDGE,"E1238"),sQuery(id+"F4.wireOp",EDGE,"E1239.filletArc"),sQuery(id+"F4.wireOp",EDGE,"E1240.filletArc"),sQuery(id+"F4.wireOp",EDGE,"E1241.MirrorCS"),sQuery(id+"F4.wireOp",EDGE,"E1242.MirrorCS"),sQuery(id+"F4.wireOp",EDGE,"E1243.MirrorCS"),sQuery(id+"F4.wireOp",EDGE,"E1244.MirrorCS"),sQuery(id+"F4.wireOp",EDGE,"E1245.MirrorCS"),sQuery(id+"F4.wireOp",EDGE,"E1247.MirrorCS"),sQuery(id+"F4.wireOp",EDGE,"E1248.MirrorCS"),sQuery(id+"F4.wireOp",EDGE,"E1249.MirrorCS"),sQuery(id+"F4.wireOp",EDGE,"E1250.MirrorCS"),sQuery(id+"F4.wireOp",EDGE,"E1251.MirrorCS"),sQuery(id+"F4.wireOp",EDGE,"E1253.MirrorCS"),sQuery(id+"F4.wireOp",EDGE,"E1254.MirrorCS"),sQuery(id+"F4.wireOp",EDGE,"E1255.MirrorCS"),sQuery(id+"F4.wireOp",EDGE,"E1257.MirrorCS"),sQuery(id+"F4.wireOp",EDGE,"E1259.MirrorCS"),sQuery(id+"F4.wireOp",EDGE,"E1260.MirrorCS"),sQuery(id+"F4.wireOp",EDGE,"E1261.MirrorCS"),sQuery(id+"F4.wireOp",EDGE,"E1263.MirrorCS"),sQuery(id+"F4.wireOp",EDGE,"E1264.MirrorCS"),sQuery(id+"F4.wireOp",EDGE,"E1265.MirrorCS"),sQuery(id+"F4.wireOp",EDGE,"E1266.MirrorCS"),sQuery(id+"F4.wireOp",EDGE,"E1267.MirrorCS"),sQuery(id+"F4.wireOp",EDGE,"E1268.MirrorCS"),sQuery(id+"F4.wireOp",EDGE,"E1269.MirrorCS"),sQuery(id+"F4.wireOp",EDGE,"E1270.MirrorCS"),sQuery(id+"F4.wireOp",EDGE,"E1271.MirrorCS"),sQuery(id+"F4.wireOp",EDGE,"E1272.MirrorCS"),sQuery(id+"F4.wireOp",EDGE,"E1273.MirrorCS"),sQuery(id+"F4.wireOp",EDGE,"E1275.MirrorCS"),sQuery(id+"F4.wireOp",EDGE,"E1276.MirrorCS"),sQuery(id+"F4.wireOp",EDGE,"E1277.MirrorCS"),sQuery(id+"F4.wireOp",EDGE,"E1278.MirrorCS"),sQuery(id+"F4.wireOp",EDGE,"E1280.MirrorCS"),sQuery(id+"F4.wireOp",EDGE,"E1281.MirrorCS"),sQuery(id+"F4.wireOp",EDGE,"E1283.MirrorCS"),sQuery(id+"F4.wireOp",EDGE,"E1284.MirrorCS"),sQuery(id+"F4.wireOp",EDGE,"E1285.MirrorCS"),sQuery(id+"F4.wireOp",EDGE,"E1288.MirrorCS"),sQuery(id+"F4.wireOp",EDGE,"E1291.MirrorCS"),sQuery(id+"F4.wireOp",EDGE,"E1293.MirrorCS"),sQuery(id+"F4.wireOp",EDGE,"E1294.MirrorCS"),sQuery(id+"F4.wireOp",EDGE,"E1296.MirrorCS"),sQuery(id+"F4.wireOp",EDGE,"E1297.MirrorCS"),sQuery(id+"F4.wireOp",EDGE,"E1298"),sQuery(id+"F4.wireOp",EDGE,"E1299"),sQuery(id+"F4.wireOp",EDGE,"E1300"),sQuery(id+"F4.wireOp",EDGE,"E1302.MirrorCS"),sQuery(id+"F4.wireOp",EDGE,"E1303.MirrorCS"),sQuery(id+"F4.wireOp",EDGE,"E1304"),sQuery(id+"F4.wireOp",EDGE,"E1305"),sQuery(id+"F4.wireOp",EDGE,"E1307.MirrorCS"),sQuery(id+"F4.wireOp",EDGE,"E1308.MirrorCS"),sQuery(id+"F4.wireOp",EDGE,"E1315"),sQuery(id+"F4.wireOp",EDGE,"E1316"),sQuery(id+"F4.wireOp",EDGE,"E1317"),sQuery(id+"F4.wireOp",EDGE,"E1318"),sQuery(id+"F4.wireOp",EDGE,"E1319"),sQuery(id+"F4.wireOp",EDGE,"E1320"),sQuery(id+"F4.wireOp",EDGE,"E1321"),sQuery(id+"F4.wireOp",EDGE,"E1323"),sQuery(id+"F4.wireOp",EDGE,"E1324"),sQuery(id+"F4.wireOp",EDGE,"E1325"),sQuery(id+"F4.wireOp",EDGE,"E1326"),sQuery(id+"F4.wireOp",EDGE,"E1327"),sQuery(id+"F4.wireOp",EDGE,"E1328"),sQuery(id+"F4.wireOp",EDGE,"E1329"),sQuery(id+"F4.wireOp",EDGE,"E1330"),sQuery(id+"F4.wireOp",EDGE,"E1331"),sQuery(id+"F4.wireOp",EDGE,"E1332"),sQuery(id+"F4.wireOp",EDGE,"E1333"),sQuery(id+"F4.wireOp",EDGE,"E1334"),sQuery(id+"F4.wireOp",EDGE,"E1335"),sQuery(id+"F4.wireOp",EDGE,"E1336"),sQuery(id+"F4.wireOp",EDGE,"E1337"),sQuery(id+"F4.wireOp",EDGE,"E1338"),sQuery(id+"F4.wireOp",EDGE,"E1339"),sQuery(id+"F4.wireOp",EDGE,"E1340"),sQuery(id+"F4.wireOp",EDGE,"E1342.trimOffspring"),sQuery(id+"F4.wireOp",EDGE,"E1343"),sQuery(id+"F4.wireOp",EDGE,"E1344"),sQuery(id+"F4.wireOp",EDGE,"E1345"),sQuery(id+"F4.wireOp",EDGE,"E1346"),sQuery(id+"F4.wireOp",EDGE,"E1347"),sQuery(id+"F4.wireOp",EDGE,"E1348")])]});
            transform(context, id + "F13", {"entities" : qUnion([Q0]), "transformType" : TransformType.TRANSLATION_3D, "dx" : 164.6 * mm, "dy" : 0 * mm, "dz" : 0 * mm, "makeCopy" : true});
        }
        {
            var Q0;
            Q0=makeQuery(id+"F13.opPattern","COPY",FACE,{"derivedFrom":makeQuery(id+"F11.opExtrude","CAP_FACE",FACE,{"disambiguationData":[OSD([sQuery(id+"F4.wireOp",EDGE,"E857"),sQuery(id+"F4.wireOp",EDGE,"E858"),sQuery(id+"F4.wireOp",EDGE,"E859"),sQuery(id+"F4.wireOp",EDGE,"E860"),sQuery(id+"F4.wireOp",EDGE,"E861"),sQuery(id+"F4.wireOp",EDGE,"E862"),sQuery(id+"F4.wireOp",EDGE,"E863"),sQuery(id+"F4.wireOp",EDGE,"E864"),sQuery(id+"F4.wireOp",EDGE,"E865"),sQuery(id+"F4.wireOp",EDGE,"E868.filletArc"),sQuery(id+"F4.wireOp",EDGE,"E870"),sQuery(id+"F4.wireOp",EDGE,"E871"),sQuery(id+"F4.wireOp",EDGE,"E872"),sQuery(id+"F4.wireOp",EDGE,"E873.filletArc"),sQuery(id+"F4.wireOp",EDGE,"E874.filletArc"),sQuery(id+"F4.wireOp",EDGE,"E875.filletArc"),sQuery(id+"F4.wireOp",EDGE,"E876.filletArc"),sQuery(id+"F4.wireOp",EDGE,"E877.MirrorCS"),sQuery(id+"F4.wireOp",EDGE,"E878.MirrorCS"),sQuery(id+"F4.wireOp",EDGE,"E880.MirrorCS"),sQuery(id+"F4.wireOp",EDGE,"E882.MirrorCS"),sQuery(id+"F4.wireOp",EDGE,"E883.MirrorCS"),sQuery(id+"F4.wireOp",EDGE,"E884.MirrorCS"),sQuery(id+"F4.wireOp",EDGE,"E885.MirrorCS"),sQuery(id+"F4.wireOp",EDGE,"E888.MirrorCS"),sQuery(id+"F4.wireOp",EDGE,"E891.MirrorCS"),sQuery(id+"F4.wireOp",EDGE,"E892.MirrorCS"),sQuery(id+"F4.wireOp",EDGE,"E893.MirrorCS"),sQuery(id+"F4.wireOp",EDGE,"E895.MirrorCS"),sQuery(id+"F4.wireOp",EDGE,"E898.MirrorCS"),sQuery(id+"F4.wireOp",EDGE,"E899.MirrorCS"),sQuery(id+"F4.wireOp",EDGE,"E901.MirrorCS"),sQuery(id+"F4.wireOp",EDGE,"E902.MirrorCS"),sQuery(id+"F4.wireOp",EDGE,"E903.MirrorCS"),sQuery(id+"F4.wireOp",EDGE,"E904.MirrorCS"),sQuery(id+"F4.wireOp",EDGE,"E905.MirrorCS"),sQuery(id+"F4.wireOp",EDGE,"E906.MirrorCS"),sQuery(id+"F4.wireOp",EDGE,"E907.MirrorCS"),sQuery(id+"F4.wireOp",EDGE,"E912"),sQuery(id+"F4.wireOp",EDGE,"E913"),sQuery(id+"F4.wireOp",EDGE,"E914"),sQuery(id+"F4.wireOp",EDGE,"E916.MirrorCS"),sQuery(id+"F4.wireOp",EDGE,"E917.MirrorCS"),sQuery(id+"F4.wireOp",EDGE,"E918"),sQuery(id+"F4.wireOp",EDGE,"E919"),sQuery(id+"F4.wireOp",EDGE,"E921.MirrorCS"),sQuery(id+"F4.wireOp",EDGE,"E922.MirrorCS"),sQuery(id+"F4.wireOp",EDGE,"E925.MirrorCS"),sQuery(id+"F4.wireOp",EDGE,"E926.MirrorCS"),sQuery(id+"F4.wireOp",EDGE,"E927.MirrorCS"),sQuery(id+"F4.wireOp",EDGE,"E928.MirrorCS"),sQuery(id+"F4.wireOp",EDGE,"E929.MirrorCS"),sQuery(id+"F4.wireOp",EDGE,"E930.MirrorCS"),sQuery(id+"F4.wireOp",EDGE,"E931.MirrorCS"),sQuery(id+"F4.wireOp",EDGE,"E932.MirrorCS"),sQuery(id+"F4.wireOp",EDGE,"E933.MirrorCS"),sQuery(id+"F4.wireOp",EDGE,"E934.MirrorCS"),sQuery(id+"F4.wireOp",EDGE,"E935.MirrorCS"),sQuery(id+"F4.wireOp",EDGE,"E936.MirrorCS"),sQuery(id+"F4.wireOp",EDGE,"E937.MirrorCS"),sQuery(id+"F4.wireOp",EDGE,"E938.MirrorCS"),sQuery(id+"F4.wireOp",EDGE,"E939.MirrorCS"),sQuery(id+"F4.wireOp",EDGE,"E940.MirrorCS"),sQuery(id+"F4.wireOp",EDGE,"E941.MirrorCS"),sQuery(id+"F4.wireOp",EDGE,"E942.MirrorCS"),sQuery(id+"F4.wireOp",EDGE,"E943.MirrorCS"),sQuery(id+"F4.wireOp",EDGE,"E944.MirrorCS"),sQuery(id+"F4.wireOp",EDGE,"E945.MirrorCS"),sQuery(id+"F4.wireOp",EDGE,"E946.MirrorCS"),sQuery(id+"F4.wireOp",EDGE,"E947.MirrorCS"),sQuery(id+"F4.wireOp",EDGE,"E948.MirrorCS"),sQuery(id+"F4.wireOp",EDGE,"E949.MirrorCS"),sQuery(id+"F4.wireOp",EDGE,"E950.MirrorCS"),sQuery(id+"F4.wireOp",EDGE,"E951.MirrorCS"),sQuery(id+"F4.wireOp",EDGE,"E960.MirrorCS"),sQuery(id+"F4.wireOp",EDGE,"E961.MirrorCS"),sQuery(id+"F4.wireOp",EDGE,"E962.MirrorCS"),sQuery(id+"F4.wireOp",EDGE,"E964.MirrorCS"),sQuery(id+"F4.wireOp",EDGE,"E965.MirrorCS"),sQuery(id+"F4.wireOp",EDGE,"E966.MirrorCS"),sQuery(id+"F4.wireOp",EDGE,"E967.MirrorCS"),sQuery(id+"F4.wireOp",EDGE,"E970.MirrorCS"),sQuery(id+"F4.wireOp",EDGE,"E972.MirrorCS"),sQuery(id+"F4.wireOp",EDGE,"E973.MirrorCS"),sQuery(id+"F4.wireOp",EDGE,"E974.MirrorC"),sQuery(id+"F4.wireOp",EDGE,"E976.MirrorCS"),sQuery(id+"F4.wireOp",EDGE,"E978.MirrorCS"),sQuery(id+"F4.wireOp",EDGE,"E979.MirrorCS"),sQuery(id+"F4.wireOp",EDGE,"E980.MirrorCS"),sQuery(id+"F4.wireOp",EDGE,"E982.MirrorCS"),sQuery(id+"F4.wireOp",EDGE,"E983.MirrorCS"),sQuery(id+"F4.wireOp",EDGE,"E984.MirrorCS"),sQuery(id+"F4.wireOp",EDGE,"E987.MirrorCS"),sQuery(id+"F4.wireOp",EDGE,"E988.MirrorCS"),sQuery(id+"F4.wireOp",EDGE,"E990.MirrorCS"),sQuery(id+"F4.wireOp",EDGE,"E991.MirrorCS"),sQuery(id+"F4.wireOp",EDGE,"E992.MirrorCS"),sQuery(id+"F4.wireOp",EDGE,"E993.MirrorCS"),sQuery(id+"F4.wireOp",EDGE,"E994"),sQuery(id+"F4.wireOp",EDGE,"E995"),sQuery(id+"F4.wireOp",EDGE,"E996"),sQuery(id+"F4.wireOp",EDGE,"E997.MirrorCS"),sQuery(id+"F4.wireOp",EDGE,"E998.MirrorCS"),sQuery(id+"F4.wireOp",EDGE,"E999.MirrorCS"),sQuery(id+"F4.wireOp",EDGE,"E1000.MirrorCS"),sQuery(id+"F4.wireOp",EDGE,"E1001.MirrorCS"),sQuery(id+"F4.wireOp",EDGE,"E1002.MirrorCS"),sQuery(id+"F4.wireOp",EDGE,"E1003.MirrorCS"),sQuery(id+"F4.wireOp",EDGE,"E1004.MirrorCS"),sQuery(id+"F4.wireOp",EDGE,"E1005.MirrorCS"),sQuery(id+"F4.wireOp",EDGE,"E1006.MirrorCS"),sQuery(id+"F4.wireOp",EDGE,"E1007.MirrorCS"),sQuery(id+"F4.wireOp",EDGE,"E1008.MirrorCS"),sQuery(id+"F4.wireOp",EDGE,"E1009.MirrorCS"),sQuery(id+"F4.wireOp",EDGE,"E1010.MirrorCS"),sQuery(id+"F4.wireOp",EDGE,"E1011.MirrorCS"),sQuery(id+"F4.wireOp",EDGE,"E1012.MirrorCS"),sQuery(id+"F4.wireOp",EDGE,"E1013.MirrorCS"),sQuery(id+"F4.wireOp",EDGE,"E1014.MirrorCS"),sQuery(id+"F4.wireOp",EDGE,"E1015.MirrorCS"),sQuery(id+"F4.wireOp",EDGE,"E1016.MirrorCS"),sQuery(id+"F4.wireOp",EDGE,"E1017.MirrorCS"),sQuery(id+"F4.wireOp",EDGE,"E1018.MirrorCS"),sQuery(id+"F4.wireOp",EDGE,"E1019.MirrorCS"),sQuery(id+"F4.wireOp",EDGE,"E1020.MirrorCS"),sQuery(id+"F4.wireOp",EDGE,"E1021.MirrorCS"),sQuery(id+"F4.wireOp",EDGE,"E1022.MirrorCS"),sQuery(id+"F4.wireOp",EDGE,"E1023.MirrorCS"),sQuery(id+"F4.wireOp",EDGE,"E1024.MirrorCS"),sQuery(id+"F4.wireOp",EDGE,"E1025.MirrorCS"),sQuery(id+"F4.wireOp",EDGE,"E1026.MirrorCS"),sQuery(id+"F4.wireOp",EDGE,"E1027.MirrorCS"),sQuery(id+"F4.wireOp",EDGE,"E1028.MirrorCS"),sQuery(id+"F4.wireOp",EDGE,"E1029.MirrorCS"),sQuery(id+"F4.wireOp",EDGE,"E1030.MirrorCS"),sQuery(id+"F4.wireOp",EDGE,"E1031.MirrorCS"),sQuery(id+"F4.wireOp",EDGE,"E1032.MirrorCS"),sQuery(id+"F4.wireOp",EDGE,"E1033.MirrorCS"),sQuery(id+"F4.wireOp",EDGE,"E1034.MirrorCS"),sQuery(id+"F4.wireOp",EDGE,"E1035.MirrorCS"),sQuery(id+"F4.wireOp",EDGE,"E1036.MirrorCS"),sQuery(id+"F4.wireOp",EDGE,"E1037.MirrorCS"),sQuery(id+"F4.wireOp",EDGE,"E1038.MirrorCS"),sQuery(id+"F4.wireOp",EDGE,"E1039.MirrorCS"),sQuery(id+"F4.wireOp",EDGE,"E1040.MirrorCS"),sQuery(id+"F4.wireOp",EDGE,"E1041.MirrorCS"),sQuery(id+"F4.wireOp",EDGE,"E1042.MirrorCS"),sQuery(id+"F4.wireOp",EDGE,"E1043.MirrorCS"),sQuery(id+"F4.wireOp",EDGE,"E1044.MirrorCS"),sQuery(id+"F4.wireOp",EDGE,"E1045.MirrorCS"),sQuery(id+"F4.wireOp",EDGE,"E1046.MirrorCS"),sQuery(id+"F4.wireOp",EDGE,"E1047.MirrorCS"),sQuery(id+"F4.wireOp",EDGE,"E1048.MirrorCS"),sQuery(id+"F4.wireOp",EDGE,"E1049.MirrorCS"),sQuery(id+"F4.wireOp",EDGE,"E1050.MirrorCS"),sQuery(id+"F4.wireOp",EDGE,"E1051.MirrorCS"),sQuery(id+"F4.wireOp",EDGE,"E1052.MirrorCS"),sQuery(id+"F4.wireOp",EDGE,"E1053.MirrorCS"),sQuery(id+"F4.wireOp",EDGE,"E1054.MirrorCS"),sQuery(id+"F4.wireOp",EDGE,"E1055.MirrorCS"),sQuery(id+"F4.wireOp",EDGE,"E1056.MirrorCS"),sQuery(id+"F4.wireOp",EDGE,"E1057.MirrorCS"),sQuery(id+"F4.wireOp",EDGE,"E1058.MirrorCS"),sQuery(id+"F4.wireOp",EDGE,"E1059.MirrorCS"),sQuery(id+"F4.wireOp",EDGE,"E1060.MirrorCS"),sQuery(id+"F4.wireOp",EDGE,"E1061.MirrorCS"),sQuery(id+"F4.wireOp",EDGE,"E1062.MirrorCS"),sQuery(id+"F4.wireOp",EDGE,"E1063.MirrorCS"),sQuery(id+"F4.wireOp",EDGE,"E1064.MirrorCS"),sQuery(id+"F4.wireOp",EDGE,"E1065.MirrorCS"),sQuery(id+"F4.wireOp",EDGE,"E1066.MirrorCS"),sQuery(id+"F4.wireOp",EDGE,"E1067.MirrorCS"),sQuery(id+"F4.wireOp",EDGE,"E1068.MirrorCS"),sQuery(id+"F4.wireOp",EDGE,"E1069.MirrorCS"),sQuery(id+"F4.wireOp",EDGE,"E1070.MirrorCS"),sQuery(id+"F4.wireOp",EDGE,"E1071.MirrorCS"),sQuery(id+"F4.wireOp",EDGE,"E1072.MirrorCS"),sQuery(id+"F4.wireOp",EDGE,"E1073.MirrorCS"),sQuery(id+"F4.wireOp",EDGE,"E1074.MirrorCS"),sQuery(id+"F4.wireOp",EDGE,"E1075.MirrorCS"),sQuery(id+"F4.wireOp",EDGE,"E1081.MirrorCS"),sQuery(id+"F4.wireOp",EDGE,"E1084.MirrorCS"),sQuery(id+"F4.wireOp",EDGE,"E1089.MirrorCS"),sQuery(id+"F4.wireOp",EDGE,"E1090.MirrorCS"),sQuery(id+"F4.wireOp",EDGE,"E1096.MirrorCS"),sQuery(id+"F4.wireOp",EDGE,"E1097.MirrorCS"),sQuery(id+"F4.wireOp",EDGE,"E1098.MirrorCS"),sQuery(id+"F4.wireOp",EDGE,"E1099.MirrorCS"),sQuery(id+"F4.wireOp",EDGE,"E1100.MirrorCS"),sQuery(id+"F4.wireOp",EDGE,"E1101.MirrorCS"),sQuery(id+"F4.wireOp",EDGE,"E1102.MirrorC"),sQuery(id+"F4.wireOp",EDGE,"E1107.MirrorCS"),sQuery(id+"F4.wireOp",EDGE,"E1114.MirrorCS"),sQuery(id+"F4.wireOp",EDGE,"E1116.MirrorCS"),sQuery(id+"F4.wireOp",EDGE,"E1117.MirrorCS"),sQuery(id+"F4.wireOp",EDGE,"E1119.MirrorCS"),sQuery(id+"F4.wireOp",EDGE,"E1122.MirrorCS"),sQuery(id+"F4.wireOp",EDGE,"E1127.MirrorC"),sQuery(id+"F4.wireOp",EDGE,"E1129.MirrorCS"),sQuery(id+"F4.wireOp",EDGE,"E1131.MirrorCS"),sQuery(id+"F4.wireOp",EDGE,"E1132.MirrorCS"),sQuery(id+"F4.wireOp",EDGE,"E1133.MirrorCS"),sQuery(id+"F4.wireOp",EDGE,"E1135"),sQuery(id+"F4.wireOp",EDGE,"E1136"),sQuery(id+"F4.wireOp",EDGE,"E1137"),sQuery(id+"F4.wireOp",EDGE,"E1138"),sQuery(id+"F4.wireOp",EDGE,"E1139"),sQuery(id+"F4.wireOp",EDGE,"E1140"),sQuery(id+"F4.wireOp",EDGE,"E1141"),sQuery(id+"F4.wireOp",EDGE,"E1144"),sQuery(id+"F4.wireOp",EDGE,"E1148"),sQuery(id+"F4.wireOp",EDGE,"E1149"),sQuery(id+"F4.wireOp",EDGE,"E1150.filletArc"),sQuery(id+"F4.wireOp",EDGE,"E1151.filletArc"),sQuery(id+"F4.wireOp",EDGE,"E1152.MirrorCS"),sQuery(id+"F4.wireOp",EDGE,"E1153.MirrorCS"),sQuery(id+"F4.wireOp",EDGE,"E1154.MirrorCS"),sQuery(id+"F4.wireOp",EDGE,"E1155.MirrorCS"),sQuery(id+"F4.wireOp",EDGE,"E1156.MirrorCS"),sQuery(id+"F4.wireOp",EDGE,"E1158.MirrorCS"),sQuery(id+"F4.wireOp",EDGE,"E1159.MirrorCS"),sQuery(id+"F4.wireOp",EDGE,"E1160.MirrorCS"),sQuery(id+"F4.wireOp",EDGE,"E1161.MirrorCS"),sQuery(id+"F4.wireOp",EDGE,"E1162.MirrorCS"),sQuery(id+"F4.wireOp",EDGE,"E1164.MirrorCS"),sQuery(id+"F4.wireOp",EDGE,"E1165.MirrorCS"),sQuery(id+"F4.wireOp",EDGE,"E1166.MirrorCS"),sQuery(id+"F4.wireOp",EDGE,"E1168.MirrorCS"),sQuery(id+"F4.wireOp",EDGE,"E1170.MirrorCS"),sQuery(id+"F4.wireOp",EDGE,"E1171.MirrorCS"),sQuery(id+"F4.wireOp",EDGE,"E1172.MirrorCS"),sQuery(id+"F4.wireOp",EDGE,"E1174.MirrorCS"),sQuery(id+"F4.wireOp",EDGE,"E1175.MirrorCS"),sQuery(id+"F4.wireOp",EDGE,"E1176.MirrorCS"),sQuery(id+"F4.wireOp",EDGE,"E1177.MirrorCS"),sQuery(id+"F4.wireOp",EDGE,"E1178.MirrorCS"),sQuery(id+"F4.wireOp",EDGE,"E1179.MirrorCS"),sQuery(id+"F4.wireOp",EDGE,"E1180.MirrorCS"),sQuery(id+"F4.wireOp",EDGE,"E1181.MirrorCS"),sQuery(id+"F4.wireOp",EDGE,"E1182.MirrorCS"),sQuery(id+"F4.wireOp",EDGE,"E1183.MirrorCS"),sQuery(id+"F4.wireOp",EDGE,"E1184.MirrorCS"),sQuery(id+"F4.wireOp",EDGE,"E1186.MirrorCS"),sQuery(id+"F4.wireOp",EDGE,"E1187.MirrorCS"),sQuery(id+"F4.wireOp",EDGE,"E1188.MirrorCS"),sQuery(id+"F4.wireOp",EDGE,"E1189.MirrorCS"),sQuery(id+"F4.wireOp",EDGE,"E1191.MirrorCS"),sQuery(id+"F4.wireOp",EDGE,"E1192.MirrorCS"),sQuery(id+"F4.wireOp",EDGE,"E1194.MirrorCS"),sQuery(id+"F4.wireOp",EDGE,"E1195.MirrorCS"),sQuery(id+"F4.wireOp",EDGE,"E1196.MirrorCS"),sQuery(id+"F4.wireOp",EDGE,"E1199.MirrorCS"),sQuery(id+"F4.wireOp",EDGE,"E1202.MirrorCS"),sQuery(id+"F4.wireOp",EDGE,"E1204.MirrorCS"),sQuery(id+"F4.wireOp",EDGE,"E1205.MirrorCS"),sQuery(id+"F4.wireOp",EDGE,"E1207.MirrorCS"),sQuery(id+"F4.wireOp",EDGE,"E1208.MirrorCS"),sQuery(id+"F4.wireOp",EDGE,"E1210"),sQuery(id+"F4.wireOp",EDGE,"E1211"),sQuery(id+"F4.wireOp",EDGE,"E1212"),sQuery(id+"F4.wireOp",EDGE,"E1214.MirrorCS"),sQuery(id+"F4.wireOp",EDGE,"E1215.MirrorCS"),sQuery(id+"F4.wireOp",EDGE,"E1216"),sQuery(id+"F4.wireOp",EDGE,"E1217"),sQuery(id+"F4.wireOp",EDGE,"E1219.MirrorCS"),sQuery(id+"F4.wireOp",EDGE,"E1220.MirrorCS"),sQuery(id+"F4.wireOp",EDGE,"E1227"),sQuery(id+"F4.wireOp",EDGE,"E1228"),sQuery(id+"F4.wireOp",EDGE,"E1229"),sQuery(id+"F4.wireOp",EDGE,"E1230"),sQuery(id+"F4.wireOp",EDGE,"E1232"),sQuery(id+"F4.wireOp",EDGE,"E1237"),sQuery(id+"F4.wireOp",EDGE,"E1238"),sQuery(id+"F4.wireOp",EDGE,"E1239.filletArc"),sQuery(id+"F4.wireOp",EDGE,"E1240.filletArc"),sQuery(id+"F4.wireOp",EDGE,"E1241.MirrorCS"),sQuery(id+"F4.wireOp",EDGE,"E1242.MirrorCS"),sQuery(id+"F4.wireOp",EDGE,"E1243.MirrorCS"),sQuery(id+"F4.wireOp",EDGE,"E1244.MirrorCS"),sQuery(id+"F4.wireOp",EDGE,"E1245.MirrorCS"),sQuery(id+"F4.wireOp",EDGE,"E1247.MirrorCS"),sQuery(id+"F4.wireOp",EDGE,"E1248.MirrorCS"),sQuery(id+"F4.wireOp",EDGE,"E1249.MirrorCS"),sQuery(id+"F4.wireOp",EDGE,"E1250.MirrorCS"),sQuery(id+"F4.wireOp",EDGE,"E1251.MirrorCS"),sQuery(id+"F4.wireOp",EDGE,"E1253.MirrorCS"),sQuery(id+"F4.wireOp",EDGE,"E1254.MirrorCS"),sQuery(id+"F4.wireOp",EDGE,"E1255.MirrorCS"),sQuery(id+"F4.wireOp",EDGE,"E1257.MirrorCS"),sQuery(id+"F4.wireOp",EDGE,"E1259.MirrorCS"),sQuery(id+"F4.wireOp",EDGE,"E1260.MirrorCS"),sQuery(id+"F4.wireOp",EDGE,"E1261.MirrorCS"),sQuery(id+"F4.wireOp",EDGE,"E1263.MirrorCS"),sQuery(id+"F4.wireOp",EDGE,"E1264.MirrorCS"),sQuery(id+"F4.wireOp",EDGE,"E1265.MirrorCS"),sQuery(id+"F4.wireOp",EDGE,"E1266.MirrorCS"),sQuery(id+"F4.wireOp",EDGE,"E1267.MirrorCS"),sQuery(id+"F4.wireOp",EDGE,"E1268.MirrorCS"),sQuery(id+"F4.wireOp",EDGE,"E1269.MirrorCS"),sQuery(id+"F4.wireOp",EDGE,"E1270.MirrorCS"),sQuery(id+"F4.wireOp",EDGE,"E1271.MirrorCS"),sQuery(id+"F4.wireOp",EDGE,"E1272.MirrorCS"),sQuery(id+"F4.wireOp",EDGE,"E1273.MirrorCS"),sQuery(id+"F4.wireOp",EDGE,"E1275.MirrorCS"),sQuery(id+"F4.wireOp",EDGE,"E1276.MirrorCS"),sQuery(id+"F4.wireOp",EDGE,"E1277.MirrorCS"),sQuery(id+"F4.wireOp",EDGE,"E1278.MirrorCS"),sQuery(id+"F4.wireOp",EDGE,"E1280.MirrorCS"),sQuery(id+"F4.wireOp",EDGE,"E1281.MirrorCS"),sQuery(id+"F4.wireOp",EDGE,"E1283.MirrorCS"),sQuery(id+"F4.wireOp",EDGE,"E1284.MirrorCS"),sQuery(id+"F4.wireOp",EDGE,"E1285.MirrorCS"),sQuery(id+"F4.wireOp",EDGE,"E1288.MirrorCS"),sQuery(id+"F4.wireOp",EDGE,"E1291.MirrorCS"),sQuery(id+"F4.wireOp",EDGE,"E1293.MirrorCS"),sQuery(id+"F4.wireOp",EDGE,"E1294.MirrorCS"),sQuery(id+"F4.wireOp",EDGE,"E1296.MirrorCS"),sQuery(id+"F4.wireOp",EDGE,"E1297.MirrorCS"),sQuery(id+"F4.wireOp",EDGE,"E1298"),sQuery(id+"F4.wireOp",EDGE,"E1299"),sQuery(id+"F4.wireOp",EDGE,"E1300"),sQuery(id+"F4.wireOp",EDGE,"E1302.MirrorCS"),sQuery(id+"F4.wireOp",EDGE,"E1303.MirrorCS"),sQuery(id+"F4.wireOp",EDGE,"E1304"),sQuery(id+"F4.wireOp",EDGE,"E1305"),sQuery(id+"F4.wireOp",EDGE,"E1307.MirrorCS"),sQuery(id+"F4.wireOp",EDGE,"E1308.MirrorCS"),sQuery(id+"F4.wireOp",EDGE,"E1315"),sQuery(id+"F4.wireOp",EDGE,"E1316"),sQuery(id+"F4.wireOp",EDGE,"E1317"),sQuery(id+"F4.wireOp",EDGE,"E1318"),sQuery(id+"F4.wireOp",EDGE,"E1319"),sQuery(id+"F4.wireOp",EDGE,"E1320"),sQuery(id+"F4.wireOp",EDGE,"E1321"),sQuery(id+"F4.wireOp",EDGE,"E1323"),sQuery(id+"F4.wireOp",EDGE,"E1324"),sQuery(id+"F4.wireOp",EDGE,"E1325"),sQuery(id+"F4.wireOp",EDGE,"E1326"),sQuery(id+"F4.wireOp",EDGE,"E1327"),sQuery(id+"F4.wireOp",EDGE,"E1328"),sQuery(id+"F4.wireOp",EDGE,"E1329"),sQuery(id+"F4.wireOp",EDGE,"E1330"),sQuery(id+"F4.wireOp",EDGE,"E1331"),sQuery(id+"F4.wireOp",EDGE,"E1332"),sQuery(id+"F4.wireOp",EDGE,"E1333"),sQuery(id+"F4.wireOp",EDGE,"E1334"),sQuery(id+"F4.wireOp",EDGE,"E1335"),sQuery(id+"F4.wireOp",EDGE,"E1336"),sQuery(id+"F4.wireOp",EDGE,"E1337"),sQuery(id+"F4.wireOp",EDGE,"E1338"),sQuery(id+"F4.wireOp",EDGE,"E1339"),sQuery(id+"F4.wireOp",EDGE,"E1340"),sQuery(id+"F4.wireOp",EDGE,"E1342.trimOffspring"),sQuery(id+"F4.wireOp",EDGE,"E1343"),sQuery(id+"F4.wireOp",EDGE,"E1344"),sQuery(id+"F4.wireOp",EDGE,"E1345"),sQuery(id+"F4.wireOp",EDGE,"E1346"),sQuery(id+"F4.wireOp",EDGE,"E1347"),sQuery(id+"F4.wireOp",EDGE,"E1348")])],"isStart":true}),"instanceName":"1"});
            extrude(context, id + "F14", {"entities" : qUnion([Q0]), "operationType" : NewBodyOperationType.ADD, "depth" : 1004 * mm, "offsetDistance" : 25 * mm});
        }
        {
            var Q0;
            Q0=makeQuery(id+"F8.opExtrude","SWEPT_BODY",BODY,{"disambiguationData":[OSD([sQuery(id+"F3.wireOp",EDGE,"E534"),sQuery(id+"F3.wireOp",EDGE,"E535"),sQuery(id+"F3.wireOp",EDGE,"E536"),sQuery(id+"F3.wireOp",EDGE,"E537"),sQuery(id+"F3.wireOp",EDGE,"E538"),sQuery(id+"F3.wireOp",EDGE,"E539"),sQuery(id+"F3.wireOp",EDGE,"E540"),sQuery(id+"F3.wireOp",EDGE,"E541"),sQuery(id+"F3.wireOp",EDGE,"E542"),sQuery(id+"F3.wireOp",EDGE,"E545.filletArc"),sQuery(id+"F3.wireOp",EDGE,"E547"),sQuery(id+"F3.wireOp",EDGE,"E548"),sQuery(id+"F3.wireOp",EDGE,"E549"),sQuery(id+"F3.wireOp",EDGE,"E550.filletArc"),sQuery(id+"F3.wireOp",EDGE,"E551.filletArc"),sQuery(id+"F3.wireOp",EDGE,"E552.filletArc"),sQuery(id+"F3.wireOp",EDGE,"E553.filletArc"),sQuery(id+"F3.wireOp",EDGE,"E554.MirrorCS"),sQuery(id+"F3.wireOp",EDGE,"E555.MirrorCS"),sQuery(id+"F3.wireOp",EDGE,"E556.MirrorCS"),sQuery(id+"F3.wireOp",EDGE,"E557.MirrorCS"),sQuery(id+"F3.wireOp",EDGE,"E558.MirrorCS"),sQuery(id+"F3.wireOp",EDGE,"E561.MirrorCS"),sQuery(id+"F3.wireOp",EDGE,"E562.MirrorCS"),sQuery(id+"F3.wireOp",EDGE,"E563.MirrorCS"),sQuery(id+"F3.wireOp",EDGE,"E564.MirrorCS"),sQuery(id+"F3.wireOp",EDGE,"E565.MirrorCS"),sQuery(id+"F3.wireOp",EDGE,"E567.MirrorCS"),sQuery(id+"F3.wireOp",EDGE,"E568.MirrorCS"),sQuery(id+"F3.wireOp",EDGE,"E569.MirrorCS"),sQuery(id+"F3.wireOp",EDGE,"E571.MirrorCS"),sQuery(id+"F3.wireOp",EDGE,"E573.MirrorCS"),sQuery(id+"F3.wireOp",EDGE,"E574.MirrorCS"),sQuery(id+"F3.wireOp",EDGE,"E575.MirrorCS"),sQuery(id+"F3.wireOp",EDGE,"E577.MirrorCS"),sQuery(id+"F3.wireOp",EDGE,"E578.MirrorCS"),sQuery(id+"F3.wireOp",EDGE,"E579.MirrorCS"),sQuery(id+"F3.wireOp",EDGE,"E580.MirrorCS"),sQuery(id+"F3.wireOp",EDGE,"E581.MirrorCS"),sQuery(id+"F3.wireOp",EDGE,"E582.MirrorCS"),sQuery(id+"F3.wireOp",EDGE,"E583.MirrorCS"),sQuery(id+"F3.wireOp",EDGE,"E585.MirrorCS"),sQuery(id+"F3.wireOp",EDGE,"E586.MirrorCS"),sQuery(id+"F3.wireOp",EDGE,"E587.MirrorCS"),sQuery(id+"F3.wireOp",EDGE,"E589.MirrorCS"),sQuery(id+"F3.wireOp",EDGE,"E590.MirrorCS"),sQuery(id+"F3.wireOp",EDGE,"E591.MirrorCS"),sQuery(id+"F3.wireOp",EDGE,"E592.MirrorCS"),sQuery(id+"F3.wireOp",EDGE,"E593.MirrorCS"),sQuery(id+"F3.wireOp",EDGE,"E594.MirrorCS"),sQuery(id+"F3.wireOp",EDGE,"E595.MirrorCS"),sQuery(id+"F3.wireOp",EDGE,"E596.MirrorCS"),sQuery(id+"F3.wireOp",EDGE,"E599.MirrorCS"),sQuery(id+"F3.wireOp",EDGE,"E600.MirrorCS"),sQuery(id+"F3.wireOp",EDGE,"E601.MirrorCS"),sQuery(id+"F3.wireOp",EDGE,"E602.MirrorCS"),sQuery(id+"F3.wireOp",EDGE,"E607"),sQuery(id+"F3.wireOp",EDGE,"E608"),sQuery(id+"F3.wireOp",EDGE,"E609"),sQuery(id+"F3.wireOp",EDGE,"E611.MirrorCS"),sQuery(id+"F3.wireOp",EDGE,"E612.MirrorCS"),sQuery(id+"F3.wireOp",EDGE,"E613"),sQuery(id+"F3.wireOp",EDGE,"E614"),sQuery(id+"F3.wireOp",EDGE,"E616.MirrorCS"),sQuery(id+"F3.wireOp",EDGE,"E617.MirrorCS"),sQuery(id+"F3.wireOp",EDGE,"E620.MirrorCS"),sQuery(id+"F3.wireOp",EDGE,"E621.MirrorCS"),sQuery(id+"F3.wireOp",EDGE,"E622.MirrorCS"),sQuery(id+"F3.wireOp",EDGE,"E623.MirrorCS"),sQuery(id+"F3.wireOp",EDGE,"E624.MirrorCS"),sQuery(id+"F3.wireOp",EDGE,"E625.MirrorCS"),sQuery(id+"F3.wireOp",EDGE,"E626.MirrorCS"),sQuery(id+"F3.wireOp",EDGE,"E627.MirrorCS"),sQuery(id+"F3.wireOp",EDGE,"E628.MirrorCS"),sQuery(id+"F3.wireOp",EDGE,"E629.MirrorCS"),sQuery(id+"F3.wireOp",EDGE,"E630.MirrorCS"),sQuery(id+"F3.wireOp",EDGE,"E631.MirrorCS"),sQuery(id+"F3.wireOp",EDGE,"E632.MirrorCS"),sQuery(id+"F3.wireOp",EDGE,"E633.MirrorCS"),sQuery(id+"F3.wireOp",EDGE,"E634.MirrorCS"),sQuery(id+"F3.wireOp",EDGE,"E635.MirrorCS"),sQuery(id+"F3.wireOp",EDGE,"E636.MirrorCS"),sQuery(id+"F3.wireOp",EDGE,"E637.MirrorCS"),sQuery(id+"F3.wireOp",EDGE,"E638.MirrorCS"),sQuery(id+"F3.wireOp",EDGE,"E639.MirrorCS"),sQuery(id+"F3.wireOp",EDGE,"E640.MirrorCS"),sQuery(id+"F3.wireOp",EDGE,"E641.MirrorCS"),sQuery(id+"F3.wireOp",EDGE,"E642.MirrorCS"),sQuery(id+"F3.wireOp",EDGE,"E643.MirrorCS"),sQuery(id+"F3.wireOp",EDGE,"E644.MirrorCS"),sQuery(id+"F3.wireOp",EDGE,"E645.MirrorCS"),sQuery(id+"F3.wireOp",EDGE,"E646.MirrorCS"),sQuery(id+"F3.wireOp",EDGE,"E655.MirrorCS"),sQuery(id+"F3.wireOp",EDGE,"E656.MirrorCS"),sQuery(id+"F3.wireOp",EDGE,"E657.MirrorCS"),sQuery(id+"F3.wireOp",EDGE,"E659.MirrorCS"),sQuery(id+"F3.wireOp",EDGE,"E660.MirrorCS"),sQuery(id+"F3.wireOp",EDGE,"E661.MirrorCS"),sQuery(id+"F3.wireOp",EDGE,"E662.MirrorCS"),sQuery(id+"F3.wireOp",EDGE,"E665.MirrorCS"),sQuery(id+"F3.wireOp",EDGE,"E667.MirrorCS"),sQuery(id+"F3.wireOp",EDGE,"E668.MirrorCS"),sQuery(id+"F3.wireOp",EDGE,"E669.MirrorC"),sQuery(id+"F3.wireOp",EDGE,"E671.MirrorCS"),sQuery(id+"F3.wireOp",EDGE,"E673.MirrorCS"),sQuery(id+"F3.wireOp",EDGE,"E674.MirrorCS"),sQuery(id+"F3.wireOp",EDGE,"E675.MirrorCS"),sQuery(id+"F3.wireOp",EDGE,"E677.MirrorCS"),sQuery(id+"F3.wireOp",EDGE,"E678.MirrorCS"),sQuery(id+"F3.wireOp",EDGE,"E679.MirrorCS"),sQuery(id+"F3.wireOp",EDGE,"E680.MirrorCS"),sQuery(id+"F3.wireOp",EDGE,"E683.MirrorCS"),sQuery(id+"F3.wireOp",EDGE,"E684.MirrorCS"),sQuery(id+"F3.wireOp",EDGE,"E685.MirrorCS"),sQuery(id+"F3.wireOp",EDGE,"E686.MirrorCS"),sQuery(id+"F3.wireOp",EDGE,"E687.MirrorCS"),sQuery(id+"F3.wireOp",EDGE,"E688.MirrorCS"),sQuery(id+"F3.wireOp",EDGE,"E689.MirrorCS"),sQuery(id+"F3.wireOp",EDGE,"E690"),sQuery(id+"F3.wireOp",EDGE,"E691"),sQuery(id+"F3.wireOp",EDGE,"E692"),sQuery(id+"F3.wireOp",EDGE,"E693"),sQuery(id+"F3.wireOp",EDGE,"E694.MirrorCS"),sQuery(id+"F3.wireOp",EDGE,"E695.MirrorCS"),sQuery(id+"F3.wireOp",EDGE,"E696.MirrorCS"),sQuery(id+"F3.wireOp",EDGE,"E697.MirrorCS"),sQuery(id+"F3.wireOp",EDGE,"E698.MirrorCS"),sQuery(id+"F3.wireOp",EDGE,"E699.MirrorCS"),sQuery(id+"F3.wireOp",EDGE,"E700.MirrorCS"),sQuery(id+"F3.wireOp",EDGE,"E701.MirrorCS"),sQuery(id+"F3.wireOp",EDGE,"E702.MirrorCS"),sQuery(id+"F3.wireOp",EDGE,"E703.MirrorCS"),sQuery(id+"F3.wireOp",EDGE,"E704.MirrorCS"),sQuery(id+"F3.wireOp",EDGE,"E705.MirrorCS"),sQuery(id+"F3.wireOp",EDGE,"E706.MirrorCS"),sQuery(id+"F3.wireOp",EDGE,"E707.MirrorCS"),sQuery(id+"F3.wireOp",EDGE,"E708.MirrorCS"),sQuery(id+"F3.wireOp",EDGE,"E709.MirrorCS"),sQuery(id+"F3.wireOp",EDGE,"E710.MirrorCS"),sQuery(id+"F3.wireOp",EDGE,"E711.MirrorCS"),sQuery(id+"F3.wireOp",EDGE,"E712.MirrorCS"),sQuery(id+"F3.wireOp",EDGE,"E713.MirrorCS"),sQuery(id+"F3.wireOp",EDGE,"E714.MirrorCS"),sQuery(id+"F3.wireOp",EDGE,"E715.MirrorCS"),sQuery(id+"F3.wireOp",EDGE,"E716.MirrorCS"),sQuery(id+"F3.wireOp",EDGE,"E717.MirrorCS"),sQuery(id+"F3.wireOp",EDGE,"E718.MirrorCS"),sQuery(id+"F3.wireOp",EDGE,"E719.MirrorCS"),sQuery(id+"F3.wireOp",EDGE,"E720.MirrorCS"),sQuery(id+"F3.wireOp",EDGE,"E721.MirrorCS"),sQuery(id+"F3.wireOp",EDGE,"E722.MirrorCS"),sQuery(id+"F3.wireOp",EDGE,"E723.MirrorCS"),sQuery(id+"F3.wireOp",EDGE,"E724.MirrorCS"),sQuery(id+"F3.wireOp",EDGE,"E725.MirrorCS"),sQuery(id+"F3.wireOp",EDGE,"E726.MirrorCS"),sQuery(id+"F3.wireOp",EDGE,"E727.MirrorCS"),sQuery(id+"F3.wireOp",EDGE,"E728.MirrorCS"),sQuery(id+"F3.wireOp",EDGE,"E729.MirrorCS"),sQuery(id+"F3.wireOp",EDGE,"E730.MirrorCS"),sQuery(id+"F3.wireOp",EDGE,"E731.MirrorCS"),sQuery(id+"F3.wireOp",EDGE,"E732.MirrorCS"),sQuery(id+"F3.wireOp",EDGE,"E733.MirrorCS"),sQuery(id+"F3.wireOp",EDGE,"E734.MirrorCS"),sQuery(id+"F3.wireOp",EDGE,"E735.MirrorCS"),sQuery(id+"F3.wireOp",EDGE,"E736.MirrorCS"),sQuery(id+"F3.wireOp",EDGE,"E737.MirrorCS"),sQuery(id+"F3.wireOp",EDGE,"E738.MirrorCS"),sQuery(id+"F3.wireOp",EDGE,"E739.MirrorCS"),sQuery(id+"F3.wireOp",EDGE,"E740.MirrorCS"),sQuery(id+"F3.wireOp",EDGE,"E741.MirrorCS"),sQuery(id+"F3.wireOp",EDGE,"E742.MirrorCS"),sQuery(id+"F3.wireOp",EDGE,"E743.MirrorCS"),sQuery(id+"F3.wireOp",EDGE,"E744.MirrorCS"),sQuery(id+"F3.wireOp",EDGE,"E745.MirrorCS"),sQuery(id+"F3.wireOp",EDGE,"E746.MirrorCS"),sQuery(id+"F3.wireOp",EDGE,"E747.MirrorCS"),sQuery(id+"F3.wireOp",EDGE,"E748.MirrorCS"),sQuery(id+"F3.wireOp",EDGE,"E749.MirrorCS"),sQuery(id+"F3.wireOp",EDGE,"E750.MirrorCS"),sQuery(id+"F3.wireOp",EDGE,"E751.MirrorCS"),sQuery(id+"F3.wireOp",EDGE,"E752.MirrorCS"),sQuery(id+"F3.wireOp",EDGE,"E753.MirrorCS"),sQuery(id+"F3.wireOp",EDGE,"E754.MirrorCS"),sQuery(id+"F3.wireOp",EDGE,"E755.MirrorCS"),sQuery(id+"F3.wireOp",EDGE,"E756.MirrorCS"),sQuery(id+"F3.wireOp",EDGE,"E757.MirrorCS"),sQuery(id+"F3.wireOp",EDGE,"E758.MirrorCS"),sQuery(id+"F3.wireOp",EDGE,"E759.MirrorCS"),sQuery(id+"F3.wireOp",EDGE,"E760.MirrorCS"),sQuery(id+"F3.wireOp",EDGE,"E761.MirrorCS"),sQuery(id+"F3.wireOp",EDGE,"E762.MirrorCS"),sQuery(id+"F3.wireOp",EDGE,"E763.MirrorCS"),sQuery(id+"F3.wireOp",EDGE,"E764.MirrorCS"),sQuery(id+"F3.wireOp",EDGE,"E765.MirrorCS"),sQuery(id+"F3.wireOp",EDGE,"E766.MirrorCS"),sQuery(id+"F3.wireOp",EDGE,"E767.MirrorCS"),sQuery(id+"F3.wireOp",EDGE,"E768.MirrorCS"),sQuery(id+"F3.wireOp",EDGE,"E769.MirrorCS"),sQuery(id+"F3.wireOp",EDGE,"E770.MirrorCS"),sQuery(id+"F3.wireOp",EDGE,"E771.MirrorCS"),sQuery(id+"F3.wireOp",EDGE,"E772.MirrorCS"),sQuery(id+"F3.wireOp",EDGE,"E773.MirrorCS"),sQuery(id+"F3.wireOp",EDGE,"E774.MirrorCS"),sQuery(id+"F3.wireOp",EDGE,"E775.MirrorCS"),sQuery(id+"F3.wireOp",EDGE,"E776.MirrorCS"),sQuery(id+"F3.wireOp",EDGE,"E777.MirrorCS"),sQuery(id+"F3.wireOp",EDGE,"E778.MirrorCS"),sQuery(id+"F3.wireOp",EDGE,"E779.MirrorCS"),sQuery(id+"F3.wireOp",EDGE,"E780.MirrorCS"),sQuery(id+"F3.wireOp",EDGE,"E781.MirrorCS"),sQuery(id+"F3.wireOp",EDGE,"E782.MirrorCS"),sQuery(id+"F3.wireOp",EDGE,"E783.MirrorCS"),sQuery(id+"F3.wireOp",EDGE,"E784.MirrorCS"),sQuery(id+"F3.wireOp",EDGE,"E785.MirrorCS"),sQuery(id+"F3.wireOp",EDGE,"E786.MirrorCS"),sQuery(id+"F3.wireOp",EDGE,"E792.MirrorCS"),sQuery(id+"F3.wireOp",EDGE,"E795.MirrorCS"),sQuery(id+"F3.wireOp",EDGE,"E800.MirrorCS"),sQuery(id+"F3.wireOp",EDGE,"E801.MirrorCS"),sQuery(id+"F3.wireOp",EDGE,"E802.MirrorCS"),sQuery(id+"F3.wireOp",EDGE,"E803.MirrorCS"),sQuery(id+"F3.wireOp",EDGE,"E808.MirrorCS"),sQuery(id+"F3.wireOp",EDGE,"E809.MirrorCS"),sQuery(id+"F3.wireOp",EDGE,"E811.MirrorCS"),sQuery(id+"F3.wireOp",EDGE,"E812.MirrorCS"),sQuery(id+"F3.wireOp",EDGE,"E813.MirrorCS"),sQuery(id+"F3.wireOp",EDGE,"E814.MirrorCS"),sQuery(id+"F3.wireOp",EDGE,"E815.MirrorC"),sQuery(id+"F3.wireOp",EDGE,"E816.MirrorCS"),sQuery(id+"F3.wireOp",EDGE,"E820.MirrorCS"),sQuery(id+"F3.wireOp",EDGE,"E824.MirrorCS"),sQuery(id+"F3.wireOp",EDGE,"E825.MirrorCS"),sQuery(id+"F3.wireOp",EDGE,"E830.MirrorCS"),sQuery(id+"F3.wireOp",EDGE,"E832.MirrorCS"),sQuery(id+"F3.wireOp",EDGE,"E833.MirrorCS"),sQuery(id+"F3.wireOp",EDGE,"E834.MirrorCS"),sQuery(id+"F3.wireOp",EDGE,"E835.MirrorCS"),sQuery(id+"F3.wireOp",EDGE,"E836.MirrorCS"),sQuery(id+"F3.wireOp",EDGE,"E839.MirrorCS"),sQuery(id+"F3.wireOp",EDGE,"E845.MirrorC"),sQuery(id+"F3.wireOp",EDGE,"E847.MirrorCS"),sQuery(id+"F3.wireOp",EDGE,"E849.MirrorCS"),sQuery(id+"F3.wireOp",EDGE,"E850.MirrorCS"),sQuery(id+"F3.wireOp",EDGE,"E851.MirrorCS"),sQuery(id+"F3.wireOp",EDGE,"E853"),sQuery(id+"F3.wireOp",EDGE,"E854"),sQuery(id+"F3.wireOp",EDGE,"E855"),sQuery(id+"F3.wireOp",EDGE,"E856")])]});
            transform(context, id + "F15", {"entities" : qUnion([Q0]), "transformType" : TransformType.TRANSLATION_3D, "dx" : 0 * mm, "dy" : 0 * mm, "dz" : -113.5 * mm, "makeCopy" : true});
        }
        {
            var Q0;
            Q0=makeQuery(id+"F15.opPattern","COPY",FACE,{"derivedFrom":makeQuery(id+"F8.opExtrude","CAP_FACE",FACE,{"disambiguationData":[OSD([sQuery(id+"F3.wireOp",EDGE,"E534"),sQuery(id+"F3.wireOp",EDGE,"E535"),sQuery(id+"F3.wireOp",EDGE,"E536"),sQuery(id+"F3.wireOp",EDGE,"E537"),sQuery(id+"F3.wireOp",EDGE,"E538"),sQuery(id+"F3.wireOp",EDGE,"E539"),sQuery(id+"F3.wireOp",EDGE,"E540"),sQuery(id+"F3.wireOp",EDGE,"E541"),sQuery(id+"F3.wireOp",EDGE,"E542"),sQuery(id+"F3.wireOp",EDGE,"E545.filletArc"),sQuery(id+"F3.wireOp",EDGE,"E547"),sQuery(id+"F3.wireOp",EDGE,"E548"),sQuery(id+"F3.wireOp",EDGE,"E549"),sQuery(id+"F3.wireOp",EDGE,"E550.filletArc"),sQuery(id+"F3.wireOp",EDGE,"E551.filletArc"),sQuery(id+"F3.wireOp",EDGE,"E552.filletArc"),sQuery(id+"F3.wireOp",EDGE,"E553.filletArc"),sQuery(id+"F3.wireOp",EDGE,"E554.MirrorCS"),sQuery(id+"F3.wireOp",EDGE,"E555.MirrorCS"),sQuery(id+"F3.wireOp",EDGE,"E556.MirrorCS"),sQuery(id+"F3.wireOp",EDGE,"E557.MirrorCS"),sQuery(id+"F3.wireOp",EDGE,"E558.MirrorCS"),sQuery(id+"F3.wireOp",EDGE,"E561.MirrorCS"),sQuery(id+"F3.wireOp",EDGE,"E562.MirrorCS"),sQuery(id+"F3.wireOp",EDGE,"E563.MirrorCS"),sQuery(id+"F3.wireOp",EDGE,"E564.MirrorCS"),sQuery(id+"F3.wireOp",EDGE,"E565.MirrorCS"),sQuery(id+"F3.wireOp",EDGE,"E567.MirrorCS"),sQuery(id+"F3.wireOp",EDGE,"E568.MirrorCS"),sQuery(id+"F3.wireOp",EDGE,"E569.MirrorCS"),sQuery(id+"F3.wireOp",EDGE,"E571.MirrorCS"),sQuery(id+"F3.wireOp",EDGE,"E573.MirrorCS"),sQuery(id+"F3.wireOp",EDGE,"E574.MirrorCS"),sQuery(id+"F3.wireOp",EDGE,"E575.MirrorCS"),sQuery(id+"F3.wireOp",EDGE,"E577.MirrorCS"),sQuery(id+"F3.wireOp",EDGE,"E578.MirrorCS"),sQuery(id+"F3.wireOp",EDGE,"E579.MirrorCS"),sQuery(id+"F3.wireOp",EDGE,"E580.MirrorCS"),sQuery(id+"F3.wireOp",EDGE,"E581.MirrorCS"),sQuery(id+"F3.wireOp",EDGE,"E582.MirrorCS"),sQuery(id+"F3.wireOp",EDGE,"E583.MirrorCS"),sQuery(id+"F3.wireOp",EDGE,"E585.MirrorCS"),sQuery(id+"F3.wireOp",EDGE,"E586.MirrorCS"),sQuery(id+"F3.wireOp",EDGE,"E587.MirrorCS"),sQuery(id+"F3.wireOp",EDGE,"E589.MirrorCS"),sQuery(id+"F3.wireOp",EDGE,"E590.MirrorCS"),sQuery(id+"F3.wireOp",EDGE,"E591.MirrorCS"),sQuery(id+"F3.wireOp",EDGE,"E592.MirrorCS"),sQuery(id+"F3.wireOp",EDGE,"E593.MirrorCS"),sQuery(id+"F3.wireOp",EDGE,"E594.MirrorCS"),sQuery(id+"F3.wireOp",EDGE,"E595.MirrorCS"),sQuery(id+"F3.wireOp",EDGE,"E596.MirrorCS"),sQuery(id+"F3.wireOp",EDGE,"E599.MirrorCS"),sQuery(id+"F3.wireOp",EDGE,"E600.MirrorCS"),sQuery(id+"F3.wireOp",EDGE,"E601.MirrorCS"),sQuery(id+"F3.wireOp",EDGE,"E602.MirrorCS"),sQuery(id+"F3.wireOp",EDGE,"E607"),sQuery(id+"F3.wireOp",EDGE,"E608"),sQuery(id+"F3.wireOp",EDGE,"E609"),sQuery(id+"F3.wireOp",EDGE,"E611.MirrorCS"),sQuery(id+"F3.wireOp",EDGE,"E612.MirrorCS"),sQuery(id+"F3.wireOp",EDGE,"E613"),sQuery(id+"F3.wireOp",EDGE,"E614"),sQuery(id+"F3.wireOp",EDGE,"E616.MirrorCS"),sQuery(id+"F3.wireOp",EDGE,"E617.MirrorCS"),sQuery(id+"F3.wireOp",EDGE,"E620.MirrorCS"),sQuery(id+"F3.wireOp",EDGE,"E621.MirrorCS"),sQuery(id+"F3.wireOp",EDGE,"E622.MirrorCS"),sQuery(id+"F3.wireOp",EDGE,"E623.MirrorCS"),sQuery(id+"F3.wireOp",EDGE,"E624.MirrorCS"),sQuery(id+"F3.wireOp",EDGE,"E625.MirrorCS"),sQuery(id+"F3.wireOp",EDGE,"E626.MirrorCS"),sQuery(id+"F3.wireOp",EDGE,"E627.MirrorCS"),sQuery(id+"F3.wireOp",EDGE,"E628.MirrorCS"),sQuery(id+"F3.wireOp",EDGE,"E629.MirrorCS"),sQuery(id+"F3.wireOp",EDGE,"E630.MirrorCS"),sQuery(id+"F3.wireOp",EDGE,"E631.MirrorCS"),sQuery(id+"F3.wireOp",EDGE,"E632.MirrorCS"),sQuery(id+"F3.wireOp",EDGE,"E633.MirrorCS"),sQuery(id+"F3.wireOp",EDGE,"E634.MirrorCS"),sQuery(id+"F3.wireOp",EDGE,"E635.MirrorCS"),sQuery(id+"F3.wireOp",EDGE,"E636.MirrorCS"),sQuery(id+"F3.wireOp",EDGE,"E637.MirrorCS"),sQuery(id+"F3.wireOp",EDGE,"E638.MirrorCS"),sQuery(id+"F3.wireOp",EDGE,"E639.MirrorCS"),sQuery(id+"F3.wireOp",EDGE,"E640.MirrorCS"),sQuery(id+"F3.wireOp",EDGE,"E641.MirrorCS"),sQuery(id+"F3.wireOp",EDGE,"E642.MirrorCS"),sQuery(id+"F3.wireOp",EDGE,"E643.MirrorCS"),sQuery(id+"F3.wireOp",EDGE,"E644.MirrorCS"),sQuery(id+"F3.wireOp",EDGE,"E645.MirrorCS"),sQuery(id+"F3.wireOp",EDGE,"E646.MirrorCS"),sQuery(id+"F3.wireOp",EDGE,"E655.MirrorCS"),sQuery(id+"F3.wireOp",EDGE,"E656.MirrorCS"),sQuery(id+"F3.wireOp",EDGE,"E657.MirrorCS"),sQuery(id+"F3.wireOp",EDGE,"E659.MirrorCS"),sQuery(id+"F3.wireOp",EDGE,"E660.MirrorCS"),sQuery(id+"F3.wireOp",EDGE,"E661.MirrorCS"),sQuery(id+"F3.wireOp",EDGE,"E662.MirrorCS"),sQuery(id+"F3.wireOp",EDGE,"E665.MirrorCS"),sQuery(id+"F3.wireOp",EDGE,"E667.MirrorCS"),sQuery(id+"F3.wireOp",EDGE,"E668.MirrorCS"),sQuery(id+"F3.wireOp",EDGE,"E669.MirrorC"),sQuery(id+"F3.wireOp",EDGE,"E671.MirrorCS"),sQuery(id+"F3.wireOp",EDGE,"E673.MirrorCS"),sQuery(id+"F3.wireOp",EDGE,"E674.MirrorCS"),sQuery(id+"F3.wireOp",EDGE,"E675.MirrorCS"),sQuery(id+"F3.wireOp",EDGE,"E677.MirrorCS"),sQuery(id+"F3.wireOp",EDGE,"E678.MirrorCS"),sQuery(id+"F3.wireOp",EDGE,"E679.MirrorCS"),sQuery(id+"F3.wireOp",EDGE,"E680.MirrorCS"),sQuery(id+"F3.wireOp",EDGE,"E683.MirrorCS"),sQuery(id+"F3.wireOp",EDGE,"E684.MirrorCS"),sQuery(id+"F3.wireOp",EDGE,"E685.MirrorCS"),sQuery(id+"F3.wireOp",EDGE,"E686.MirrorCS"),sQuery(id+"F3.wireOp",EDGE,"E687.MirrorCS"),sQuery(id+"F3.wireOp",EDGE,"E688.MirrorCS"),sQuery(id+"F3.wireOp",EDGE,"E689.MirrorCS"),sQuery(id+"F3.wireOp",EDGE,"E690"),sQuery(id+"F3.wireOp",EDGE,"E691"),sQuery(id+"F3.wireOp",EDGE,"E692"),sQuery(id+"F3.wireOp",EDGE,"E693"),sQuery(id+"F3.wireOp",EDGE,"E694.MirrorCS"),sQuery(id+"F3.wireOp",EDGE,"E695.MirrorCS"),sQuery(id+"F3.wireOp",EDGE,"E696.MirrorCS"),sQuery(id+"F3.wireOp",EDGE,"E697.MirrorCS"),sQuery(id+"F3.wireOp",EDGE,"E698.MirrorCS"),sQuery(id+"F3.wireOp",EDGE,"E699.MirrorCS"),sQuery(id+"F3.wireOp",EDGE,"E700.MirrorCS"),sQuery(id+"F3.wireOp",EDGE,"E701.MirrorCS"),sQuery(id+"F3.wireOp",EDGE,"E702.MirrorCS"),sQuery(id+"F3.wireOp",EDGE,"E703.MirrorCS"),sQuery(id+"F3.wireOp",EDGE,"E704.MirrorCS"),sQuery(id+"F3.wireOp",EDGE,"E705.MirrorCS"),sQuery(id+"F3.wireOp",EDGE,"E706.MirrorCS"),sQuery(id+"F3.wireOp",EDGE,"E707.MirrorCS"),sQuery(id+"F3.wireOp",EDGE,"E708.MirrorCS"),sQuery(id+"F3.wireOp",EDGE,"E709.MirrorCS"),sQuery(id+"F3.wireOp",EDGE,"E710.MirrorCS"),sQuery(id+"F3.wireOp",EDGE,"E711.MirrorCS"),sQuery(id+"F3.wireOp",EDGE,"E712.MirrorCS"),sQuery(id+"F3.wireOp",EDGE,"E713.MirrorCS"),sQuery(id+"F3.wireOp",EDGE,"E714.MirrorCS"),sQuery(id+"F3.wireOp",EDGE,"E715.MirrorCS"),sQuery(id+"F3.wireOp",EDGE,"E716.MirrorCS"),sQuery(id+"F3.wireOp",EDGE,"E717.MirrorCS"),sQuery(id+"F3.wireOp",EDGE,"E718.MirrorCS"),sQuery(id+"F3.wireOp",EDGE,"E719.MirrorCS"),sQuery(id+"F3.wireOp",EDGE,"E720.MirrorCS"),sQuery(id+"F3.wireOp",EDGE,"E721.MirrorCS"),sQuery(id+"F3.wireOp",EDGE,"E722.MirrorCS"),sQuery(id+"F3.wireOp",EDGE,"E723.MirrorCS"),sQuery(id+"F3.wireOp",EDGE,"E724.MirrorCS"),sQuery(id+"F3.wireOp",EDGE,"E725.MirrorCS"),sQuery(id+"F3.wireOp",EDGE,"E726.MirrorCS"),sQuery(id+"F3.wireOp",EDGE,"E727.MirrorCS"),sQuery(id+"F3.wireOp",EDGE,"E728.MirrorCS"),sQuery(id+"F3.wireOp",EDGE,"E729.MirrorCS"),sQuery(id+"F3.wireOp",EDGE,"E730.MirrorCS"),sQuery(id+"F3.wireOp",EDGE,"E731.MirrorCS"),sQuery(id+"F3.wireOp",EDGE,"E732.MirrorCS"),sQuery(id+"F3.wireOp",EDGE,"E733.MirrorCS"),sQuery(id+"F3.wireOp",EDGE,"E734.MirrorCS"),sQuery(id+"F3.wireOp",EDGE,"E735.MirrorCS"),sQuery(id+"F3.wireOp",EDGE,"E736.MirrorCS"),sQuery(id+"F3.wireOp",EDGE,"E737.MirrorCS"),sQuery(id+"F3.wireOp",EDGE,"E738.MirrorCS"),sQuery(id+"F3.wireOp",EDGE,"E739.MirrorCS"),sQuery(id+"F3.wireOp",EDGE,"E740.MirrorCS"),sQuery(id+"F3.wireOp",EDGE,"E741.MirrorCS"),sQuery(id+"F3.wireOp",EDGE,"E742.MirrorCS"),sQuery(id+"F3.wireOp",EDGE,"E743.MirrorCS"),sQuery(id+"F3.wireOp",EDGE,"E744.MirrorCS"),sQuery(id+"F3.wireOp",EDGE,"E745.MirrorCS"),sQuery(id+"F3.wireOp",EDGE,"E746.MirrorCS"),sQuery(id+"F3.wireOp",EDGE,"E747.MirrorCS"),sQuery(id+"F3.wireOp",EDGE,"E748.MirrorCS"),sQuery(id+"F3.wireOp",EDGE,"E749.MirrorCS"),sQuery(id+"F3.wireOp",EDGE,"E750.MirrorCS"),sQuery(id+"F3.wireOp",EDGE,"E751.MirrorCS"),sQuery(id+"F3.wireOp",EDGE,"E752.MirrorCS"),sQuery(id+"F3.wireOp",EDGE,"E753.MirrorCS"),sQuery(id+"F3.wireOp",EDGE,"E754.MirrorCS"),sQuery(id+"F3.wireOp",EDGE,"E755.MirrorCS"),sQuery(id+"F3.wireOp",EDGE,"E756.MirrorCS"),sQuery(id+"F3.wireOp",EDGE,"E757.MirrorCS"),sQuery(id+"F3.wireOp",EDGE,"E758.MirrorCS"),sQuery(id+"F3.wireOp",EDGE,"E759.MirrorCS"),sQuery(id+"F3.wireOp",EDGE,"E760.MirrorCS"),sQuery(id+"F3.wireOp",EDGE,"E761.MirrorCS"),sQuery(id+"F3.wireOp",EDGE,"E762.MirrorCS"),sQuery(id+"F3.wireOp",EDGE,"E763.MirrorCS"),sQuery(id+"F3.wireOp",EDGE,"E764.MirrorCS"),sQuery(id+"F3.wireOp",EDGE,"E765.MirrorCS"),sQuery(id+"F3.wireOp",EDGE,"E766.MirrorCS"),sQuery(id+"F3.wireOp",EDGE,"E767.MirrorCS"),sQuery(id+"F3.wireOp",EDGE,"E768.MirrorCS"),sQuery(id+"F3.wireOp",EDGE,"E769.MirrorCS"),sQuery(id+"F3.wireOp",EDGE,"E770.MirrorCS"),sQuery(id+"F3.wireOp",EDGE,"E771.MirrorCS"),sQuery(id+"F3.wireOp",EDGE,"E772.MirrorCS"),sQuery(id+"F3.wireOp",EDGE,"E773.MirrorCS"),sQuery(id+"F3.wireOp",EDGE,"E774.MirrorCS"),sQuery(id+"F3.wireOp",EDGE,"E775.MirrorCS"),sQuery(id+"F3.wireOp",EDGE,"E776.MirrorCS"),sQuery(id+"F3.wireOp",EDGE,"E777.MirrorCS"),sQuery(id+"F3.wireOp",EDGE,"E778.MirrorCS"),sQuery(id+"F3.wireOp",EDGE,"E779.MirrorCS"),sQuery(id+"F3.wireOp",EDGE,"E780.MirrorCS"),sQuery(id+"F3.wireOp",EDGE,"E781.MirrorCS"),sQuery(id+"F3.wireOp",EDGE,"E782.MirrorCS"),sQuery(id+"F3.wireOp",EDGE,"E783.MirrorCS"),sQuery(id+"F3.wireOp",EDGE,"E784.MirrorCS"),sQuery(id+"F3.wireOp",EDGE,"E785.MirrorCS"),sQuery(id+"F3.wireOp",EDGE,"E786.MirrorCS"),sQuery(id+"F3.wireOp",EDGE,"E792.MirrorCS"),sQuery(id+"F3.wireOp",EDGE,"E795.MirrorCS"),sQuery(id+"F3.wireOp",EDGE,"E800.MirrorCS"),sQuery(id+"F3.wireOp",EDGE,"E801.MirrorCS"),sQuery(id+"F3.wireOp",EDGE,"E802.MirrorCS"),sQuery(id+"F3.wireOp",EDGE,"E803.MirrorCS"),sQuery(id+"F3.wireOp",EDGE,"E808.MirrorCS"),sQuery(id+"F3.wireOp",EDGE,"E809.MirrorCS"),sQuery(id+"F3.wireOp",EDGE,"E811.MirrorCS"),sQuery(id+"F3.wireOp",EDGE,"E812.MirrorCS"),sQuery(id+"F3.wireOp",EDGE,"E813.MirrorCS"),sQuery(id+"F3.wireOp",EDGE,"E814.MirrorCS"),sQuery(id+"F3.wireOp",EDGE,"E815.MirrorC"),sQuery(id+"F3.wireOp",EDGE,"E816.MirrorCS"),sQuery(id+"F3.wireOp",EDGE,"E820.MirrorCS"),sQuery(id+"F3.wireOp",EDGE,"E824.MirrorCS"),sQuery(id+"F3.wireOp",EDGE,"E825.MirrorCS"),sQuery(id+"F3.wireOp",EDGE,"E830.MirrorCS"),sQuery(id+"F3.wireOp",EDGE,"E832.MirrorCS"),sQuery(id+"F3.wireOp",EDGE,"E833.MirrorCS"),sQuery(id+"F3.wireOp",EDGE,"E834.MirrorCS"),sQuery(id+"F3.wireOp",EDGE,"E835.MirrorCS"),sQuery(id+"F3.wireOp",EDGE,"E836.MirrorCS"),sQuery(id+"F3.wireOp",EDGE,"E839.MirrorCS"),sQuery(id+"F3.wireOp",EDGE,"E845.MirrorC"),sQuery(id+"F3.wireOp",EDGE,"E847.MirrorCS"),sQuery(id+"F3.wireOp",EDGE,"E849.MirrorCS"),sQuery(id+"F3.wireOp",EDGE,"E850.MirrorCS"),sQuery(id+"F3.wireOp",EDGE,"E851.MirrorCS"),sQuery(id+"F3.wireOp",EDGE,"E853"),sQuery(id+"F3.wireOp",EDGE,"E854"),sQuery(id+"F3.wireOp",EDGE,"E855"),sQuery(id+"F3.wireOp",EDGE,"E856")])],"isStart":true}),"instanceName":"1"});
            extrude(context, id + "F16", {"entities" : qUnion([Q0]), "operationType" : NewBodyOperationType.ADD, "depth" : (42.05 + 11.7) * mm, "offsetDistance" : 25 * mm});
        }
        {
            var Q0;
            Q0=makeQuery(id+"F15.opPattern","COPY",FACE,{"derivedFrom":makeQuery(id+"F8.opExtrude","CAP_FACE",FACE,{"disambiguationData":[OSD([sQuery(id+"F3.wireOp",EDGE,"E534"),sQuery(id+"F3.wireOp",EDGE,"E535"),sQuery(id+"F3.wireOp",EDGE,"E536"),sQuery(id+"F3.wireOp",EDGE,"E537"),sQuery(id+"F3.wireOp",EDGE,"E538"),sQuery(id+"F3.wireOp",EDGE,"E539"),sQuery(id+"F3.wireOp",EDGE,"E540"),sQuery(id+"F3.wireOp",EDGE,"E541"),sQuery(id+"F3.wireOp",EDGE,"E542"),sQuery(id+"F3.wireOp",EDGE,"E545.filletArc"),sQuery(id+"F3.wireOp",EDGE,"E547"),sQuery(id+"F3.wireOp",EDGE,"E548"),sQuery(id+"F3.wireOp",EDGE,"E549"),sQuery(id+"F3.wireOp",EDGE,"E550.filletArc"),sQuery(id+"F3.wireOp",EDGE,"E551.filletArc"),sQuery(id+"F3.wireOp",EDGE,"E552.filletArc"),sQuery(id+"F3.wireOp",EDGE,"E553.filletArc"),sQuery(id+"F3.wireOp",EDGE,"E554.MirrorCS"),sQuery(id+"F3.wireOp",EDGE,"E555.MirrorCS"),sQuery(id+"F3.wireOp",EDGE,"E556.MirrorCS"),sQuery(id+"F3.wireOp",EDGE,"E557.MirrorCS"),sQuery(id+"F3.wireOp",EDGE,"E558.MirrorCS"),sQuery(id+"F3.wireOp",EDGE,"E561.MirrorCS"),sQuery(id+"F3.wireOp",EDGE,"E562.MirrorCS"),sQuery(id+"F3.wireOp",EDGE,"E563.MirrorCS"),sQuery(id+"F3.wireOp",EDGE,"E564.MirrorCS"),sQuery(id+"F3.wireOp",EDGE,"E565.MirrorCS"),sQuery(id+"F3.wireOp",EDGE,"E567.MirrorCS"),sQuery(id+"F3.wireOp",EDGE,"E568.MirrorCS"),sQuery(id+"F3.wireOp",EDGE,"E569.MirrorCS"),sQuery(id+"F3.wireOp",EDGE,"E571.MirrorCS"),sQuery(id+"F3.wireOp",EDGE,"E573.MirrorCS"),sQuery(id+"F3.wireOp",EDGE,"E574.MirrorCS"),sQuery(id+"F3.wireOp",EDGE,"E575.MirrorCS"),sQuery(id+"F3.wireOp",EDGE,"E577.MirrorCS"),sQuery(id+"F3.wireOp",EDGE,"E578.MirrorCS"),sQuery(id+"F3.wireOp",EDGE,"E579.MirrorCS"),sQuery(id+"F3.wireOp",EDGE,"E580.MirrorCS"),sQuery(id+"F3.wireOp",EDGE,"E581.MirrorCS"),sQuery(id+"F3.wireOp",EDGE,"E582.MirrorCS"),sQuery(id+"F3.wireOp",EDGE,"E583.MirrorCS"),sQuery(id+"F3.wireOp",EDGE,"E585.MirrorCS"),sQuery(id+"F3.wireOp",EDGE,"E586.MirrorCS"),sQuery(id+"F3.wireOp",EDGE,"E587.MirrorCS"),sQuery(id+"F3.wireOp",EDGE,"E589.MirrorCS"),sQuery(id+"F3.wireOp",EDGE,"E590.MirrorCS"),sQuery(id+"F3.wireOp",EDGE,"E591.MirrorCS"),sQuery(id+"F3.wireOp",EDGE,"E592.MirrorCS"),sQuery(id+"F3.wireOp",EDGE,"E593.MirrorCS"),sQuery(id+"F3.wireOp",EDGE,"E594.MirrorCS"),sQuery(id+"F3.wireOp",EDGE,"E595.MirrorCS"),sQuery(id+"F3.wireOp",EDGE,"E596.MirrorCS"),sQuery(id+"F3.wireOp",EDGE,"E599.MirrorCS"),sQuery(id+"F3.wireOp",EDGE,"E600.MirrorCS"),sQuery(id+"F3.wireOp",EDGE,"E601.MirrorCS"),sQuery(id+"F3.wireOp",EDGE,"E602.MirrorCS"),sQuery(id+"F3.wireOp",EDGE,"E607"),sQuery(id+"F3.wireOp",EDGE,"E608"),sQuery(id+"F3.wireOp",EDGE,"E609"),sQuery(id+"F3.wireOp",EDGE,"E611.MirrorCS"),sQuery(id+"F3.wireOp",EDGE,"E612.MirrorCS"),sQuery(id+"F3.wireOp",EDGE,"E613"),sQuery(id+"F3.wireOp",EDGE,"E614"),sQuery(id+"F3.wireOp",EDGE,"E616.MirrorCS"),sQuery(id+"F3.wireOp",EDGE,"E617.MirrorCS"),sQuery(id+"F3.wireOp",EDGE,"E620.MirrorCS"),sQuery(id+"F3.wireOp",EDGE,"E621.MirrorCS"),sQuery(id+"F3.wireOp",EDGE,"E622.MirrorCS"),sQuery(id+"F3.wireOp",EDGE,"E623.MirrorCS"),sQuery(id+"F3.wireOp",EDGE,"E624.MirrorCS"),sQuery(id+"F3.wireOp",EDGE,"E625.MirrorCS"),sQuery(id+"F3.wireOp",EDGE,"E626.MirrorCS"),sQuery(id+"F3.wireOp",EDGE,"E627.MirrorCS"),sQuery(id+"F3.wireOp",EDGE,"E628.MirrorCS"),sQuery(id+"F3.wireOp",EDGE,"E629.MirrorCS"),sQuery(id+"F3.wireOp",EDGE,"E630.MirrorCS"),sQuery(id+"F3.wireOp",EDGE,"E631.MirrorCS"),sQuery(id+"F3.wireOp",EDGE,"E632.MirrorCS"),sQuery(id+"F3.wireOp",EDGE,"E633.MirrorCS"),sQuery(id+"F3.wireOp",EDGE,"E634.MirrorCS"),sQuery(id+"F3.wireOp",EDGE,"E635.MirrorCS"),sQuery(id+"F3.wireOp",EDGE,"E636.MirrorCS"),sQuery(id+"F3.wireOp",EDGE,"E637.MirrorCS"),sQuery(id+"F3.wireOp",EDGE,"E638.MirrorCS"),sQuery(id+"F3.wireOp",EDGE,"E639.MirrorCS"),sQuery(id+"F3.wireOp",EDGE,"E640.MirrorCS"),sQuery(id+"F3.wireOp",EDGE,"E641.MirrorCS"),sQuery(id+"F3.wireOp",EDGE,"E642.MirrorCS"),sQuery(id+"F3.wireOp",EDGE,"E643.MirrorCS"),sQuery(id+"F3.wireOp",EDGE,"E644.MirrorCS"),sQuery(id+"F3.wireOp",EDGE,"E645.MirrorCS"),sQuery(id+"F3.wireOp",EDGE,"E646.MirrorCS"),sQuery(id+"F3.wireOp",EDGE,"E655.MirrorCS"),sQuery(id+"F3.wireOp",EDGE,"E656.MirrorCS"),sQuery(id+"F3.wireOp",EDGE,"E657.MirrorCS"),sQuery(id+"F3.wireOp",EDGE,"E659.MirrorCS"),sQuery(id+"F3.wireOp",EDGE,"E660.MirrorCS"),sQuery(id+"F3.wireOp",EDGE,"E661.MirrorCS"),sQuery(id+"F3.wireOp",EDGE,"E662.MirrorCS"),sQuery(id+"F3.wireOp",EDGE,"E665.MirrorCS"),sQuery(id+"F3.wireOp",EDGE,"E667.MirrorCS"),sQuery(id+"F3.wireOp",EDGE,"E668.MirrorCS"),sQuery(id+"F3.wireOp",EDGE,"E669.MirrorC"),sQuery(id+"F3.wireOp",EDGE,"E671.MirrorCS"),sQuery(id+"F3.wireOp",EDGE,"E673.MirrorCS"),sQuery(id+"F3.wireOp",EDGE,"E674.MirrorCS"),sQuery(id+"F3.wireOp",EDGE,"E675.MirrorCS"),sQuery(id+"F3.wireOp",EDGE,"E677.MirrorCS"),sQuery(id+"F3.wireOp",EDGE,"E678.MirrorCS"),sQuery(id+"F3.wireOp",EDGE,"E679.MirrorCS"),sQuery(id+"F3.wireOp",EDGE,"E680.MirrorCS"),sQuery(id+"F3.wireOp",EDGE,"E683.MirrorCS"),sQuery(id+"F3.wireOp",EDGE,"E684.MirrorCS"),sQuery(id+"F3.wireOp",EDGE,"E685.MirrorCS"),sQuery(id+"F3.wireOp",EDGE,"E686.MirrorCS"),sQuery(id+"F3.wireOp",EDGE,"E687.MirrorCS"),sQuery(id+"F3.wireOp",EDGE,"E688.MirrorCS"),sQuery(id+"F3.wireOp",EDGE,"E689.MirrorCS"),sQuery(id+"F3.wireOp",EDGE,"E690"),sQuery(id+"F3.wireOp",EDGE,"E691"),sQuery(id+"F3.wireOp",EDGE,"E692"),sQuery(id+"F3.wireOp",EDGE,"E693"),sQuery(id+"F3.wireOp",EDGE,"E694.MirrorCS"),sQuery(id+"F3.wireOp",EDGE,"E695.MirrorCS"),sQuery(id+"F3.wireOp",EDGE,"E696.MirrorCS"),sQuery(id+"F3.wireOp",EDGE,"E697.MirrorCS"),sQuery(id+"F3.wireOp",EDGE,"E698.MirrorCS"),sQuery(id+"F3.wireOp",EDGE,"E699.MirrorCS"),sQuery(id+"F3.wireOp",EDGE,"E700.MirrorCS"),sQuery(id+"F3.wireOp",EDGE,"E701.MirrorCS"),sQuery(id+"F3.wireOp",EDGE,"E702.MirrorCS"),sQuery(id+"F3.wireOp",EDGE,"E703.MirrorCS"),sQuery(id+"F3.wireOp",EDGE,"E704.MirrorCS"),sQuery(id+"F3.wireOp",EDGE,"E705.MirrorCS"),sQuery(id+"F3.wireOp",EDGE,"E706.MirrorCS"),sQuery(id+"F3.wireOp",EDGE,"E707.MirrorCS"),sQuery(id+"F3.wireOp",EDGE,"E708.MirrorCS"),sQuery(id+"F3.wireOp",EDGE,"E709.MirrorCS"),sQuery(id+"F3.wireOp",EDGE,"E710.MirrorCS"),sQuery(id+"F3.wireOp",EDGE,"E711.MirrorCS"),sQuery(id+"F3.wireOp",EDGE,"E712.MirrorCS"),sQuery(id+"F3.wireOp",EDGE,"E713.MirrorCS"),sQuery(id+"F3.wireOp",EDGE,"E714.MirrorCS"),sQuery(id+"F3.wireOp",EDGE,"E715.MirrorCS"),sQuery(id+"F3.wireOp",EDGE,"E716.MirrorCS"),sQuery(id+"F3.wireOp",EDGE,"E717.MirrorCS"),sQuery(id+"F3.wireOp",EDGE,"E718.MirrorCS"),sQuery(id+"F3.wireOp",EDGE,"E719.MirrorCS"),sQuery(id+"F3.wireOp",EDGE,"E720.MirrorCS"),sQuery(id+"F3.wireOp",EDGE,"E721.MirrorCS"),sQuery(id+"F3.wireOp",EDGE,"E722.MirrorCS"),sQuery(id+"F3.wireOp",EDGE,"E723.MirrorCS"),sQuery(id+"F3.wireOp",EDGE,"E724.MirrorCS"),sQuery(id+"F3.wireOp",EDGE,"E725.MirrorCS"),sQuery(id+"F3.wireOp",EDGE,"E726.MirrorCS"),sQuery(id+"F3.wireOp",EDGE,"E727.MirrorCS"),sQuery(id+"F3.wireOp",EDGE,"E728.MirrorCS"),sQuery(id+"F3.wireOp",EDGE,"E729.MirrorCS"),sQuery(id+"F3.wireOp",EDGE,"E730.MirrorCS"),sQuery(id+"F3.wireOp",EDGE,"E731.MirrorCS"),sQuery(id+"F3.wireOp",EDGE,"E732.MirrorCS"),sQuery(id+"F3.wireOp",EDGE,"E733.MirrorCS"),sQuery(id+"F3.wireOp",EDGE,"E734.MirrorCS"),sQuery(id+"F3.wireOp",EDGE,"E735.MirrorCS"),sQuery(id+"F3.wireOp",EDGE,"E736.MirrorCS"),sQuery(id+"F3.wireOp",EDGE,"E737.MirrorCS"),sQuery(id+"F3.wireOp",EDGE,"E738.MirrorCS"),sQuery(id+"F3.wireOp",EDGE,"E739.MirrorCS"),sQuery(id+"F3.wireOp",EDGE,"E740.MirrorCS"),sQuery(id+"F3.wireOp",EDGE,"E741.MirrorCS"),sQuery(id+"F3.wireOp",EDGE,"E742.MirrorCS"),sQuery(id+"F3.wireOp",EDGE,"E743.MirrorCS"),sQuery(id+"F3.wireOp",EDGE,"E744.MirrorCS"),sQuery(id+"F3.wireOp",EDGE,"E745.MirrorCS"),sQuery(id+"F3.wireOp",EDGE,"E746.MirrorCS"),sQuery(id+"F3.wireOp",EDGE,"E747.MirrorCS"),sQuery(id+"F3.wireOp",EDGE,"E748.MirrorCS"),sQuery(id+"F3.wireOp",EDGE,"E749.MirrorCS"),sQuery(id+"F3.wireOp",EDGE,"E750.MirrorCS"),sQuery(id+"F3.wireOp",EDGE,"E751.MirrorCS"),sQuery(id+"F3.wireOp",EDGE,"E752.MirrorCS"),sQuery(id+"F3.wireOp",EDGE,"E753.MirrorCS"),sQuery(id+"F3.wireOp",EDGE,"E754.MirrorCS"),sQuery(id+"F3.wireOp",EDGE,"E755.MirrorCS"),sQuery(id+"F3.wireOp",EDGE,"E756.MirrorCS"),sQuery(id+"F3.wireOp",EDGE,"E757.MirrorCS"),sQuery(id+"F3.wireOp",EDGE,"E758.MirrorCS"),sQuery(id+"F3.wireOp",EDGE,"E759.MirrorCS"),sQuery(id+"F3.wireOp",EDGE,"E760.MirrorCS"),sQuery(id+"F3.wireOp",EDGE,"E761.MirrorCS"),sQuery(id+"F3.wireOp",EDGE,"E762.MirrorCS"),sQuery(id+"F3.wireOp",EDGE,"E763.MirrorCS"),sQuery(id+"F3.wireOp",EDGE,"E764.MirrorCS"),sQuery(id+"F3.wireOp",EDGE,"E765.MirrorCS"),sQuery(id+"F3.wireOp",EDGE,"E766.MirrorCS"),sQuery(id+"F3.wireOp",EDGE,"E767.MirrorCS"),sQuery(id+"F3.wireOp",EDGE,"E768.MirrorCS"),sQuery(id+"F3.wireOp",EDGE,"E769.MirrorCS"),sQuery(id+"F3.wireOp",EDGE,"E770.MirrorCS"),sQuery(id+"F3.wireOp",EDGE,"E771.MirrorCS"),sQuery(id+"F3.wireOp",EDGE,"E772.MirrorCS"),sQuery(id+"F3.wireOp",EDGE,"E773.MirrorCS"),sQuery(id+"F3.wireOp",EDGE,"E774.MirrorCS"),sQuery(id+"F3.wireOp",EDGE,"E775.MirrorCS"),sQuery(id+"F3.wireOp",EDGE,"E776.MirrorCS"),sQuery(id+"F3.wireOp",EDGE,"E777.MirrorCS"),sQuery(id+"F3.wireOp",EDGE,"E778.MirrorCS"),sQuery(id+"F3.wireOp",EDGE,"E779.MirrorCS"),sQuery(id+"F3.wireOp",EDGE,"E780.MirrorCS"),sQuery(id+"F3.wireOp",EDGE,"E781.MirrorCS"),sQuery(id+"F3.wireOp",EDGE,"E782.MirrorCS"),sQuery(id+"F3.wireOp",EDGE,"E783.MirrorCS"),sQuery(id+"F3.wireOp",EDGE,"E784.MirrorCS"),sQuery(id+"F3.wireOp",EDGE,"E785.MirrorCS"),sQuery(id+"F3.wireOp",EDGE,"E786.MirrorCS"),sQuery(id+"F3.wireOp",EDGE,"E792.MirrorCS"),sQuery(id+"F3.wireOp",EDGE,"E795.MirrorCS"),sQuery(id+"F3.wireOp",EDGE,"E800.MirrorCS"),sQuery(id+"F3.wireOp",EDGE,"E801.MirrorCS"),sQuery(id+"F3.wireOp",EDGE,"E802.MirrorCS"),sQuery(id+"F3.wireOp",EDGE,"E803.MirrorCS"),sQuery(id+"F3.wireOp",EDGE,"E808.MirrorCS"),sQuery(id+"F3.wireOp",EDGE,"E809.MirrorCS"),sQuery(id+"F3.wireOp",EDGE,"E811.MirrorCS"),sQuery(id+"F3.wireOp",EDGE,"E812.MirrorCS"),sQuery(id+"F3.wireOp",EDGE,"E813.MirrorCS"),sQuery(id+"F3.wireOp",EDGE,"E814.MirrorCS"),sQuery(id+"F3.wireOp",EDGE,"E815.MirrorC"),sQuery(id+"F3.wireOp",EDGE,"E816.MirrorCS"),sQuery(id+"F3.wireOp",EDGE,"E820.MirrorCS"),sQuery(id+"F3.wireOp",EDGE,"E824.MirrorCS"),sQuery(id+"F3.wireOp",EDGE,"E825.MirrorCS"),sQuery(id+"F3.wireOp",EDGE,"E830.MirrorCS"),sQuery(id+"F3.wireOp",EDGE,"E832.MirrorCS"),sQuery(id+"F3.wireOp",EDGE,"E833.MirrorCS"),sQuery(id+"F3.wireOp",EDGE,"E834.MirrorCS"),sQuery(id+"F3.wireOp",EDGE,"E835.MirrorCS"),sQuery(id+"F3.wireOp",EDGE,"E836.MirrorCS"),sQuery(id+"F3.wireOp",EDGE,"E839.MirrorCS"),sQuery(id+"F3.wireOp",EDGE,"E845.MirrorC"),sQuery(id+"F3.wireOp",EDGE,"E847.MirrorCS"),sQuery(id+"F3.wireOp",EDGE,"E849.MirrorCS"),sQuery(id+"F3.wireOp",EDGE,"E850.MirrorCS"),sQuery(id+"F3.wireOp",EDGE,"E851.MirrorCS"),sQuery(id+"F3.wireOp",EDGE,"E853"),sQuery(id+"F3.wireOp",EDGE,"E854"),sQuery(id+"F3.wireOp",EDGE,"E855"),sQuery(id+"F3.wireOp",EDGE,"E856")])],"isStart":false}),"instanceName":"1"});
            extrude(context, id + "F17", {"entities" : qUnion([Q0]), "operationType" : NewBodyOperationType.ADD, "depth" : 9.85 * mm, "offsetDistance" : 25 * mm});
        }
        {
            var Q0;
            Q0=makeQuery(id+"F16.opExtrude","CAP_FACE",FACE,{"disambiguationData":[OSD([sQuery(id+"F3.wireOp",EDGE,"E534"),sQuery(id+"F3.wireOp",EDGE,"E535"),sQuery(id+"F3.wireOp",EDGE,"E536"),sQuery(id+"F3.wireOp",EDGE,"E537"),sQuery(id+"F3.wireOp",EDGE,"E538"),sQuery(id+"F3.wireOp",EDGE,"E539"),sQuery(id+"F3.wireOp",EDGE,"E540"),sQuery(id+"F3.wireOp",EDGE,"E541"),sQuery(id+"F3.wireOp",EDGE,"E542"),sQuery(id+"F3.wireOp",EDGE,"E545.filletArc"),sQuery(id+"F3.wireOp",EDGE,"E547"),sQuery(id+"F3.wireOp",EDGE,"E548"),sQuery(id+"F3.wireOp",EDGE,"E549"),sQuery(id+"F3.wireOp",EDGE,"E550.filletArc"),sQuery(id+"F3.wireOp",EDGE,"E551.filletArc"),sQuery(id+"F3.wireOp",EDGE,"E552.filletArc"),sQuery(id+"F3.wireOp",EDGE,"E553.filletArc"),sQuery(id+"F3.wireOp",EDGE,"E554.MirrorCS"),sQuery(id+"F3.wireOp",EDGE,"E555.MirrorCS"),sQuery(id+"F3.wireOp",EDGE,"E556.MirrorCS"),sQuery(id+"F3.wireOp",EDGE,"E557.MirrorCS"),sQuery(id+"F3.wireOp",EDGE,"E558.MirrorCS"),sQuery(id+"F3.wireOp",EDGE,"E561.MirrorCS"),sQuery(id+"F3.wireOp",EDGE,"E562.MirrorCS"),sQuery(id+"F3.wireOp",EDGE,"E563.MirrorCS"),sQuery(id+"F3.wireOp",EDGE,"E564.MirrorCS"),sQuery(id+"F3.wireOp",EDGE,"E565.MirrorCS"),sQuery(id+"F3.wireOp",EDGE,"E567.MirrorCS"),sQuery(id+"F3.wireOp",EDGE,"E568.MirrorCS"),sQuery(id+"F3.wireOp",EDGE,"E569.MirrorCS"),sQuery(id+"F3.wireOp",EDGE,"E571.MirrorCS"),sQuery(id+"F3.wireOp",EDGE,"E573.MirrorCS"),sQuery(id+"F3.wireOp",EDGE,"E574.MirrorCS"),sQuery(id+"F3.wireOp",EDGE,"E575.MirrorCS"),sQuery(id+"F3.wireOp",EDGE,"E577.MirrorCS"),sQuery(id+"F3.wireOp",EDGE,"E578.MirrorCS"),sQuery(id+"F3.wireOp",EDGE,"E579.MirrorCS"),sQuery(id+"F3.wireOp",EDGE,"E580.MirrorCS"),sQuery(id+"F3.wireOp",EDGE,"E581.MirrorCS"),sQuery(id+"F3.wireOp",EDGE,"E582.MirrorCS"),sQuery(id+"F3.wireOp",EDGE,"E583.MirrorCS"),sQuery(id+"F3.wireOp",EDGE,"E585.MirrorCS"),sQuery(id+"F3.wireOp",EDGE,"E586.MirrorCS"),sQuery(id+"F3.wireOp",EDGE,"E587.MirrorCS"),sQuery(id+"F3.wireOp",EDGE,"E589.MirrorCS"),sQuery(id+"F3.wireOp",EDGE,"E590.MirrorCS"),sQuery(id+"F3.wireOp",EDGE,"E591.MirrorCS"),sQuery(id+"F3.wireOp",EDGE,"E592.MirrorCS"),sQuery(id+"F3.wireOp",EDGE,"E593.MirrorCS"),sQuery(id+"F3.wireOp",EDGE,"E594.MirrorCS"),sQuery(id+"F3.wireOp",EDGE,"E595.MirrorCS"),sQuery(id+"F3.wireOp",EDGE,"E596.MirrorCS"),sQuery(id+"F3.wireOp",EDGE,"E599.MirrorCS"),sQuery(id+"F3.wireOp",EDGE,"E600.MirrorCS"),sQuery(id+"F3.wireOp",EDGE,"E601.MirrorCS"),sQuery(id+"F3.wireOp",EDGE,"E602.MirrorCS"),sQuery(id+"F3.wireOp",EDGE,"E607"),sQuery(id+"F3.wireOp",EDGE,"E608"),sQuery(id+"F3.wireOp",EDGE,"E609"),sQuery(id+"F3.wireOp",EDGE,"E611.MirrorCS"),sQuery(id+"F3.wireOp",EDGE,"E612.MirrorCS"),sQuery(id+"F3.wireOp",EDGE,"E613"),sQuery(id+"F3.wireOp",EDGE,"E614"),sQuery(id+"F3.wireOp",EDGE,"E616.MirrorCS"),sQuery(id+"F3.wireOp",EDGE,"E617.MirrorCS"),sQuery(id+"F3.wireOp",EDGE,"E620.MirrorCS"),sQuery(id+"F3.wireOp",EDGE,"E621.MirrorCS"),sQuery(id+"F3.wireOp",EDGE,"E622.MirrorCS"),sQuery(id+"F3.wireOp",EDGE,"E623.MirrorCS"),sQuery(id+"F3.wireOp",EDGE,"E624.MirrorCS"),sQuery(id+"F3.wireOp",EDGE,"E625.MirrorCS"),sQuery(id+"F3.wireOp",EDGE,"E626.MirrorCS"),sQuery(id+"F3.wireOp",EDGE,"E627.MirrorCS"),sQuery(id+"F3.wireOp",EDGE,"E628.MirrorCS"),sQuery(id+"F3.wireOp",EDGE,"E629.MirrorCS"),sQuery(id+"F3.wireOp",EDGE,"E630.MirrorCS"),sQuery(id+"F3.wireOp",EDGE,"E631.MirrorCS"),sQuery(id+"F3.wireOp",EDGE,"E632.MirrorCS"),sQuery(id+"F3.wireOp",EDGE,"E633.MirrorCS"),sQuery(id+"F3.wireOp",EDGE,"E634.MirrorCS"),sQuery(id+"F3.wireOp",EDGE,"E635.MirrorCS"),sQuery(id+"F3.wireOp",EDGE,"E636.MirrorCS"),sQuery(id+"F3.wireOp",EDGE,"E637.MirrorCS"),sQuery(id+"F3.wireOp",EDGE,"E638.MirrorCS"),sQuery(id+"F3.wireOp",EDGE,"E639.MirrorCS"),sQuery(id+"F3.wireOp",EDGE,"E640.MirrorCS"),sQuery(id+"F3.wireOp",EDGE,"E641.MirrorCS"),sQuery(id+"F3.wireOp",EDGE,"E642.MirrorCS"),sQuery(id+"F3.wireOp",EDGE,"E643.MirrorCS"),sQuery(id+"F3.wireOp",EDGE,"E644.MirrorCS"),sQuery(id+"F3.wireOp",EDGE,"E645.MirrorCS"),sQuery(id+"F3.wireOp",EDGE,"E646.MirrorCS"),sQuery(id+"F3.wireOp",EDGE,"E655.MirrorCS"),sQuery(id+"F3.wireOp",EDGE,"E656.MirrorCS"),sQuery(id+"F3.wireOp",EDGE,"E657.MirrorCS"),sQuery(id+"F3.wireOp",EDGE,"E659.MirrorCS"),sQuery(id+"F3.wireOp",EDGE,"E660.MirrorCS"),sQuery(id+"F3.wireOp",EDGE,"E661.MirrorCS"),sQuery(id+"F3.wireOp",EDGE,"E662.MirrorCS"),sQuery(id+"F3.wireOp",EDGE,"E665.MirrorCS"),sQuery(id+"F3.wireOp",EDGE,"E667.MirrorCS"),sQuery(id+"F3.wireOp",EDGE,"E668.MirrorCS"),sQuery(id+"F3.wireOp",EDGE,"E669.MirrorC"),sQuery(id+"F3.wireOp",EDGE,"E671.MirrorCS"),sQuery(id+"F3.wireOp",EDGE,"E673.MirrorCS"),sQuery(id+"F3.wireOp",EDGE,"E674.MirrorCS"),sQuery(id+"F3.wireOp",EDGE,"E675.MirrorCS"),sQuery(id+"F3.wireOp",EDGE,"E677.MirrorCS"),sQuery(id+"F3.wireOp",EDGE,"E678.MirrorCS"),sQuery(id+"F3.wireOp",EDGE,"E679.MirrorCS"),sQuery(id+"F3.wireOp",EDGE,"E680.MirrorCS"),sQuery(id+"F3.wireOp",EDGE,"E683.MirrorCS"),sQuery(id+"F3.wireOp",EDGE,"E684.MirrorCS"),sQuery(id+"F3.wireOp",EDGE,"E685.MirrorCS"),sQuery(id+"F3.wireOp",EDGE,"E686.MirrorCS"),sQuery(id+"F3.wireOp",EDGE,"E687.MirrorCS"),sQuery(id+"F3.wireOp",EDGE,"E688.MirrorCS"),sQuery(id+"F3.wireOp",EDGE,"E689.MirrorCS"),sQuery(id+"F3.wireOp",EDGE,"E690"),sQuery(id+"F3.wireOp",EDGE,"E691"),sQuery(id+"F3.wireOp",EDGE,"E692"),sQuery(id+"F3.wireOp",EDGE,"E693"),sQuery(id+"F3.wireOp",EDGE,"E694.MirrorCS"),sQuery(id+"F3.wireOp",EDGE,"E695.MirrorCS"),sQuery(id+"F3.wireOp",EDGE,"E696.MirrorCS"),sQuery(id+"F3.wireOp",EDGE,"E697.MirrorCS"),sQuery(id+"F3.wireOp",EDGE,"E698.MirrorCS"),sQuery(id+"F3.wireOp",EDGE,"E699.MirrorCS"),sQuery(id+"F3.wireOp",EDGE,"E700.MirrorCS"),sQuery(id+"F3.wireOp",EDGE,"E701.MirrorCS"),sQuery(id+"F3.wireOp",EDGE,"E702.MirrorCS"),sQuery(id+"F3.wireOp",EDGE,"E703.MirrorCS"),sQuery(id+"F3.wireOp",EDGE,"E704.MirrorCS"),sQuery(id+"F3.wireOp",EDGE,"E705.MirrorCS"),sQuery(id+"F3.wireOp",EDGE,"E706.MirrorCS"),sQuery(id+"F3.wireOp",EDGE,"E707.MirrorCS"),sQuery(id+"F3.wireOp",EDGE,"E708.MirrorCS"),sQuery(id+"F3.wireOp",EDGE,"E709.MirrorCS"),sQuery(id+"F3.wireOp",EDGE,"E710.MirrorCS"),sQuery(id+"F3.wireOp",EDGE,"E711.MirrorCS"),sQuery(id+"F3.wireOp",EDGE,"E712.MirrorCS"),sQuery(id+"F3.wireOp",EDGE,"E713.MirrorCS"),sQuery(id+"F3.wireOp",EDGE,"E714.MirrorCS"),sQuery(id+"F3.wireOp",EDGE,"E715.MirrorCS"),sQuery(id+"F3.wireOp",EDGE,"E716.MirrorCS"),sQuery(id+"F3.wireOp",EDGE,"E717.MirrorCS"),sQuery(id+"F3.wireOp",EDGE,"E718.MirrorCS"),sQuery(id+"F3.wireOp",EDGE,"E719.MirrorCS"),sQuery(id+"F3.wireOp",EDGE,"E720.MirrorCS"),sQuery(id+"F3.wireOp",EDGE,"E721.MirrorCS"),sQuery(id+"F3.wireOp",EDGE,"E722.MirrorCS"),sQuery(id+"F3.wireOp",EDGE,"E723.MirrorCS"),sQuery(id+"F3.wireOp",EDGE,"E724.MirrorCS"),sQuery(id+"F3.wireOp",EDGE,"E725.MirrorCS"),sQuery(id+"F3.wireOp",EDGE,"E726.MirrorCS"),sQuery(id+"F3.wireOp",EDGE,"E727.MirrorCS"),sQuery(id+"F3.wireOp",EDGE,"E728.MirrorCS"),sQuery(id+"F3.wireOp",EDGE,"E729.MirrorCS"),sQuery(id+"F3.wireOp",EDGE,"E730.MirrorCS"),sQuery(id+"F3.wireOp",EDGE,"E731.MirrorCS"),sQuery(id+"F3.wireOp",EDGE,"E732.MirrorCS"),sQuery(id+"F3.wireOp",EDGE,"E733.MirrorCS"),sQuery(id+"F3.wireOp",EDGE,"E734.MirrorCS"),sQuery(id+"F3.wireOp",EDGE,"E735.MirrorCS"),sQuery(id+"F3.wireOp",EDGE,"E736.MirrorCS"),sQuery(id+"F3.wireOp",EDGE,"E737.MirrorCS"),sQuery(id+"F3.wireOp",EDGE,"E738.MirrorCS"),sQuery(id+"F3.wireOp",EDGE,"E739.MirrorCS"),sQuery(id+"F3.wireOp",EDGE,"E740.MirrorCS"),sQuery(id+"F3.wireOp",EDGE,"E741.MirrorCS"),sQuery(id+"F3.wireOp",EDGE,"E742.MirrorCS"),sQuery(id+"F3.wireOp",EDGE,"E743.MirrorCS"),sQuery(id+"F3.wireOp",EDGE,"E744.MirrorCS"),sQuery(id+"F3.wireOp",EDGE,"E745.MirrorCS"),sQuery(id+"F3.wireOp",EDGE,"E746.MirrorCS"),sQuery(id+"F3.wireOp",EDGE,"E747.MirrorCS"),sQuery(id+"F3.wireOp",EDGE,"E748.MirrorCS"),sQuery(id+"F3.wireOp",EDGE,"E749.MirrorCS"),sQuery(id+"F3.wireOp",EDGE,"E750.MirrorCS"),sQuery(id+"F3.wireOp",EDGE,"E751.MirrorCS"),sQuery(id+"F3.wireOp",EDGE,"E752.MirrorCS"),sQuery(id+"F3.wireOp",EDGE,"E753.MirrorCS"),sQuery(id+"F3.wireOp",EDGE,"E754.MirrorCS"),sQuery(id+"F3.wireOp",EDGE,"E755.MirrorCS"),sQuery(id+"F3.wireOp",EDGE,"E756.MirrorCS"),sQuery(id+"F3.wireOp",EDGE,"E757.MirrorCS"),sQuery(id+"F3.wireOp",EDGE,"E758.MirrorCS"),sQuery(id+"F3.wireOp",EDGE,"E759.MirrorCS"),sQuery(id+"F3.wireOp",EDGE,"E760.MirrorCS"),sQuery(id+"F3.wireOp",EDGE,"E761.MirrorCS"),sQuery(id+"F3.wireOp",EDGE,"E762.MirrorCS"),sQuery(id+"F3.wireOp",EDGE,"E763.MirrorCS"),sQuery(id+"F3.wireOp",EDGE,"E764.MirrorCS"),sQuery(id+"F3.wireOp",EDGE,"E765.MirrorCS"),sQuery(id+"F3.wireOp",EDGE,"E766.MirrorCS"),sQuery(id+"F3.wireOp",EDGE,"E767.MirrorCS"),sQuery(id+"F3.wireOp",EDGE,"E768.MirrorCS"),sQuery(id+"F3.wireOp",EDGE,"E769.MirrorCS"),sQuery(id+"F3.wireOp",EDGE,"E770.MirrorCS"),sQuery(id+"F3.wireOp",EDGE,"E771.MirrorCS"),sQuery(id+"F3.wireOp",EDGE,"E772.MirrorCS"),sQuery(id+"F3.wireOp",EDGE,"E773.MirrorCS"),sQuery(id+"F3.wireOp",EDGE,"E774.MirrorCS"),sQuery(id+"F3.wireOp",EDGE,"E775.MirrorCS"),sQuery(id+"F3.wireOp",EDGE,"E776.MirrorCS"),sQuery(id+"F3.wireOp",EDGE,"E777.MirrorCS"),sQuery(id+"F3.wireOp",EDGE,"E778.MirrorCS"),sQuery(id+"F3.wireOp",EDGE,"E779.MirrorCS"),sQuery(id+"F3.wireOp",EDGE,"E780.MirrorCS"),sQuery(id+"F3.wireOp",EDGE,"E781.MirrorCS"),sQuery(id+"F3.wireOp",EDGE,"E782.MirrorCS"),sQuery(id+"F3.wireOp",EDGE,"E783.MirrorCS"),sQuery(id+"F3.wireOp",EDGE,"E784.MirrorCS"),sQuery(id+"F3.wireOp",EDGE,"E785.MirrorCS"),sQuery(id+"F3.wireOp",EDGE,"E786.MirrorCS"),sQuery(id+"F3.wireOp",EDGE,"E792.MirrorCS"),sQuery(id+"F3.wireOp",EDGE,"E795.MirrorCS"),sQuery(id+"F3.wireOp",EDGE,"E800.MirrorCS"),sQuery(id+"F3.wireOp",EDGE,"E801.MirrorCS"),sQuery(id+"F3.wireOp",EDGE,"E802.MirrorCS"),sQuery(id+"F3.wireOp",EDGE,"E803.MirrorCS"),sQuery(id+"F3.wireOp",EDGE,"E808.MirrorCS"),sQuery(id+"F3.wireOp",EDGE,"E809.MirrorCS"),sQuery(id+"F3.wireOp",EDGE,"E811.MirrorCS"),sQuery(id+"F3.wireOp",EDGE,"E812.MirrorCS"),sQuery(id+"F3.wireOp",EDGE,"E813.MirrorCS"),sQuery(id+"F3.wireOp",EDGE,"E814.MirrorCS"),sQuery(id+"F3.wireOp",EDGE,"E815.MirrorC"),sQuery(id+"F3.wireOp",EDGE,"E816.MirrorCS"),sQuery(id+"F3.wireOp",EDGE,"E820.MirrorCS"),sQuery(id+"F3.wireOp",EDGE,"E824.MirrorCS"),sQuery(id+"F3.wireOp",EDGE,"E825.MirrorCS"),sQuery(id+"F3.wireOp",EDGE,"E830.MirrorCS"),sQuery(id+"F3.wireOp",EDGE,"E832.MirrorCS"),sQuery(id+"F3.wireOp",EDGE,"E833.MirrorCS"),sQuery(id+"F3.wireOp",EDGE,"E834.MirrorCS"),sQuery(id+"F3.wireOp",EDGE,"E835.MirrorCS"),sQuery(id+"F3.wireOp",EDGE,"E836.MirrorCS"),sQuery(id+"F3.wireOp",EDGE,"E839.MirrorCS"),sQuery(id+"F3.wireOp",EDGE,"E845.MirrorC"),sQuery(id+"F3.wireOp",EDGE,"E847.MirrorCS"),sQuery(id+"F3.wireOp",EDGE,"E849.MirrorCS"),sQuery(id+"F3.wireOp",EDGE,"E850.MirrorCS"),sQuery(id+"F3.wireOp",EDGE,"E851.MirrorCS"),sQuery(id+"F3.wireOp",EDGE,"E853"),sQuery(id+"F3.wireOp",EDGE,"E854"),sQuery(id+"F3.wireOp",EDGE,"E855"),sQuery(id+"F3.wireOp",EDGE,"E856")])],"isStart":false});
            extrude(context, id + "F18", {"entities" : qUnion([Q0]), "operationType" : NewBodyOperationType.ADD, "oppositeDirection" : true, "depth" : 43.14 * mm, "offsetDistance" : 25 * mm});
        }
    });
